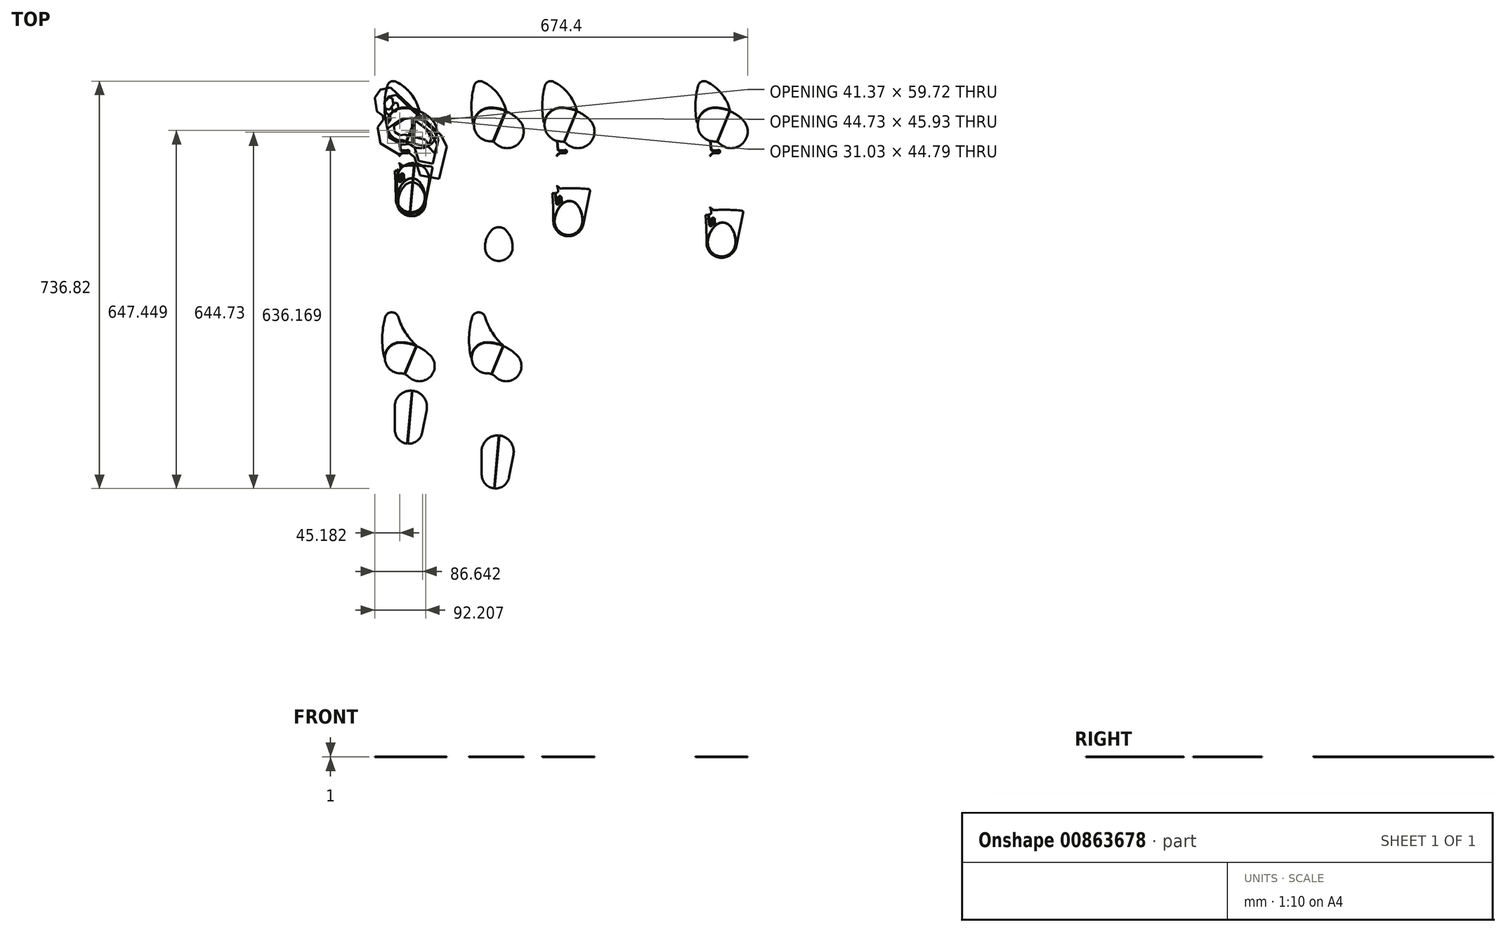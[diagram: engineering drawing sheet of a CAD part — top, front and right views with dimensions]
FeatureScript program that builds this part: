
annotation { "Feature Type Name" : "Feature", "Feature Type Description" : "" }
export const myFeature = defineFeature(function(context is Context, id is Id, definition is map)
    precondition{}
    {
        {
            var Q0;
            Q0=qCreatedBy(makeId("Top.planeOp"),FACE);
            var sketch = newSketch(context, id + "F0", { "sketchPlane" : qUnion([Q0])});
            skLineSegment(sketch, "E0", {"start": v(16.3, 2.6) * mm, "end": v(-34.11, 318.6) * mm, "construction": true});
            skLineSegment(sketch, "E1", {"start": v(66.8, 10.66) * mm, "end": v(119.85, 343.17) * mm, "construction": true});
            skLineSegment(sketch, "E2", {"start": v(40.9, 6.53) * mm, "end": v(40.9, 330.57) * mm, "construction": true});
            skLineSegment(sketch, "E3", {"start": v(-11.1, 295.2) * mm, "end": v(-3.27, 304.3) * mm});
            skLineSegment(sketch, "E4", {"start": v(-3.27, 304.3) * mm, "end": v(3.35, 302.53) * mm});
            skEllipse(sketch, "E5", {"center": v(40.9, 51.28) * mm, "majorRadius": 40 * mm, "minorRadius": 26.46 * mm, "majorAxis": v(0, -1)});
            skLineSegment(sketch, "E6", {"start": v(-9.36, 284.36) * mm, "end": v(-2.16, 282.28) * mm});
            skLineSegment(sketch, "E7", {"start": v(-2.16, 282.28) * mm, "end": v(4.97, 292.1) * mm});
            skLineSegment(sketch, "E8", {"start": v(3.35, 302.53) * mm, "end": v(4.97, 292.1) * mm});
            skLineSegment(sketch, "E9", {"start": v(-11.1, 295.2) * mm, "end": v(-9.36, 284.36) * mm});
            skLineSegment(sketch, "E10", {"start": v(-3.55, 233.47) * mm, "end": v(-5.87, 247.97) * mm});
            skLineSegment(sketch, "E11", {"start": v(-5.87, 247.97) * mm, "end": v(18.1, 264.24) * mm});
            skLineSegment(sketch, "E12", {"start": v(18.1, 264.24) * mm, "end": v(38.87, 267.55) * mm});
            skLineSegment(sketch, "E13", {"start": v(38.87, 267.55) * mm, "end": v(38.87, 221.62) * mm});
            skLineSegment(sketch, "E14", {"start": v(38.87, 221.62) * mm, "end": v(20.02, 227.48) * mm});
            skLineSegment(sketch, "E15", {"start": v(20.02, 227.48) * mm, "end": v(9.19, 225.76) * mm});
            skLineSegment(sketch, "E16", {"start": v(9.19, 225.76) * mm, "end": v(-3.55, 233.47) * mm});
            skLineSegment(sketch, "E17", {"start": v(43.15, 263.17) * mm, "end": v(71.87, 241.94) * mm});
            skLineSegment(sketch, "E18", {"start": v(71.87, 241.94) * mm, "end": v(84.21, 218.72) * mm});
            skLineSegment(sketch, "E19", {"start": v(84.21, 218.72) * mm, "end": v(79.5, 203.45) * mm});
            skLineSegment(sketch, "E20", {"start": v(68.35, 215.06) * mm, "end": v(79.5, 203.45) * mm});
            skLineSegment(sketch, "E21", {"start": v(68.35, 215.06) * mm, "end": v(42.84, 220.86) * mm});
            skLineSegment(sketch, "E22", {"start": v(42.84, 220.86) * mm, "end": v(43.15, 263.17) * mm});
            skLineSegment(sketch, "E23", {"start": v(39.24, 91.2) * mm, "end": v(39.24, 11.36) * mm});
            skLineSegment(sketch, "E24", {"start": v(42.24, 91.23) * mm, "end": v(42.24, 11.34) * mm});
            skLineSegment(sketch, "E25", {"start": v(-18.67, 318.73) * mm, "end": v(0, 322.49) * mm});
            skLineSegment(sketch, "E26", {"start": v(0, 322.49) * mm, "end": v(90.66, 236.65) * mm});
            skLineSegment(sketch, "E27", {"start": v(90.66, 236.65) * mm, "end": v(101.58, 215.64) * mm});
            skLineSegment(sketch, "E28", {"start": v(101.58, 215.64) * mm, "end": v(87.57, 157.1) * mm});
            skLineSegment(sketch, "E29", {"start": v(87.57, 157.1) * mm, "end": v(53.67, 163.5) * mm});
            skLineSegment(sketch, "E30", {"start": v(53.67, 163.5) * mm, "end": v(43.55, 196.6) * mm});
            skLineSegment(sketch, "E31", {"start": v(43.55, 196.6) * mm, "end": v(32.43, 204.68) * mm});
            skLineSegment(sketch, "E32", {"start": v(32.43, 204.68) * mm, "end": v(13.34, 202.21) * mm});
            skLineSegment(sketch, "E33", {"start": v(13.34, 202.21) * mm, "end": v(-18.63, 221.57) * mm});
            skLineSegment(sketch, "E34", {"start": v(-18.63, 221.57) * mm, "end": v(-23.28, 250.67) * mm});
            skLineSegment(sketch, "E35", {"start": v(-23.28, 250.67) * mm, "end": v(-13, 264.21) * mm});
            skLineSegment(sketch, "E36", {"start": v(-13, 264.21) * mm, "end": v(-14.18, 271.56) * mm});
            skLineSegment(sketch, "E37", {"start": v(-14.18, 271.56) * mm, "end": v(-24.79, 279.26) * mm});
            skLineSegment(sketch, "E38", {"start": v(-24.79, 279.26) * mm, "end": v(-28.68, 303.68) * mm});
            skLineSegment(sketch, "E39", {"start": v(-28.68, 303.68) * mm, "end": v(-18.67, 318.73) * mm});
            skSolve(sketch);
        }
        {
            var Q0;
            Q0=makeQuery(id+"F0.imprint","IMPRINT",FACE,{"disambiguationData":[TD([[makeQuery(id+"F0.imprint","IMPRINT",EDGE,{"derivedFrom":sQuery(id+"F0.wireOp",EDGE,"E3")}),1.0]])]});
            extrude(context, id + "F1", {"entities" : qUnion([Q0]), "depth" : 1 * mm, "offsetDistance" : 25 * mm});
        }
        {
            var Q0;
            Q0=makeQuery(id+"F1.opExtrude","SWEPT_BODY",BODY,{"disambiguationData":[OSD([sQuery(id+"F0.wireOp",EDGE,"E3"),sQuery(id+"F0.wireOp",EDGE,"E4"),sQuery(id+"F0.wireOp",EDGE,"E6"),sQuery(id+"F0.wireOp",EDGE,"E7"),sQuery(id+"F0.wireOp",EDGE,"E8"),sQuery(id+"F0.wireOp",EDGE,"E9"),sQuery(id+"F0.wireOp",EDGE,"E10"),sQuery(id+"F0.wireOp",EDGE,"E11"),sQuery(id+"F0.wireOp",EDGE,"E12"),sQuery(id+"F0.wireOp",EDGE,"E13"),sQuery(id+"F0.wireOp",EDGE,"E14"),sQuery(id+"F0.wireOp",EDGE,"E15"),sQuery(id+"F0.wireOp",EDGE,"E16"),sQuery(id+"F0.wireOp",EDGE,"E17"),sQuery(id+"F0.wireOp",EDGE,"E18"),sQuery(id+"F0.wireOp",EDGE,"E19"),sQuery(id+"F0.wireOp",EDGE,"E20"),sQuery(id+"F0.wireOp",EDGE,"E21"),sQuery(id+"F0.wireOp",EDGE,"E22"),sQuery(id+"F0.wireOp",EDGE,"E25"),sQuery(id+"F0.wireOp",EDGE,"E26"),sQuery(id+"F0.wireOp",EDGE,"E27"),sQuery(id+"F0.wireOp",EDGE,"E28"),sQuery(id+"F0.wireOp",EDGE,"E29"),sQuery(id+"F0.wireOp",EDGE,"E30"),sQuery(id+"F0.wireOp",EDGE,"E31"),sQuery(id+"F0.wireOp",EDGE,"E32"),sQuery(id+"F0.wireOp",EDGE,"E33"),sQuery(id+"F0.wireOp",EDGE,"E34"),sQuery(id+"F0.wireOp",EDGE,"E35"),sQuery(id+"F0.wireOp",EDGE,"E36"),sQuery(id+"F0.wireOp",EDGE,"E37"),sQuery(id+"F0.wireOp",EDGE,"E38"),sQuery(id+"F0.wireOp",EDGE,"E39")])]});
            var Q1;
            Q1=makeQuery(id+"F1.opExtrude","CAP_VERTEX",VERTEX,{"disambiguationData":[OSD([sQuery(id+"F0.wireOp",EDGE,"E12"),sQuery(id+"F0.wireOp",EDGE,"E13")])],"isStart":false});
            transform(context, id + "F2", {"entities" : qUnion([Q0]), "transformType" : TransformType.SCALE_UNIFORMLY, "scale" : .75, "scalePoint" : qUnion([Q1]), "makeCopy" : true});
        }
        {
            var Q0;
            Q0=makeQuery(id+"F2.opPattern","COPY",BODY,{"derivedFrom":makeQuery(id+"F1.opExtrude","SWEPT_BODY",BODY,{"disambiguationData":[OSD([sQuery(id+"F0.wireOp",EDGE,"E3"),sQuery(id+"F0.wireOp",EDGE,"E4"),sQuery(id+"F0.wireOp",EDGE,"E6"),sQuery(id+"F0.wireOp",EDGE,"E7"),sQuery(id+"F0.wireOp",EDGE,"E8"),sQuery(id+"F0.wireOp",EDGE,"E9"),sQuery(id+"F0.wireOp",EDGE,"E10"),sQuery(id+"F0.wireOp",EDGE,"E11"),sQuery(id+"F0.wireOp",EDGE,"E12"),sQuery(id+"F0.wireOp",EDGE,"E13"),sQuery(id+"F0.wireOp",EDGE,"E14"),sQuery(id+"F0.wireOp",EDGE,"E15"),sQuery(id+"F0.wireOp",EDGE,"E16"),sQuery(id+"F0.wireOp",EDGE,"E17"),sQuery(id+"F0.wireOp",EDGE,"E18"),sQuery(id+"F0.wireOp",EDGE,"E19"),sQuery(id+"F0.wireOp",EDGE,"E20"),sQuery(id+"F0.wireOp",EDGE,"E21"),sQuery(id+"F0.wireOp",EDGE,"E22"),sQuery(id+"F0.wireOp",EDGE,"E25"),sQuery(id+"F0.wireOp",EDGE,"E26"),sQuery(id+"F0.wireOp",EDGE,"E27"),sQuery(id+"F0.wireOp",EDGE,"E28"),sQuery(id+"F0.wireOp",EDGE,"E29"),sQuery(id+"F0.wireOp",EDGE,"E30"),sQuery(id+"F0.wireOp",EDGE,"E31"),sQuery(id+"F0.wireOp",EDGE,"E32"),sQuery(id+"F0.wireOp",EDGE,"E33"),sQuery(id+"F0.wireOp",EDGE,"E34"),sQuery(id+"F0.wireOp",EDGE,"E35"),sQuery(id+"F0.wireOp",EDGE,"E36"),sQuery(id+"F0.wireOp",EDGE,"E37"),sQuery(id+"F0.wireOp",EDGE,"E38"),sQuery(id+"F0.wireOp",EDGE,"E39")])]}),"instanceName":"1"});
            transform(context, id + "F3", {"entities" : qUnion([Q0]), "transformType" : TransformType.TRANSLATION_3D, "dx" : 0.6 * mm, "dy" : 0 * mm, "dz" : 0 * mm, "makeCopy" : false});
        }
        {
            var Q0;
            Q0=qCreatedBy(makeId("Top.planeOp"),FACE);
            var sketch = newSketch(context, id + "F4", { "sketchPlane" : qUnion([Q0])});
            skLineSegment(sketch, "E40", {"start": v(8.54, 339.93) * mm, "end": v(565.92, 339.93) * mm, "construction": true});
            skPoint(sketch, "E41", {"position": v(287.23, 339.93) * mm});
            skSolve(sketch);
        }
        {
            var Q0;
            Q0=qCreatedBy(makeId("Top.planeOp"),FACE);
            var sketch = newSketch(context, id + "F5", { "sketchPlane" : qUnion([Q0])});
            skArc(sketch, "E42", {"start": v(23.72, 285.12) * mm, "mid": v(-6.28, 255.12) * mm, "end": v(23.72, 225.12) * mm});
            skPoint(sketch, "E43", {"position": v(38.72, 251.89) * mm});
            skLineSegment(sketch, "E44", {"start": v(23.72, 285.12) * mm, "end": v(23.72, 225.12) * mm, "construction": true});
            skLineSegment(sketch, "E45", {"start": v(28.48, 224.17) * mm, "end": v(51.44, 279.6) * mm, "construction": true});
            skLineSegment(sketch, "E46", {"start": v(38.72, 244.3) * mm, "end": v(38.72, 259.48) * mm, "construction": true});
            skPoint(sketch, "E47", {"position": v(39.96, 251.89) * mm});
            skArc(sketch, "E48", {"start": v(50.98, 279.8) * mm, "mid": v(37.6, 283.78) * mm, "end": v(23.72, 285.12) * mm});
            skArc(sketch, "E49", {"start": v(28.01, 224.36) * mm, "mid": v(25.9, 224.93) * mm, "end": v(23.72, 225.12) * mm});
            skLineSegment(sketch, "E50", {"start": v(50.98, 279.8) * mm, "end": v(28.01, 224.36) * mm});
            skLineSegment(sketch, "E51.MirrorCS", {"start": v(51.9, 279.41) * mm, "end": v(28.94, 223.97) * mm});
            skArc(sketch, "E52.MirrorCS", {"start": v(51.9, 279.41) * mm, "mid": v(64.17, 272.77) * mm, "end": v(74.94, 263.9) * mm});
            skArc(sketch, "E53.MirrorCS", {"start": v(74.94, 263.9) * mm, "mid": v(74.94, 221.48) * mm, "end": v(32.5, 221.48) * mm});
            skLineSegment(sketch, "E54.MirrorCS", {"start": v(74.94, 263.9) * mm, "end": v(32.5, 221.48) * mm, "construction": true});
            skArc(sketch, "E55.MirrorCS", {"start": v(28.94, 223.97) * mm, "mid": v(30.83, 222.88) * mm, "end": v(32.5, 221.48) * mm});
            skArc(sketch, "E56", {"start": v(13.72, 114.6) * mm, "mid": v(38.72, 89.6) * mm, "end": v(63.72, 114.6) * mm});
            skLineSegment(sketch, "E57", {"start": v(13.72, 114.6) * mm, "end": v(63.72, 114.6) * mm, "construction": true});
            skArc(sketch, "E58", {"start": v(25.25, 144.75) * mm, "mid": v(16.7, 130.74) * mm, "end": v(13.72, 114.6) * mm});
            skArc(sketch, "E59", {"start": v(52.2, 144.75) * mm, "mid": v(38.72, 150.77) * mm, "end": v(25.25, 144.75) * mm});
            skArc(sketch, "E60", {"start": v(63.72, 114.6) * mm, "mid": v(60.74, 130.74) * mm, "end": v(52.2, 144.75) * mm});
            skLineSegment(sketch, "E61", {"start": v(38.72, 114.6) * mm, "end": v(38.72, 150.77) * mm, "construction": true});
            skArc(sketch, "E62", {"start": v(9.99, 332.78) * mm, "mid": v(0.32, 332.95) * mm, "end": v(-5.91, 325.56) * mm});
            skArc(sketch, "E63", {"start": v(51.82, 280.53) * mm, "mid": v(38.05, 284.7) * mm, "end": v(23.72, 286.12) * mm});
            skArc(sketch, "E64", {"start": v(23.72, 286.12) * mm, "mid": v(1.92, 277.16) * mm, "end": v(-7.28, 255.45) * mm});
            skLineSegment(sketch, "E65", {"start": v(-6.28, 255.12) * mm, "end": v(-6.28, 271.74) * mm, "construction": true});
            skLineSegment(sketch, "E66", {"start": v(96.35, 301.63) * mm, "end": v(20.38, 356.47) * mm, "construction": true});
            skArc(sketch, "E67", {"start": v(-5.91, 325.56) * mm, "mid": v(-10.75, 290.58) * mm, "end": v(-7.28, 255.45) * mm});
            skArc(sketch, "E68", {"start": v(9.99, 332.78) * mm, "mid": v(36.66, 311.26) * mm, "end": v(51.82, 280.53) * mm});
            skSolve(sketch);
        }
        {
            var Q0;
            Q0=qCreatedBy(makeId("Top.planeOp"),FACE);
            var sketch = newSketch(context, id + "F6", { "sketchPlane" : qUnion([Q0])});
            skArc(sketch, "E69", {"start": v(17.17, -139.43) * mm, "mid": v(-10.33, -166.93) * mm, "end": v(17.17, -194.43) * mm});
            skPoint(sketch, "E70", {"position": v(34.67, -170.7) * mm});
            skLineSegment(sketch, "E71", {"start": v(17.17, -139.43) * mm, "end": v(17.17, -194.43) * mm, "construction": true});
            skLineSegment(sketch, "E72", {"start": v(25.6, -196.1) * mm, "end": v(46.64, -145.3) * mm, "construction": true});
            skLineSegment(sketch, "E73", {"start": v(34.67, -201.35) * mm, "end": v(34.67, -140.06) * mm, "construction": true});
            skPoint(sketch, "E74", {"position": v(36.12, -170.7) * mm});
            skArc(sketch, "E75", {"start": v(46.18, -145.1) * mm, "mid": v(31.95, -140.86) * mm, "end": v(17.17, -139.43) * mm});
            skArc(sketch, "E76", {"start": v(25.13, -195.92) * mm, "mid": v(21.22, -194.8) * mm, "end": v(17.17, -194.43) * mm});
            skLineSegment(sketch, "E77", {"start": v(46.18, -145.1) * mm, "end": v(25.13, -195.92) * mm});
            skLineSegment(sketch, "E78.MirrorCS", {"start": v(47.1, -145.49) * mm, "end": v(26.05, -196.3) * mm});
            skArc(sketch, "E79.MirrorCS", {"start": v(47.1, -145.49) * mm, "mid": v(60.16, -152.55) * mm, "end": v(71.62, -161.99) * mm});
            skArc(sketch, "E80.MirrorCS", {"start": v(71.62, -161.99) * mm, "mid": v(71.62, -200.88) * mm, "end": v(32.73, -200.88) * mm});
            skLineSegment(sketch, "E81.MirrorCS", {"start": v(71.62, -161.99) * mm, "end": v(32.73, -200.88) * mm, "construction": true});
            skArc(sketch, "E82.MirrorCS", {"start": v(26.05, -196.3) * mm, "mid": v(29.6, -198.28) * mm, "end": v(32.73, -200.88) * mm});
            skLineSegment(sketch, "E83", {"start": v(32.8, -296.86) * mm, "end": v(36.55, -255.05) * mm, "construction": true});
            skArc(sketch, "E84", {"start": v(14.16, -93.23) * mm, "mid": v(2.03, -84.29) * mm, "end": v(-9.89, -93.5) * mm});
            skArc(sketch, "E85", {"start": v(47.02, -144.37) * mm, "mid": v(32.4, -139.93) * mm, "end": v(17.17, -138.43) * mm});
            skArc(sketch, "E86", {"start": v(17.17, -138.43) * mm, "mid": v(-2.85, -146.65) * mm, "end": v(-11.32, -166.56) * mm});
            skLineSegment(sketch, "E87", {"start": v(-10.33, -166.93) * mm, "end": v(-10.33, -131.36) * mm, "construction": true});
            skLineSegment(sketch, "E88", {"start": v(130.4, -102) * mm, "end": v(54.42, -47.17) * mm, "construction": true});
            skArc(sketch, "E89", {"start": v(-9.89, -93.5) * mm, "mid": v(-15.12, -129.94) * mm, "end": v(-11.32, -166.56) * mm});
            skArc(sketch, "E90", {"start": v(14.16, -93.23) * mm, "mid": v(26.95, -121.14) * mm, "end": v(47.02, -144.37) * mm});
            skLineSegment(sketch, "E91", {"start": v(38.65, -226) * mm, "end": v(30.07, -321.71) * mm});
            skArc(sketch, "E92", {"start": v(7.8, -297.08) * mm, "mid": v(14.25, -313.63) * mm, "end": v(30.07, -321.71) * mm});
            skLineSegment(sketch, "E93", {"start": v(7.8, -297.08) * mm, "end": v(7.44, -255.3) * mm});
            skPoint(sketch, "E94", {"position": v(34.67, -275.95) * mm});
            skArc(sketch, "E95", {"start": v(7.44, -255.3) * mm, "mid": v(16.63, -233.81) * mm, "end": v(38.65, -226) * mm});
            skLineSegment(sketch, "E96.MirrorCS", {"start": v(39.65, -226.1) * mm, "end": v(31.06, -321.8) * mm});
            skArc(sketch, "E97.MirrorCS", {"start": v(57.36, -301.53) * mm, "mid": v(48.06, -316.66) * mm, "end": v(31.06, -321.8) * mm});
            skLineSegment(sketch, "E98.MirrorCS", {"start": v(57.36, -301.53) * mm, "end": v(65.15, -260.48) * mm});
            skArc(sketch, "E99.MirrorCS", {"start": v(65.15, -260.48) * mm, "mid": v(59.93, -237.7) * mm, "end": v(39.65, -226.1) * mm});
            skLineSegment(sketch, "E100", {"start": v(71.1, -321.86) * mm, "end": v(-52.97, -321.86) * mm, "construction": true});
            skLineSegment(sketch, "E101", {"start": v(30.56, -321.76) * mm, "end": v(39.15, -226.05) * mm, "construction": true});
            skSolve(sketch);
        }
        {
            var Q0;
            Q0 = qSketchRegion(id + "F5", true);
            var Q1;
            Q1 = qSketchRegion(id + "F6", true);
            extrude(context, id + "F7", {"entities" : qUnion([Q0, Q1]), "depth" : 1 * mm, "offsetDistance" : 25 * mm});
        }
        {
            var Q0;
            Q0=makeQuery(id+"F7.opExtrude","SWEPT_BODY",BODY,{"disambiguationData":[OSD([sQuery(id+"F5.wireOp",EDGE,"E42"),sQuery(id+"F5.wireOp",EDGE,"E48"),sQuery(id+"F5.wireOp",EDGE,"E49"),sQuery(id+"F5.wireOp",EDGE,"E50")])]});
            var Q1;
            Q1=makeQuery(id+"F7.opExtrude","SWEPT_BODY",BODY,{"disambiguationData":[OSD([sQuery(id+"F5.wireOp",EDGE,"E51.MirrorCS"),sQuery(id+"F5.wireOp",EDGE,"E52.MirrorCS"),sQuery(id+"F5.wireOp",EDGE,"E53.MirrorCS"),sQuery(id+"F5.wireOp",EDGE,"E55.MirrorCS")])]});
            var Q2;
            Q2=makeQuery(id+"F7.opExtrude","SWEPT_BODY",BODY,{"disambiguationData":[OSD([sQuery(id+"F5.wireOp",EDGE,"E56"),sQuery(id+"F5.wireOp",EDGE,"E58"),sQuery(id+"F5.wireOp",EDGE,"E59"),sQuery(id+"F5.wireOp",EDGE,"E60")])]});
            var Q3;
            Q3=makeQuery(id+"F7.opExtrude","SWEPT_BODY",BODY,{"disambiguationData":[OSD([sQuery(id+"F5.wireOp",EDGE,"8W2EzEg6-PsAx-j8A4-CxcC-4UdQx331VMs9"),sQuery(id+"F5.wireOp",EDGE,"E62"),sQuery(id+"F5.wireOp",EDGE,"1FPgRCsu-etEN-6vr9-Zu0G-JbxTRO6JNvhZ"),sQuery(id+"F5.wireOp",EDGE,"E63"),sQuery(id+"F5.wireOp",EDGE,"E64")])]});
            var Q4;
            Q4=makeQuery(id+"F7.opExtrude","SWEPT_BODY",BODY,{"disambiguationData":[OSD([sQuery(id+"F6.wireOp",EDGE,"5b57f492-1596-40e6-b2e3-11fcfe89af0d"),sQuery(id+"F6.wireOp",EDGE,"10afdee0-af68-4db0-a130-1e2b4957d369"),sQuery(id+"F6.wireOp",EDGE,"81680ccf-cd87-4daf-b075-65e9a944a0f2"),sQuery(id+"F6.wireOp",EDGE,"42a77d29-89d0-48d6-aa2a-1530d47a3efc"),sQuery(id+"F6.wireOp",EDGE,"a1937c93-1bbb-44bc-8000-acc418f4d61c")])]});
            var Q5;
            Q5=makeQuery(id+"F7.opExtrude","SWEPT_BODY",BODY,{"disambiguationData":[OSD([sQuery(id+"F6.wireOp",EDGE,"02ee120c-1508-4c41-bed1-1e04da6d7a0c"),sQuery(id+"F6.wireOp",EDGE,"ace646e3-ddf2-4daf-99df-f5f96f0c8b72"),sQuery(id+"F6.wireOp",EDGE,"d4bb21a5-84e0-4ec6-88e1-a15759d7ab0e"),sQuery(id+"F6.wireOp",EDGE,"e1ab6dd2-551a-4460-87ee-2f2734b56fd1")])]});
            var Q6;
            Q6=makeQuery(id+"F7.opExtrude","SWEPT_BODY",BODY,{"disambiguationData":[OSD([sQuery(id+"F6.wireOp",EDGE,"aca01ad1-2727-46c1-b1ea-e2278572d0a3.MirrorCS"),sQuery(id+"F6.wireOp",EDGE,"95053200-b2d1-4fb4-8a27-d9cd398e6184.MirrorCS"),sQuery(id+"F6.wireOp",EDGE,"b14f3b0d-07c5-4903-9c96-b1073ed3af53.MirrorCS"),sQuery(id+"F6.wireOp",EDGE,"13823a02-7994-452b-b934-c440785b61fb.MirrorCS")])]});
            var Q7;
            Q7=makeQuery(id+"F7.opExtrude","SWEPT_BODY",BODY,{"disambiguationData":[OSD([sQuery(id+"F6.wireOp",EDGE,"76ac6f00-afaf-4b2d-95c2-d09c5d23ff7b"),sQuery(id+"F6.wireOp",EDGE,"820a2da9-31c0-4ea2-8999-fd9844493cd6"),sQuery(id+"F6.wireOp",EDGE,"e1ef3a47-9e0c-4530-8c34-01f70c3173e6"),sQuery(id+"F6.wireOp",EDGE,"5ff26bff-9000-4c28-a5b2-e0ee19cc0048")])]});
            var Q8;
            Q8=makeQuery(id+"F7.opExtrude","SWEPT_BODY",BODY,{"disambiguationData":[OSD([sQuery(id+"F6.wireOp",EDGE,"b6ba2a53-2d88-4030-befe-966a330606390.MirrorCS"),sQuery(id+"F6.wireOp",EDGE,"e51e67fa-598f-4ce7-9503-9b7065003b4d0.MirrorCS"),sQuery(id+"F6.wireOp",EDGE,"5a4d4938-92c4-42d2-ae7a-708136eab2620.MirrorCS"),sQuery(id+"F6.wireOp",EDGE,"2ea4096e-a5a6-4afc-88fb-b437cae464f20.MirrorCS")])]});
            var Q9;
            Q9=makeQuery(id+"F7.opExtrude","SWEPT_BODY",BODY,{"disambiguationData":[OSD([sQuery(id+"F6.wireOp",EDGE,"E84"),sQuery(id+"F6.wireOp",EDGE,"E85"),sQuery(id+"F6.wireOp",EDGE,"E86"),sQuery(id+"F6.wireOp",EDGE,"E89"),sQuery(id+"F6.wireOp",EDGE,"E90")])]});
            var Q10;
            Q10=makeQuery(id+"F7.opExtrude","SWEPT_BODY",BODY,{"disambiguationData":[OSD([sQuery(id+"F6.wireOp",EDGE,"E69"),sQuery(id+"F6.wireOp",EDGE,"E75"),sQuery(id+"F6.wireOp",EDGE,"E76"),sQuery(id+"F6.wireOp",EDGE,"E77")])]});
            var Q11;
            Q11=makeQuery(id+"F7.opExtrude","SWEPT_BODY",BODY,{"disambiguationData":[OSD([sQuery(id+"F6.wireOp",EDGE,"E78.MirrorCS"),sQuery(id+"F6.wireOp",EDGE,"E79.MirrorCS"),sQuery(id+"F6.wireOp",EDGE,"E80.MirrorCS"),sQuery(id+"F6.wireOp",EDGE,"E82.MirrorCS")])]});
            var Q12;
            Q12=makeQuery(id+"F7.opExtrude","SWEPT_BODY",BODY,{"disambiguationData":[OSD([sQuery(id+"F6.wireOp",EDGE,"E91"),sQuery(id+"F6.wireOp",EDGE,"E92"),sQuery(id+"F6.wireOp",EDGE,"E93"),sQuery(id+"F6.wireOp",EDGE,"E95")])]});
            var Q13;
            Q13=makeQuery(id+"F7.opExtrude","SWEPT_BODY",BODY,{"disambiguationData":[OSD([sQuery(id+"F6.wireOp",EDGE,"E96.MirrorCS"),sQuery(id+"F6.wireOp",EDGE,"E97.MirrorCS"),sQuery(id+"F6.wireOp",EDGE,"E98.MirrorCS"),sQuery(id+"F6.wireOp",EDGE,"E99.MirrorCS")])]});
            transform(context, id + "F8", {"entities" : qUnion([Q0, Q1, Q2, Q3, Q4, Q5, Q6, Q7, Q8, Q9, Q10, Q11, Q12, Q13]), "transformType" : TransformType.TRANSLATION_3D, "dx" : 157 * mm, "dy" : 0 * mm, "dz" : 0 * mm, "makeCopy" : true});
        }
        {
            var Q0;
            Q0=makeQuery(id+"F8.opPattern","COPY",BODY,{"derivedFrom":makeQuery(id+"F7.opExtrude","SWEPT_BODY",BODY,{"disambiguationData":[OSD([sQuery(id+"F5.wireOp",EDGE,"E56"),sQuery(id+"F5.wireOp",EDGE,"E58"),sQuery(id+"F5.wireOp",EDGE,"E59"),sQuery(id+"F5.wireOp",EDGE,"E60")])]}),"instanceName":"1"});
            var Q1;
            Q1=makeQuery(id+"F8.opPattern","COPY",BODY,{"derivedFrom":makeQuery(id+"F7.opExtrude","SWEPT_BODY",BODY,{"disambiguationData":[OSD([sQuery(id+"F6.wireOp",EDGE,"76ac6f00-afaf-4b2d-95c2-d09c5d23ff7b"),sQuery(id+"F6.wireOp",EDGE,"820a2da9-31c0-4ea2-8999-fd9844493cd6"),sQuery(id+"F6.wireOp",EDGE,"e1ef3a47-9e0c-4530-8c34-01f70c3173e6"),sQuery(id+"F6.wireOp",EDGE,"5ff26bff-9000-4c28-a5b2-e0ee19cc0048")])]}),"instanceName":"1"});
            var Q2;
            Q2=makeQuery(id+"F8.opPattern","COPY",BODY,{"derivedFrom":makeQuery(id+"F7.opExtrude","SWEPT_BODY",BODY,{"disambiguationData":[OSD([sQuery(id+"F6.wireOp",EDGE,"b6ba2a53-2d88-4030-befe-966a330606390.MirrorCS"),sQuery(id+"F6.wireOp",EDGE,"e51e67fa-598f-4ce7-9503-9b7065003b4d0.MirrorCS"),sQuery(id+"F6.wireOp",EDGE,"5a4d4938-92c4-42d2-ae7a-708136eab2620.MirrorCS"),sQuery(id+"F6.wireOp",EDGE,"2ea4096e-a5a6-4afc-88fb-b437cae464f20.MirrorCS")])]}),"instanceName":"1"});
            var Q3;
            Q3=makeQuery(id+"F8.opPattern","COPY",BODY,{"derivedFrom":makeQuery(id+"F7.opExtrude","SWEPT_BODY",BODY,{"disambiguationData":[OSD([sQuery(id+"F6.wireOp",EDGE,"E91"),sQuery(id+"F6.wireOp",EDGE,"E92"),sQuery(id+"F6.wireOp",EDGE,"E93"),sQuery(id+"F6.wireOp",EDGE,"E95")])]}),"instanceName":"1"});
            var Q4;
            Q4=makeQuery(id+"F8.opPattern","COPY",BODY,{"derivedFrom":makeQuery(id+"F7.opExtrude","SWEPT_BODY",BODY,{"disambiguationData":[OSD([sQuery(id+"F6.wireOp",EDGE,"E96.MirrorCS"),sQuery(id+"F6.wireOp",EDGE,"E97.MirrorCS"),sQuery(id+"F6.wireOp",EDGE,"E98.MirrorCS"),sQuery(id+"F6.wireOp",EDGE,"E99.MirrorCS")])]}),"instanceName":"1"});
            transform(context, id + "F9", {"entities" : qUnion([Q0, Q1, Q2, Q3, Q4]), "transformType" : TransformType.TRANSLATION_3D, "dx" : 0 * mm, "dy" : -81 * mm, "dz" : 0 * mm, "makeCopy" : false});
        }
        {
            var Q0;
            Q0=makeQuery(id+"F7.opExtrude","SWEPT_BODY",BODY,{"disambiguationData":[OSD([sQuery(id+"F6.wireOp",EDGE,"E91"),sQuery(id+"F6.wireOp",EDGE,"E92"),sQuery(id+"F6.wireOp",EDGE,"E93"),sQuery(id+"F6.wireOp",EDGE,"E95")])]});
            var Q1;
            Q1=makeQuery(id+"F7.opExtrude","SWEPT_BODY",BODY,{"disambiguationData":[OSD([sQuery(id+"F6.wireOp",EDGE,"E96.MirrorCS"),sQuery(id+"F6.wireOp",EDGE,"E97.MirrorCS"),sQuery(id+"F6.wireOp",EDGE,"E98.MirrorCS"),sQuery(id+"F6.wireOp",EDGE,"E99.MirrorCS")])]});
            transform(context, id + "F10", {"entities" : qUnion([Q0, Q1]), "transformType" : TransformType.TRANSLATION_3D, "dx" : 4 * mm, "dy" : 411.6 * mm, "dz" : 0 * mm, "makeCopy" : true});
        }
        {
            var Q0;
            Q0=qCreatedBy(makeId("Top.planeOp"),FACE);
            var sketch = newSketch(context, id + "F11", { "sketchPlane" : qUnion([Q0])});
            skLineSegment(sketch, "E102", {"start": v(29.12, 224.4) * mm, "end": v(51.7, 278.95) * mm});
            skArc(sketch, "E103", {"start": v(74.94, 263.9) * mm, "mid": v(64.38, 272.63) * mm, "end": v(52.37, 279.21) * mm});
            skArc(sketch, "E104", {"start": v(32.5, 221.48) * mm, "mid": v(74.94, 221.48) * mm, "end": v(74.94, 263.9) * mm});
            skLineSegment(sketch, "E105", {"start": v(50.78, 279.33) * mm, "end": v(28.2, 224.8) * mm});
            skArc(sketch, "E106", {"start": v(50.5, 279.98) * mm, "mid": v(37.36, 283.82) * mm, "end": v(23.72, 285.12) * mm});
            skArc(sketch, "E107", {"start": v(23.72, 285.12) * mm, "mid": v(-6.28, 255.12) * mm, "end": v(23.72, 225.12) * mm});
            skLineSegment(sketch, "E108", {"start": v(23.72, 286.12) * mm, "end": v(23.72, 286.12) * mm});
            skArc(sketch, "E109", {"start": v(50.9, 280.9) * mm, "mid": v(37.56, 284.8) * mm, "end": v(23.72, 286.12) * mm});
            skLineSegment(sketch, "E110", {"start": v(9.99, 332.78) * mm, "end": v(9.99, 332.78) * mm});
            skArc(sketch, "E111", {"start": v(15.78, 225.8) * mm, "mid": v(-6.39, 259.12) * mm, "end": v(23.72, 285.5) * mm});
            skArc(sketch, "E112", {"start": v(23.72, 285.5) * mm, "mid": v(37.43, 284.2) * mm, "end": v(50.64, 280.33) * mm});
            skArc(sketch, "E113", {"start": v(23.72, 224.74) * mm, "mid": v(25.61, 224.6) * mm, "end": v(27.46, 224.15) * mm});
            skLineSegment(sketch, "E114", {"start": v(51.13, 279.19) * mm, "end": v(28.54, 224.65) * mm});
            skArc(sketch, "E115", {"start": v(-1.86, 238.29) * mm, "mid": v(-3.23, 269.65) * mm, "end": v(23.72, 285.74) * mm});
            skArc(sketch, "E116", {"start": v(23.72, 285.74) * mm, "mid": v(37.5, 284.43) * mm, "end": v(50.77, 280.55) * mm});
            skLineSegment(sketch, "E117", {"start": v(28.77, 224.55) * mm, "end": v(51.36, 279.09) * mm});
            skArc(sketch, "E118", {"start": v(52.51, 279.56) * mm, "mid": v(64.59, 272.94) * mm, "end": v(75.2, 264.17) * mm});
            skArc(sketch, "E119", {"start": v(75.2, 264.17) * mm, "mid": v(77.76, 224.12) * mm, "end": v(38.37, 216.48) * mm});
            skArc(sketch, "E120", {"start": v(32.24, 221.21) * mm, "mid": v(30.8, 222.45) * mm, "end": v(29.18, 223.44) * mm});
            skArc(sketch, "E121", {"start": v(76.61, 265.59) * mm, "mid": v(84.9, 251.42) * mm, "end": v(85.17, 235.01) * mm});
            skArc(sketch, "E122", {"start": v(-9.83, 255.12) * mm, "mid": v(-8.9, 247.25) * mm, "end": v(-6.14, 239.83) * mm});
            skLineSegment(sketch, "E123.bottom", {"start": v(7.72, 198.27) * mm, "end": v(12.7, 198.76) * mm});
            skLineSegment(sketch, "E123.top", {"start": v(7.86, 196.78) * mm, "end": v(12.84, 197.27) * mm});
            skLineSegment(sketch, "E123.left", {"start": v(7.27, 197.73) * mm, "end": v(7.32, 197.23) * mm});
            skLineSegment(sketch, "E124.bottom", {"start": v(8.01, 195.29) * mm, "end": v(12.99, 195.78) * mm});
            skLineSegment(sketch, "E124.top", {"start": v(8.16, 193.8) * mm, "end": v(13.13, 194.29) * mm});
            skLineSegment(sketch, "E124.left", {"start": v(7.56, 194.74) * mm, "end": v(7.61, 194.24) * mm});
            skLineSegment(sketch, "E124.right", {"start": v(13.53, 195.33) * mm, "end": v(13.58, 194.83) * mm});
            skLineSegment(sketch, "E125.bottom", {"start": v(8.3, 192.3) * mm, "end": v(13.28, 192.8) * mm});
            skLineSegment(sketch, "E125.top", {"start": v(8.45, 190.81) * mm, "end": v(13.43, 191.3) * mm});
            skArc(sketch, "E126", {"start": v(23.72, 225.12) * mm, "mid": v(25.67, 224.97) * mm, "end": v(27.58, 224.5) * mm});
            skArc(sketch, "E127", {"start": v(29.35, 223.77) * mm, "mid": v(31.02, 222.75) * mm, "end": v(32.5, 221.48) * mm});
            skArc(sketch, "E128", {"start": v(-6.27, 325.67) * mm, "mid": v(-11.1, 292.42) * mm, "end": v(-8.38, 258.94) * mm});
            skArc(sketch, "E129", {"start": v(76.61, 265.59) * mm, "mid": v(73.37, 268.64) * mm, "end": v(69.95, 271.5) * mm});
            skArc(sketch, "E130", {"start": v(-8.2, 326.18) * mm, "mid": v(-13.12, 291.64) * mm, "end": v(-10.01, 256.9) * mm});
            skArc(sketch, "E131", {"start": v(-10.01, 256.9) * mm, "mid": v(-9.87, 256.02) * mm, "end": v(-9.83, 255.12) * mm});
            skLineSegment(sketch, "E132", {"start": v(-9.83, 267.62) * mm, "end": v(-9.83, 242.62) * mm, "construction": true});
            skLineSegment(sketch, "E133.top", {"start": v(7.28, 202.75) * mm, "end": v(12.25, 203.24) * mm});
            skLineSegment(sketch, "E133.left", {"start": v(6.68, 203.7) * mm, "end": v(6.73, 203.2) * mm});
            skLineSegment(sketch, "E134", {"start": v(12.65, 204.29) * mm, "end": v(12.7, 203.79) * mm});
            skArc(sketch, "E135", {"start": v(8.67, 188.57) * mm, "mid": v(6.66, 189.18) * mm, "end": v(5.67, 191.04) * mm});
            skLineSegment(sketch, "E136", {"start": v(5.67, 191.04) * mm, "end": v(4.4, 203.98) * mm});
            skArc(sketch, "E137", {"start": v(4.4, 203.98) * mm, "mid": v(0.81, 222.4) * mm, "end": v(-6.14, 239.83) * mm});
            skLineSegment(sketch, "E138.bottom", {"start": v(7.42, 201.26) * mm, "end": v(12.4, 201.75) * mm});
            skLineSegment(sketch, "E138.top", {"start": v(7.57, 199.77) * mm, "end": v(12.55, 200.26) * mm});
            skLineSegment(sketch, "E138.left", {"start": v(6.97, 200.71) * mm, "end": v(7.02, 200.22) * mm});
            skLineSegment(sketch, "E138.right", {"start": v(12.95, 201.3) * mm, "end": v(13, 200.8) * mm});
            skArc(sketch, "E139", {"start": v(74.67, 188.57) * mm, "mid": v(41.67, 190.2) * mm, "end": v(8.67, 188.57) * mm, "construction": true});
            skLineSegment(sketch, "E140", {"start": v(8.67, 188.57) * mm, "end": v(29.1, 190.58) * mm, "construction": true});
            skLineSegment(sketch, "E141", {"start": v(32.22, 174.02) * mm, "end": v(72.8, 174.02) * mm, "construction": true});
            skLineSegment(sketch, "E142", {"start": v(41.67, 190.2) * mm, "end": v(41.67, 161.92) * mm, "construction": true});
            skArc(sketch, "E143", {"start": v(74.67, 188.57) * mm, "mid": v(76.69, 189.18) * mm, "end": v(77.68, 191.04) * mm, "construction": true});
            skLineSegment(sketch, "E144", {"start": v(77.68, 191.04) * mm, "end": v(75.88, 172.73) * mm, "construction": true});
            skLineSegment(sketch, "E145", {"start": v(77.68, 191.04) * mm, "end": v(77.68, 176.48) * mm, "construction": true});
            skLineSegment(sketch, "E146", {"start": v(5.67, 191.04) * mm, "end": v(7.23, 175.16) * mm, "construction": true});
            skArc(sketch, "E147", {"start": v(77.68, 191.04) * mm, "mid": v(80.65, 213.16) * mm, "end": v(85.17, 235.01) * mm, "construction": true});
            skLineSegment(sketch, "E148", {"start": v(41.67, 190.2) * mm, "end": v(59.6, 190.2) * mm, "construction": true});
            skArc(sketch, "E149", {"start": v(85.17, 235.01) * mm, "mid": v(81.08, 215.6) * mm, "end": v(78.2, 195.97) * mm});
            skArc(sketch, "E150", {"start": v(13.63, 189.02) * mm, "mid": v(11.15, 188.8) * mm, "end": v(8.67, 188.57) * mm});
            skArc(sketch, "E151", {"start": v(13.63, 189.02) * mm, "mid": v(17.25, 190.31) * mm, "end": v(19.76, 193.22) * mm});
            skArc(sketch, "E152", {"start": v(19.76, 193.22) * mm, "mid": v(20.62, 194.2) * mm, "end": v(21.86, 194.62) * mm});
            skArc(sketch, "E153", {"start": v(78.2, 195.97) * mm, "mid": v(77.2, 194.14) * mm, "end": v(75.2, 193.54) * mm});
            skArc(sketch, "E154", {"start": v(75.2, 193.54) * mm, "mid": v(48.55, 195.12) * mm, "end": v(21.86, 194.62) * mm});
            skArc(sketch, "E155", {"start": v(51.58, 281.5) * mm, "mid": v(36.35, 311.65) * mm, "end": v(9.99, 332.78) * mm});
            skArc(sketch, "E156", {"start": v(-6.27, 325.67) * mm, "mid": v(0.17, 333.3) * mm, "end": v(10.15, 333.12) * mm});
            skArc(sketch, "E157", {"start": v(-8.2, 326.18) * mm, "mid": v(-0.66, 335.12) * mm, "end": v(11.05, 334.9) * mm});
            skArc(sketch, "E158", {"start": v(10.15, 333.12) * mm, "mid": v(36.64, 311.89) * mm, "end": v(51.94, 281.58) * mm});
            skArc(sketch, "E159", {"start": v(11.05, 334.9) * mm, "mid": v(32.2, 319.76) * mm, "end": v(47.56, 298.74) * mm});
            skArc(sketch, "E160", {"start": v(47.56, 298.74) * mm, "mid": v(57.27, 283.9) * mm, "end": v(69.95, 271.5) * mm});
            skArc(sketch, "E161", {"start": v(-7.3, 258.1) * mm, "mid": v(-7.4, 258.43) * mm, "end": v(-7.67, 258.63) * mm});
            skArc(sketch, "E162", {"start": v(-7.68, 258.14) * mm, "mid": v(-7.7, 258.22) * mm, "end": v(-7.77, 258.27) * mm});
            skArc(sketch, "E163", {"start": v(13.63, 189.02) * mm, "mid": v(15.53, 190.02) * mm, "end": v(16.15, 192.07) * mm});
            skLineSegment(sketch, "E164", {"start": v(14.93, 204.51) * mm, "end": v(16.15, 192.07) * mm});
            skLineSegment(sketch, "E165", {"start": v(11.88, 207.01) * mm, "end": v(4.14, 206.25) * mm});
            skLineSegment(sketch, "E166", {"start": v(13.63, 189.02) * mm, "end": v(8.67, 188.57) * mm});
            skArc(sketch, "E167", {"start": v(5.67, 191.04) * mm, "mid": v(6.66, 189.18) * mm, "end": v(8.67, 188.57) * mm});
            skLineSegment(sketch, "E168", {"start": v(7.13, 204.25) * mm, "end": v(12.1, 204.74) * mm});
            skLineSegment(sketch, "E169", {"start": v(7.86, 191.76) * mm, "end": v(7.9, 191.26) * mm});
            skLineSegment(sketch, "E170", {"start": v(13.88, 191.85) * mm, "end": v(13.83, 192.34) * mm});
            skArc(sketch, "E171", {"start": v(8.67, 188.57) * mm, "mid": v(7.02, 188.93) * mm, "end": v(5.9, 190.18) * mm});
            skArc(sketch, "E172", {"start": v(4.35, 204.35) * mm, "mid": v(4.25, 205.3) * mm, "end": v(4.14, 206.25) * mm});
            skArc(sketch, "E173", {"start": v(-2.25, 238.03) * mm, "mid": v(-6.53, 247.97) * mm, "end": v(-7.15, 258.78) * mm, "construction": true});
            skArc(sketch, "E174", {"start": v(-2.25, 238.03) * mm, "mid": v(5.72, 221.98) * mm, "end": v(9.62, 204.5) * mm, "construction": true});
            skArc(sketch, "E175", {"start": v(13.85, 192.1) * mm, "mid": v(16.1, 192.9) * mm, "end": v(17.73, 194.64) * mm, "construction": true});
            skArc(sketch, "E176", {"start": v(13.26, 198.07) * mm, "mid": v(15.52, 198.86) * mm, "end": v(17.14, 200.61) * mm, "construction": true});
            skArc(sketch, "E177", {"start": v(17.73, 194.64) * mm, "mid": v(19.36, 196.39) * mm, "end": v(21.6, 197.18) * mm, "construction": true});
            skArc(sketch, "E178", {"start": v(17.14, 200.61) * mm, "mid": v(18.77, 202.36) * mm, "end": v(21.02, 203.16) * mm, "construction": true});
            skLineSegment(sketch, "E179", {"start": v(21.6, 197.18) * mm, "end": v(41.78, 199.17) * mm, "construction": true});
            skLineSegment(sketch, "E180", {"start": v(21.02, 203.16) * mm, "end": v(31.24, 204.16) * mm, "construction": true});
            skLineSegment(sketch, "E181", {"start": v(30.75, 209.14) * mm, "end": v(20.53, 208.13) * mm, "construction": true});
            skArc(sketch, "E182", {"start": v(31.24, 204.16) * mm, "mid": v(33.48, 206.9) * mm, "end": v(30.75, 209.14) * mm, "construction": true});
            skArc(sketch, "E183", {"start": v(20.53, 208.13) * mm, "mid": v(18.7, 208.69) * mm, "end": v(17.8, 210.37) * mm, "construction": true});
            skLineSegment(sketch, "E184", {"start": v(17.8, 210.37) * mm, "end": v(16.34, 225.17) * mm, "construction": true});
            skArc(sketch, "E185", {"start": v(23.72, 285.12) * mm, "mid": v(-6.02, 259.07) * mm, "end": v(15.88, 226.16) * mm});
            skArc(sketch, "E186", {"start": v(23.72, 225.12) * mm, "mid": v(20.35, 225.3) * mm, "end": v(17.03, 225.88) * mm});
            skArc(sketch, "E187", {"start": v(16.34, 225.17) * mm, "mid": v(16.34, 225.6) * mm, "end": v(16.4, 226.03) * mm, "construction": true});
            skLineSegment(sketch, "E188", {"start": v(13.15, 226.84) * mm, "end": v(19.65, 225.2) * mm, "construction": true});
            skArc(sketch, "E189", {"start": v(23.72, 224.74) * mm, "mid": v(20.31, 224.94) * mm, "end": v(16.94, 225.5) * mm});
            skArc(sketch, "E190", {"start": v(17.03, 225.88) * mm, "mid": v(16.6, 225.78) * mm, "end": v(16.42, 225.38) * mm});
            skArc(sketch, "E191", {"start": v(15.88, 226.16) * mm, "mid": v(16.16, 225.97) * mm, "end": v(16.25, 225.64) * mm});
            skArc(sketch, "E192", {"start": v(16.94, 225.5) * mm, "mid": v(16.84, 225.49) * mm, "end": v(16.8, 225.39) * mm});
            skArc(sketch, "E193", {"start": v(15.78, 225.8) * mm, "mid": v(15.85, 225.75) * mm, "end": v(15.88, 225.67) * mm});
            skLineSegment(sketch, "E194", {"start": v(20.53, 208.13) * mm, "end": v(21.02, 203.16) * mm, "construction": true});
            skArc(sketch, "E195", {"start": v(16.25, 225.64) * mm, "mid": v(16.24, 225.4) * mm, "end": v(16.25, 225.16) * mm});
            skArc(sketch, "E196", {"start": v(16.42, 225.38) * mm, "mid": v(16.42, 225.28) * mm, "end": v(16.43, 225.18) * mm});
            skArc(sketch, "E197", {"start": v(15.88, 225.67) * mm, "mid": v(15.87, 225.4) * mm, "end": v(15.88, 225.13) * mm});
            skLineSegment(sketch, "E198", {"start": v(16.25, 225.16) * mm, "end": v(17.71, 210.37) * mm});
            skLineSegment(sketch, "E199", {"start": v(15.88, 225.13) * mm, "end": v(17.34, 210.33) * mm});
            skLineSegment(sketch, "E200", {"start": v(16.43, 225.18) * mm, "end": v(17.88, 210.38) * mm});
            skArc(sketch, "E201", {"start": v(17.88, 210.38) * mm, "mid": v(18.76, 208.75) * mm, "end": v(20.52, 208.22) * mm});
            skArc(sketch, "E202", {"start": v(18.26, 210.42) * mm, "mid": v(19, 209.04) * mm, "end": v(20.49, 208.6) * mm});
            skArc(sketch, "E203", {"start": v(17.71, 210.37) * mm, "mid": v(18.64, 208.62) * mm, "end": v(20.54, 208.04) * mm});
            skArc(sketch, "E204", {"start": v(17.34, 210.33) * mm, "mid": v(18.4, 208.33) * mm, "end": v(20.58, 207.67) * mm});
            skLineSegment(sketch, "E205", {"start": v(20.52, 208.22) * mm, "end": v(30.74, 209.22) * mm});
            skLineSegment(sketch, "E206", {"start": v(20.49, 208.6) * mm, "end": v(30.7, 209.6) * mm});
            skLineSegment(sketch, "E207", {"start": v(20.54, 208.04) * mm, "end": v(30.76, 209.05) * mm});
            skLineSegment(sketch, "E208", {"start": v(20.58, 207.67) * mm, "end": v(30.8, 208.68) * mm});
            skArc(sketch, "E209", {"start": v(30.8, 208.68) * mm, "mid": v(33.02, 206.85) * mm, "end": v(31.2, 204.62) * mm});
            skArc(sketch, "E210", {"start": v(30.76, 209.05) * mm, "mid": v(33.4, 206.89) * mm, "end": v(31.23, 204.25) * mm});
            skArc(sketch, "E211", {"start": v(30.74, 209.22) * mm, "mid": v(33.57, 206.9) * mm, "end": v(31.25, 204.07) * mm});
            skArc(sketch, "E212", {"start": v(30.7, 209.6) * mm, "mid": v(33.94, 206.94) * mm, "end": v(31.28, 203.7) * mm});
            skLineSegment(sketch, "E213", {"start": v(31.25, 204.07) * mm, "end": v(21.03, 203.07) * mm});
            skLineSegment(sketch, "E214", {"start": v(31.28, 203.7) * mm, "end": v(21.07, 202.7) * mm});
            skLineSegment(sketch, "E215", {"start": v(31.23, 204.25) * mm, "end": v(21.01, 203.24) * mm});
            skLineSegment(sketch, "E216", {"start": v(31.2, 204.62) * mm, "end": v(20.98, 203.62) * mm});
            skArc(sketch, "E217", {"start": v(21.07, 202.7) * mm, "mid": v(19.02, 201.97) * mm, "end": v(17.55, 200.39) * mm});
            skArc(sketch, "E218", {"start": v(21.03, 203.07) * mm, "mid": v(18.82, 202.29) * mm, "end": v(17.22, 200.57) * mm});
            skArc(sketch, "E219", {"start": v(21.01, 203.24) * mm, "mid": v(18.72, 202.43) * mm, "end": v(17.07, 200.65) * mm});
            skArc(sketch, "E220", {"start": v(20.98, 203.62) * mm, "mid": v(18.52, 202.75) * mm, "end": v(16.74, 200.84) * mm});
            skArc(sketch, "E221", {"start": v(16.74, 200.84) * mm, "mid": v(15.45, 199.38) * mm, "end": v(13.66, 198.6) * mm});
            skArc(sketch, "E222", {"start": v(17.07, 200.65) * mm, "mid": v(15.67, 199.07) * mm, "end": v(13.73, 198.23) * mm});
            skArc(sketch, "E223", {"start": v(17.22, 200.57) * mm, "mid": v(15.73, 198.9) * mm, "end": v(13.68, 198.04) * mm});
            skArc(sketch, "E224", {"start": v(17.55, 200.39) * mm, "mid": v(15.95, 198.6) * mm, "end": v(13.74, 197.67) * mm});
            skArc(sketch, "E225", {"start": v(23.72, 286.12) * mm, "mid": v(-3.56, 269.83) * mm, "end": v(-2.18, 238.08) * mm});
            skArc(sketch, "E226", {"start": v(-7.3, 258.1) * mm, "mid": v(-6.54, 247.62) * mm, "end": v(-2.32, 237.99) * mm});
            skArc(sketch, "E227", {"start": v(-7.68, 258.14) * mm, "mid": v(-6.9, 247.53) * mm, "end": v(-2.64, 237.78) * mm});
            skArc(sketch, "E228", {"start": v(-2.18, 238.08) * mm, "mid": v(5.72, 222.25) * mm, "end": v(9.65, 205) * mm});
            skArc(sketch, "E229", {"start": v(-1.86, 238.29) * mm, "mid": v(6.07, 222.37) * mm, "end": v(10.03, 205.03) * mm});
            skArc(sketch, "E230", {"start": v(-2.32, 237.99) * mm, "mid": v(5.55, 222.2) * mm, "end": v(9.48, 204.98) * mm});
            skArc(sketch, "E231", {"start": v(-2.64, 237.78) * mm, "mid": v(5.2, 222.06) * mm, "end": v(9.1, 204.94) * mm});
            skArc(sketch, "E232", {"start": v(32.24, 221.21) * mm, "mid": v(34.69, 219.02) * mm, "end": v(37.35, 217.1) * mm});
            skArc(sketch, "E233", {"start": v(32.5, 221.48) * mm, "mid": v(34.92, 219.32) * mm, "end": v(37.55, 217.42) * mm});
            skArc(sketch, "E234", {"start": v(74.94, 263.9) * mm, "mid": v(77.46, 224.35) * mm, "end": v(38.56, 216.8) * mm});
            skArc(sketch, "E235", {"start": v(38, 217.14) * mm, "mid": v(37.7, 216.4) * mm, "end": v(37.65, 215.58) * mm, "construction": true});
            skLineSegment(sketch, "E236", {"start": v(44.5, 213.14) * mm, "end": v(31.5, 221.14) * mm, "construction": true});
            skArc(sketch, "E237", {"start": v(37.55, 217.42) * mm, "mid": v(37.76, 217.15) * mm, "end": v(37.74, 216.81) * mm});
            skArc(sketch, "E238", {"start": v(38.56, 216.8) * mm, "mid": v(38.12, 216.84) * mm, "end": v(37.82, 216.52) * mm});
            skArc(sketch, "E239", {"start": v(37.35, 217.1) * mm, "mid": v(37.4, 217.04) * mm, "end": v(37.4, 216.96) * mm});
            skArc(sketch, "E240", {"start": v(38.37, 216.48) * mm, "mid": v(38.26, 216.5) * mm, "end": v(38.18, 216.41) * mm});
            skArc(sketch, "E241", {"start": v(37.82, 216.52) * mm, "mid": v(37.73, 216.06) * mm, "end": v(37.74, 215.6) * mm});
            skArc(sketch, "E242", {"start": v(38.18, 216.41) * mm, "mid": v(38.1, 216.02) * mm, "end": v(38.1, 215.63) * mm});
            skArc(sketch, "E243", {"start": v(37.74, 216.81) * mm, "mid": v(37.58, 216.2) * mm, "end": v(37.56, 215.58) * mm});
            skArc(sketch, "E244", {"start": v(37.4, 216.96) * mm, "mid": v(37.2, 216.26) * mm, "end": v(37.19, 215.54) * mm});
            skLineSegment(sketch, "E245", {"start": v(37.65, 215.58) * mm, "end": v(38.55, 206.39) * mm, "construction": true});
            skLineSegment(sketch, "E246", {"start": v(33.48, 206.9) * mm, "end": v(38.46, 207.38) * mm, "construction": true});
            skArc(sketch, "E247", {"start": v(38.55, 206.39) * mm, "mid": v(39.46, 204.7) * mm, "end": v(41.29, 204.15) * mm, "construction": true});
            skLineSegment(sketch, "E248", {"start": v(41.29, 204.15) * mm, "end": v(43.84, 204.4) * mm, "construction": true});
            skArc(sketch, "E249", {"start": v(43.84, 204.4) * mm, "mid": v(46.57, 202.15) * mm, "end": v(44.33, 199.42) * mm, "construction": true});
            skLineSegment(sketch, "E250", {"start": v(41.29, 204.15) * mm, "end": v(41.78, 199.17) * mm, "construction": true});
            skLineSegment(sketch, "E251", {"start": v(41.78, 199.17) * mm, "end": v(44.33, 199.42) * mm, "construction": true});
            skLineSegment(sketch, "E252", {"start": v(37.56, 215.58) * mm, "end": v(38.47, 206.38) * mm});
            skLineSegment(sketch, "E253", {"start": v(38.1, 206.34) * mm, "end": v(37.19, 215.54) * mm});
            skLineSegment(sketch, "E254", {"start": v(38.64, 206.4) * mm, "end": v(37.74, 215.6) * mm});
            skLineSegment(sketch, "E255", {"start": v(39.01, 206.43) * mm, "end": v(38.1, 215.63) * mm});
            skArc(sketch, "E256", {"start": v(38.64, 206.4) * mm, "mid": v(39.51, 204.77) * mm, "end": v(41.28, 204.23) * mm});
            skArc(sketch, "E257", {"start": v(39.01, 206.43) * mm, "mid": v(39.75, 205.06) * mm, "end": v(41.24, 204.6) * mm});
            skArc(sketch, "E258", {"start": v(38.47, 206.38) * mm, "mid": v(39.4, 204.63) * mm, "end": v(41.3, 204.06) * mm});
            skArc(sketch, "E259", {"start": v(38.1, 206.34) * mm, "mid": v(39.16, 204.34) * mm, "end": v(41.33, 203.69) * mm});
            skLineSegment(sketch, "E260", {"start": v(41.24, 204.6) * mm, "end": v(43.8, 204.86) * mm});
            skLineSegment(sketch, "E261", {"start": v(43.83, 204.48) * mm, "end": v(41.28, 204.23) * mm});
            skLineSegment(sketch, "E262", {"start": v(43.85, 204.31) * mm, "end": v(41.3, 204.06) * mm});
            skLineSegment(sketch, "E263", {"start": v(43.89, 203.94) * mm, "end": v(41.33, 203.69) * mm});
            skArc(sketch, "E264", {"start": v(43.89, 203.94) * mm, "mid": v(46.11, 202.1) * mm, "end": v(44.29, 199.88) * mm});
            skArc(sketch, "E265", {"start": v(43.85, 204.31) * mm, "mid": v(46.49, 202.15) * mm, "end": v(44.32, 199.5) * mm});
            skArc(sketch, "E266", {"start": v(43.83, 204.48) * mm, "mid": v(46.66, 202.16) * mm, "end": v(44.34, 199.33) * mm});
            skArc(sketch, "E267", {"start": v(43.8, 204.86) * mm, "mid": v(47.03, 202.2) * mm, "end": v(44.38, 198.96) * mm});
            skLineSegment(sketch, "E268", {"start": v(21.56, 197.64) * mm, "end": v(44.29, 199.88) * mm});
            skLineSegment(sketch, "E269", {"start": v(21.6, 197.27) * mm, "end": v(44.32, 199.5) * mm});
            skLineSegment(sketch, "E270", {"start": v(21.62, 197.1) * mm, "end": v(44.34, 199.33) * mm});
            skLineSegment(sketch, "E271", {"start": v(21.65, 196.72) * mm, "end": v(44.38, 198.96) * mm});
            skArc(sketch, "E272", {"start": v(21.6, 197.27) * mm, "mid": v(19.3, 196.46) * mm, "end": v(17.65, 194.68) * mm});
            skArc(sketch, "E273", {"start": v(21.62, 197.1) * mm, "mid": v(19.4, 196.32) * mm, "end": v(17.8, 194.6) * mm});
            skArc(sketch, "E274", {"start": v(21.65, 196.72) * mm, "mid": v(19.61, 196) * mm, "end": v(18.13, 194.42) * mm});
            skArc(sketch, "E275", {"start": v(21.56, 197.64) * mm, "mid": v(19.1, 196.78) * mm, "end": v(17.33, 194.86) * mm});
            skArc(sketch, "E276", {"start": v(18.13, 194.42) * mm, "mid": v(16.54, 192.63) * mm, "end": v(14.33, 191.7) * mm});
            skArc(sketch, "E277", {"start": v(17.8, 194.6) * mm, "mid": v(16.32, 192.93) * mm, "end": v(14.26, 192.07) * mm});
            skArc(sketch, "E278", {"start": v(17.65, 194.68) * mm, "mid": v(16.25, 193.1) * mm, "end": v(14.32, 192.25) * mm});
            skArc(sketch, "E279", {"start": v(17.33, 194.86) * mm, "mid": v(16.03, 193.4) * mm, "end": v(14.25, 192.62) * mm});
            skPoint(sketch, "E280.visualSharp", {"position": v(51.82, 280.53) * mm});
            skArc(sketch, "E280.filletArc", {"start": v(50.9, 280.9) * mm, "mid": v(51.42, 280.99) * mm, "end": v(51.58, 281.5) * mm});
            skPoint(sketch, "E281.visualSharp", {"position": v(50.98, 279.8) * mm});
            skArc(sketch, "E281.filletArc", {"start": v(50.78, 279.33) * mm, "mid": v(50.78, 279.71) * mm, "end": v(50.5, 279.98) * mm});
            skPoint(sketch, "E282.visualSharp", {"position": v(51.9, 279.41) * mm});
            skArc(sketch, "E282.filletArc", {"start": v(52.37, 279.21) * mm, "mid": v(51.98, 279.22) * mm, "end": v(51.7, 278.95) * mm});
            skPoint(sketch, "E283.visualSharp", {"position": v(28.01, 224.36) * mm});
            skArc(sketch, "E283.filletArc", {"start": v(27.58, 224.5) * mm, "mid": v(27.94, 224.53) * mm, "end": v(28.2, 224.8) * mm});
            skPoint(sketch, "E284.visualSharp", {"position": v(28.94, 223.97) * mm});
            skArc(sketch, "E284.filletArc", {"start": v(29.12, 224.4) * mm, "mid": v(29.1, 224.04) * mm, "end": v(29.35, 223.77) * mm});
            skArc(sketch, "E285", {"start": v(27.46, 224.15) * mm, "mid": v(28.1, 224.19) * mm, "end": v(28.54, 224.65) * mm});
            skArc(sketch, "E286", {"start": v(29.18, 223.44) * mm, "mid": v(28.76, 223.91) * mm, "end": v(28.77, 224.55) * mm});
            skArc(sketch, "E287", {"start": v(50.64, 280.33) * mm, "mid": v(51.13, 279.86) * mm, "end": v(51.13, 279.19) * mm});
            skArc(sketch, "E288", {"start": v(51.36, 279.09) * mm, "mid": v(51.84, 279.57) * mm, "end": v(52.51, 279.56) * mm});
            skArc(sketch, "E289", {"start": v(51.94, 281.58) * mm, "mid": v(51.67, 280.7) * mm, "end": v(50.77, 280.55) * mm});
            skArc(sketch, "E290", {"start": v(-5.91, 325.56) * mm, "mid": v(0.32, 332.95) * mm, "end": v(9.99, 332.78) * mm});
            skLineSegment(sketch, "E291", {"start": v(13.29, 197.82) * mm, "end": v(13.24, 198.32) * mm});
            skArc(sketch, "E292", {"start": v(11.88, 207.01) * mm, "mid": v(13.92, 206.4) * mm, "end": v(14.93, 204.51) * mm});
            skPoint(sketch, "E293.visualSharp", {"position": v(6.63, 204.2) * mm});
            skArc(sketch, "E293.filletArc", {"start": v(7.13, 204.25) * mm, "mid": v(6.8, 204.07) * mm, "end": v(6.68, 203.7) * mm});
            skPoint(sketch, "E294.visualSharp", {"position": v(12.6, 204.78) * mm});
            skArc(sketch, "E294.filletArc", {"start": v(12.65, 204.29) * mm, "mid": v(12.47, 204.62) * mm, "end": v(12.1, 204.74) * mm});
            skPoint(sketch, "E295.visualSharp", {"position": v(6.78, 202.7) * mm});
            skArc(sketch, "E295.filletArc", {"start": v(6.73, 203.2) * mm, "mid": v(6.9, 202.86) * mm, "end": v(7.28, 202.75) * mm});
            skPoint(sketch, "E296.visualSharp", {"position": v(12.75, 203.3) * mm});
            skArc(sketch, "E296.filletArc", {"start": v(12.25, 203.24) * mm, "mid": v(12.59, 203.42) * mm, "end": v(12.7, 203.79) * mm});
            skPoint(sketch, "E297.visualSharp", {"position": v(6.93, 201.21) * mm});
            skArc(sketch, "E297.filletArc", {"start": v(7.42, 201.26) * mm, "mid": v(7.09, 201.08) * mm, "end": v(6.97, 200.71) * mm});
            skPoint(sketch, "E298.visualSharp", {"position": v(12.9, 201.8) * mm});
            skArc(sketch, "E298.filletArc", {"start": v(12.95, 201.3) * mm, "mid": v(12.76, 201.64) * mm, "end": v(12.4, 201.75) * mm});
            skPoint(sketch, "E299.visualSharp", {"position": v(7.07, 199.72) * mm});
            skArc(sketch, "E299.filletArc", {"start": v(7.02, 200.22) * mm, "mid": v(7.2, 199.88) * mm, "end": v(7.57, 199.77) * mm});
            skPoint(sketch, "E300.visualSharp", {"position": v(13.04, 200.3) * mm});
            skArc(sketch, "E300.filletArc", {"start": v(12.55, 200.26) * mm, "mid": v(12.88, 200.44) * mm, "end": v(13, 200.8) * mm});
            skPoint(sketch, "E301.visualSharp", {"position": v(7.22, 198.23) * mm});
            skArc(sketch, "E301.filletArc", {"start": v(7.72, 198.27) * mm, "mid": v(7.38, 198.1) * mm, "end": v(7.27, 197.73) * mm});
            skPoint(sketch, "E302.visualSharp", {"position": v(13.2, 198.81) * mm});
            skArc(sketch, "E302.filletArc", {"start": v(13.24, 198.32) * mm, "mid": v(13.06, 198.65) * mm, "end": v(12.7, 198.76) * mm});
            skPoint(sketch, "E303.visualSharp", {"position": v(7.37, 196.73) * mm});
            skArc(sketch, "E303.filletArc", {"start": v(7.32, 197.23) * mm, "mid": v(7.5, 196.9) * mm, "end": v(7.86, 196.78) * mm});
            skPoint(sketch, "E304.visualSharp", {"position": v(13.34, 197.32) * mm});
            skArc(sketch, "E304.filletArc", {"start": v(12.84, 197.27) * mm, "mid": v(13.18, 197.45) * mm, "end": v(13.29, 197.82) * mm});
            skPoint(sketch, "E305.visualSharp", {"position": v(7.51, 195.24) * mm});
            skArc(sketch, "E305.filletArc", {"start": v(8.01, 195.29) * mm, "mid": v(7.67, 195.1) * mm, "end": v(7.56, 194.74) * mm});
            skPoint(sketch, "E306.visualSharp", {"position": v(13.48, 195.83) * mm});
            skArc(sketch, "E306.filletArc", {"start": v(13.53, 195.33) * mm, "mid": v(13.35, 195.67) * mm, "end": v(12.99, 195.78) * mm});
            skPoint(sketch, "E307.visualSharp", {"position": v(7.66, 193.75) * mm});
            skArc(sketch, "E307.filletArc", {"start": v(7.61, 194.24) * mm, "mid": v(7.8, 193.9) * mm, "end": v(8.16, 193.8) * mm});
            skPoint(sketch, "E308.visualSharp", {"position": v(13.63, 194.34) * mm});
            skArc(sketch, "E308.filletArc", {"start": v(13.13, 194.29) * mm, "mid": v(13.47, 194.47) * mm, "end": v(13.58, 194.83) * mm});
            skPoint(sketch, "E309.visualSharp", {"position": v(7.8, 192.25) * mm});
            skArc(sketch, "E309.filletArc", {"start": v(8.3, 192.3) * mm, "mid": v(7.97, 192.12) * mm, "end": v(7.86, 191.76) * mm});
            skPoint(sketch, "E310.visualSharp", {"position": v(13.78, 192.84) * mm});
            skArc(sketch, "E310.filletArc", {"start": v(13.83, 192.34) * mm, "mid": v(13.65, 192.68) * mm, "end": v(13.28, 192.8) * mm});
            skPoint(sketch, "E311.visualSharp", {"position": v(13.93, 191.35) * mm});
            skArc(sketch, "E311.filletArc", {"start": v(13.43, 191.3) * mm, "mid": v(13.77, 191.48) * mm, "end": v(13.88, 191.85) * mm});
            skPoint(sketch, "E312.visualSharp", {"position": v(7.95, 190.76) * mm});
            skArc(sketch, "E312.filletArc", {"start": v(7.9, 191.26) * mm, "mid": v(8.09, 190.92) * mm, "end": v(8.45, 190.81) * mm});
            skLineSegment(sketch, "E313", {"start": v(12.7, 203.79) * mm, "end": v(12.65, 204.29) * mm});
            skLineSegment(sketch, "E314", {"start": v(12.1, 204.74) * mm, "end": v(10.2, 204.55) * mm});
            skLineSegment(sketch, "E315", {"start": v(9.03, 204.43) * mm, "end": v(7.13, 204.25) * mm});
            skLineSegment(sketch, "E316", {"start": v(12.55, 200.26) * mm, "end": v(7.57, 199.77) * mm});
            skLineSegment(sketch, "E317", {"start": v(7.02, 200.22) * mm, "end": v(6.97, 200.71) * mm});
            skLineSegment(sketch, "E318", {"start": v(13.13, 194.29) * mm, "end": v(8.16, 193.8) * mm});
            skLineSegment(sketch, "E319", {"start": v(7.61, 194.24) * mm, "end": v(7.56, 194.74) * mm});
            skArc(sketch, "E320", {"start": v(13.78, 192.52) * mm, "mid": v(13.57, 192.73) * mm, "end": v(13.28, 192.8) * mm});
            skArc(sketch, "E321", {"start": v(13.43, 191.3) * mm, "mid": v(13.7, 191.42) * mm, "end": v(13.87, 191.69) * mm});
            skArc(sketch, "E322", {"start": v(7.56, 194.74) * mm, "mid": v(7.67, 195.1) * mm, "end": v(8.01, 195.29) * mm});
            skArc(sketch, "E323", {"start": v(12.99, 195.78) * mm, "mid": v(13.35, 195.67) * mm, "end": v(13.53, 195.33) * mm});
            skArc(sketch, "E324", {"start": v(13.58, 194.83) * mm, "mid": v(13.47, 194.47) * mm, "end": v(13.13, 194.29) * mm});
            skArc(sketch, "E325", {"start": v(7.86, 196.78) * mm, "mid": v(7.5, 196.9) * mm, "end": v(7.32, 197.23) * mm});
            skArc(sketch, "E326", {"start": v(7.27, 197.73) * mm, "mid": v(7.38, 198.1) * mm, "end": v(7.72, 198.27) * mm});
            skArc(sketch, "E327", {"start": v(13.19, 198.5) * mm, "mid": v(12.98, 198.7) * mm, "end": v(12.7, 198.76) * mm});
            skArc(sketch, "E328", {"start": v(12.84, 197.27) * mm, "mid": v(13.12, 197.4) * mm, "end": v(13.28, 197.66) * mm});
            skArc(sketch, "E329", {"start": v(7.57, 199.77) * mm, "mid": v(7.2, 199.88) * mm, "end": v(7.02, 200.22) * mm});
            skArc(sketch, "E330", {"start": v(6.97, 200.71) * mm, "mid": v(7.09, 201.08) * mm, "end": v(7.42, 201.26) * mm});
            skArc(sketch, "E331", {"start": v(12.4, 201.75) * mm, "mid": v(12.76, 201.64) * mm, "end": v(12.95, 201.3) * mm});
            skArc(sketch, "E332", {"start": v(13, 200.8) * mm, "mid": v(12.88, 200.44) * mm, "end": v(12.55, 200.26) * mm});
            skArc(sketch, "E333", {"start": v(7.28, 202.75) * mm, "mid": v(6.9, 202.86) * mm, "end": v(6.73, 203.2) * mm});
            skArc(sketch, "E334", {"start": v(6.68, 203.7) * mm, "mid": v(6.8, 204.07) * mm, "end": v(7.13, 204.25) * mm});
            skArc(sketch, "E335", {"start": v(12.1, 204.74) * mm, "mid": v(12.47, 204.62) * mm, "end": v(12.65, 204.29) * mm});
            skArc(sketch, "E336", {"start": v(12.7, 203.79) * mm, "mid": v(12.59, 203.42) * mm, "end": v(12.25, 203.24) * mm});
            skArc(sketch, "E337", {"start": v(10.2, 204.55) * mm, "mid": v(9.83, 204.66) * mm, "end": v(9.65, 205) * mm});
            skArc(sketch, "E338", {"start": v(9.03, 204.43) * mm, "mid": v(9.37, 204.61) * mm, "end": v(9.48, 204.98) * mm});
            skArc(sketch, "E339", {"start": v(13.78, 192.52) * mm, "mid": v(14, 192.3) * mm, "end": v(14.32, 192.25) * mm});
            skArc(sketch, "E340", {"start": v(13.87, 191.69) * mm, "mid": v(14, 191.94) * mm, "end": v(14.26, 192.07) * mm});
            skArc(sketch, "E341", {"start": v(14.25, 192.62) * mm, "mid": v(14.17, 192.63) * mm, "end": v(14.11, 192.69) * mm});
            skArc(sketch, "E342", {"start": v(14.33, 191.7) * mm, "mid": v(14.27, 191.66) * mm, "end": v(14.23, 191.6) * mm});
            skArc(sketch, "E343", {"start": v(14.23, 191.6) * mm, "mid": v(13.96, 191.14) * mm, "end": v(13.46, 190.93) * mm});
            skArc(sketch, "E344", {"start": v(14.11, 192.69) * mm, "mid": v(13.75, 193.06) * mm, "end": v(13.24, 193.17) * mm});
            skArc(sketch, "E345", {"start": v(7.48, 191.72) * mm, "mid": v(7.68, 192.36) * mm, "end": v(8.27, 192.68) * mm});
            skArc(sketch, "E346", {"start": v(8.49, 190.44) * mm, "mid": v(7.85, 190.63) * mm, "end": v(7.53, 191.22) * mm});
            skArc(sketch, "E347", {"start": v(9.1, 204.94) * mm, "mid": v(9.08, 204.85) * mm, "end": v(9, 204.8) * mm});
            skArc(sketch, "E348", {"start": v(10.03, 205.03) * mm, "mid": v(10.07, 204.95) * mm, "end": v(10.16, 204.92) * mm});
            skArc(sketch, "E349", {"start": v(12.07, 205.1) * mm, "mid": v(12.7, 204.91) * mm, "end": v(13.02, 204.32) * mm});
            skArc(sketch, "E350", {"start": v(13.07, 203.83) * mm, "mid": v(12.88, 203.19) * mm, "end": v(12.29, 202.87) * mm});
            skArc(sketch, "E351", {"start": v(7.1, 204.62) * mm, "mid": v(6.5, 204.3) * mm, "end": v(6.3, 203.66) * mm});
            skArc(sketch, "E352", {"start": v(6.36, 203.16) * mm, "mid": v(6.67, 202.57) * mm, "end": v(7.31, 202.38) * mm});
            skLineSegment(sketch, "E353", {"start": v(7.1, 204.62) * mm, "end": v(9, 204.8) * mm});
            skLineSegment(sketch, "E354", {"start": v(10.16, 204.92) * mm, "end": v(12.07, 205.1) * mm});
            skLineSegment(sketch, "E355", {"start": v(13.02, 204.32) * mm, "end": v(13.07, 203.83) * mm});
            skLineSegment(sketch, "E356", {"start": v(12.29, 202.87) * mm, "end": v(7.31, 202.38) * mm});
            skLineSegment(sketch, "E357", {"start": v(6.36, 203.16) * mm, "end": v(6.3, 203.66) * mm});
            skLineSegment(sketch, "E358", {"start": v(8.27, 192.68) * mm, "end": v(13.24, 193.17) * mm});
            skLineSegment(sketch, "E359", {"start": v(7.48, 191.72) * mm, "end": v(7.53, 191.22) * mm});
            skLineSegment(sketch, "E360", {"start": v(8.49, 190.44) * mm, "end": v(13.46, 190.93) * mm});
            skArc(sketch, "E361", {"start": v(13.66, 198.6) * mm, "mid": v(13.58, 198.6) * mm, "end": v(13.52, 198.66) * mm});
            skArc(sketch, "E362", {"start": v(13.74, 197.67) * mm, "mid": v(13.68, 197.63) * mm, "end": v(13.64, 197.57) * mm});
            skArc(sketch, "E363", {"start": v(13.64, 197.57) * mm, "mid": v(13.37, 197.11) * mm, "end": v(12.88, 196.9) * mm});
            skArc(sketch, "E364", {"start": v(13.52, 198.66) * mm, "mid": v(13.16, 199.03) * mm, "end": v(12.66, 199.14) * mm});
            skArc(sketch, "E365", {"start": v(7.68, 198.65) * mm, "mid": v(7.09, 198.33) * mm, "end": v(6.9, 197.7) * mm});
            skArc(sketch, "E366", {"start": v(6.94, 197.2) * mm, "mid": v(7.26, 196.6) * mm, "end": v(7.9, 196.4) * mm});
            skLineSegment(sketch, "E367", {"start": v(7.68, 198.65) * mm, "end": v(12.66, 199.14) * mm});
            skLineSegment(sketch, "E368", {"start": v(6.9, 197.7) * mm, "end": v(6.94, 197.2) * mm});
            skLineSegment(sketch, "E369", {"start": v(7.9, 196.4) * mm, "end": v(12.88, 196.9) * mm});
            skArc(sketch, "E370", {"start": v(13.19, 198.5) * mm, "mid": v(13.42, 198.27) * mm, "end": v(13.73, 198.23) * mm});
            skArc(sketch, "E371", {"start": v(13.28, 197.66) * mm, "mid": v(13.42, 197.9) * mm, "end": v(13.68, 198.04) * mm});
            skArc(sketch, "E372", {"start": v(16.8, 225.39) * mm, "mid": v(16.8, 225.3) * mm, "end": v(16.8, 225.22) * mm});
            skLineSegment(sketch, "E373", {"start": v(16.8, 225.22) * mm, "end": v(18.26, 210.42) * mm});
            skLineSegment(sketch, "E374", {"start": v(4.35, 204.35) * mm, "end": v(12.07, 205.1) * mm});
            skLineSegment(sketch, "E375", {"start": v(13.02, 204.32) * mm, "end": v(14.25, 191.88) * mm});
            skLineSegment(sketch, "E376", {"start": v(13.46, 190.93) * mm, "end": v(5.9, 190.18) * mm});
            skArc(sketch, "E377", {"start": v(13.46, 190.93) * mm, "mid": v(14.06, 191.24) * mm, "end": v(14.25, 191.88) * mm});
            skArc(sketch, "E378", {"start": v(-5.91, 325.56) * mm, "mid": v(-10.7, 292.4) * mm, "end": v(-8.01, 259.02) * mm});
            skArc(sketch, "E379", {"start": v(-7.03, 259.05) * mm, "mid": v(3.24, 278.39) * mm, "end": v(23.72, 286.12) * mm});
            skPoint(sketch, "E380.visualSharp", {"position": v(-7.28, 255.45) * mm});
            skArc(sketch, "E380.filletArc", {"start": v(-8.01, 259.02) * mm, "mid": v(-7.5, 258.61) * mm, "end": v(-7.03, 259.05) * mm});
            skArc(sketch, "E381", {"start": v(-8.38, 258.94) * mm, "mid": v(-8.17, 258.52) * mm, "end": v(-7.77, 258.27) * mm});
            skSolve(sketch);
        }
        {
            var Q0;
            Q0=qCreatedBy(makeId("Top.planeOp"),FACE);
            var sketch = newSketch(context, id + "F12", { "sketchPlane" : qUnion([Q0])});
            skLineSegment(sketch, "E382", {"start": v(36.66, 121.75) * mm, "end": v(40.78, 163.53) * mm, "construction": true});
            skLineSegment(sketch, "E383", {"start": v(43.14, 192.55) * mm, "end": v(33.72, 96.93) * mm});
            skArc(sketch, "E384", {"start": v(11.66, 121.75) * mm, "mid": v(17.97, 105.15) * mm, "end": v(33.72, 96.93) * mm});
            skLineSegment(sketch, "E385", {"start": v(11.66, 121.75) * mm, "end": v(11.66, 163.53) * mm});
            skPoint(sketch, "E386", {"position": v(38.72, 142.64) * mm});
            skArc(sketch, "E387", {"start": v(11.66, 163.53) * mm, "mid": v(21.04, 184.94) * mm, "end": v(43.14, 192.55) * mm});
            skLineSegment(sketch, "E388.MirrorCS", {"start": v(44.13, 192.45) * mm, "end": v(34.71, 96.83) * mm});
            skArc(sketch, "E389.MirrorCS", {"start": v(61.18, 116.88) * mm, "mid": v(51.76, 101.82) * mm, "end": v(34.71, 96.83) * mm});
            skLineSegment(sketch, "E390.MirrorCS", {"start": v(61.18, 116.88) * mm, "end": v(69.34, 157.85) * mm});
            skArc(sketch, "E391.MirrorCS", {"start": v(69.34, 157.85) * mm, "mid": v(64.31, 180.68) * mm, "end": v(44.13, 192.45) * mm});
            skLineSegment(sketch, "E392", {"start": v(34.21, 96.87) * mm, "end": v(43.63, 192.5) * mm, "construction": true});
            skSolve(sketch);
        }
        {
            var Q0;
            Q0=qCreatedBy(makeId("Top.planeOp"),FACE);
            var sketch = newSketch(context, id + "F13", { "sketchPlane" : qUnion([Q0])});
            skArc(sketch, "E393", {"start": v(11.76, 123.99) * mm, "mid": v(34.43, 96.85) * mm, "end": v(61.56, 119.52) * mm});
            skLineSegment(sketch, "E394", {"start": v(11.76, 123.99) * mm, "end": v(61.56, 119.52) * mm, "construction": true});
            skArc(sketch, "E395", {"start": v(25.94, 152.99) * mm, "mid": v(16.17, 139.8) * mm, "end": v(11.76, 123.99) * mm});
            skArc(sketch, "E396", {"start": v(52.78, 150.58) * mm, "mid": v(39.9, 157.78) * mm, "end": v(25.94, 152.99) * mm});
            skArc(sketch, "E397", {"start": v(61.56, 119.52) * mm, "mid": v(60.04, 135.86) * mm, "end": v(52.78, 150.58) * mm});
            skLineSegment(sketch, "E398", {"start": v(36.66, 121.75) * mm, "end": v(39.9, 157.78) * mm, "construction": true});
            skSolve(sketch);
        }
        {
            var Q0;
            Q0=qCreatedBy(makeId("Top.planeOp"),FACE);
            var sketch = newSketch(context, id + "F14", { "sketchPlane" : qUnion([Q0])});
            skArc(sketch, "E399", {"start": v(11.76, 123.99) * mm, "mid": v(34.43, 96.85) * mm, "end": v(61.56, 119.52) * mm});
            skArc(sketch, "E400", {"start": v(11.76, 123.99) * mm, "mid": v(15.88, 139.18) * mm, "end": v(24.95, 152.04) * mm});
            skArc(sketch, "E401", {"start": v(61.56, 119.52) * mm, "mid": v(60.04, 135.86) * mm, "end": v(52.78, 150.58) * mm});
            skArc(sketch, "E402", {"start": v(52.78, 150.58) * mm, "mid": v(39.9, 157.78) * mm, "end": v(25.94, 152.99) * mm});
            skArc(sketch, "E403", {"start": v(25.94, 152.99) * mm, "mid": v(25.87, 152.92) * mm, "end": v(25.8, 152.86) * mm});
            skArc(sketch, "E404", {"start": v(11.4, 124.02) * mm, "mid": v(34.4, 96.48) * mm, "end": v(61.94, 119.48) * mm});
            skArc(sketch, "E405", {"start": v(9.29, 121.75) * mm, "mid": v(33.98, 94.5) * mm, "end": v(63.51, 116.41) * mm});
            skArc(sketch, "E406", {"start": v(61.94, 119.48) * mm, "mid": v(60.4, 135.96) * mm, "end": v(53.08, 150.8) * mm});
            skArc(sketch, "E407", {"start": v(53.08, 150.8) * mm, "mid": v(39.93, 158.15) * mm, "end": v(25.68, 153.26) * mm});
            skArc(sketch, "E408", {"start": v(11.4, 124.02) * mm, "mid": v(15.54, 139.34) * mm, "end": v(24.69, 152.3) * mm});
            skArc(sketch, "E409", {"start": v(25.68, 153.26) * mm, "mid": v(25.62, 153.2) * mm, "end": v(25.55, 153.13) * mm});
            skLineSegment(sketch, "E410", {"start": v(16.24, 143.6) * mm, "end": v(34.44, 161.23) * mm, "construction": true});
            skLineSegment(sketch, "E411.top", {"start": v(14.87, 176.7) * mm, "end": v(9.89, 176.21) * mm});
            skLineSegment(sketch, "E411.left", {"start": v(15.46, 175.75) * mm, "end": v(15.41, 176.25) * mm});
            skLineSegment(sketch, "E412", {"start": v(15.05, 174.83) * mm, "end": v(13.15, 174.65) * mm});
            skLineSegment(sketch, "E413", {"start": v(9.85, 176.58) * mm, "end": v(14.83, 177.07) * mm});
            skLineSegment(sketch, "E414", {"start": v(15.79, 176.29) * mm, "end": v(15.83, 175.8) * mm});
            skLineSegment(sketch, "E415", {"start": v(9.12, 175.13) * mm, "end": v(9.07, 175.63) * mm});
            skLineSegment(sketch, "E416", {"start": v(9.5, 175.17) * mm, "end": v(9.44, 175.66) * mm});
            skLineSegment(sketch, "E417", {"start": v(10.07, 174.34) * mm, "end": v(11.98, 174.53) * mm});
            skLineSegment(sketch, "E418.bottom", {"start": v(14.72, 178.2) * mm, "end": v(9.74, 177.7) * mm});
            skLineSegment(sketch, "E418.top", {"start": v(14.57, 179.69) * mm, "end": v(9.6, 179.2) * mm});
            skLineSegment(sketch, "E418.left", {"start": v(15.17, 178.74) * mm, "end": v(15.12, 179.24) * mm});
            skLineSegment(sketch, "E418.right", {"start": v(9.2, 178.15) * mm, "end": v(9.15, 178.65) * mm});
            skLineSegment(sketch, "E419.bottom", {"start": v(14.42, 181.18) * mm, "end": v(9.45, 180.69) * mm});
            skLineSegment(sketch, "E419.top", {"start": v(14.28, 182.67) * mm, "end": v(9.3, 182.18) * mm});
            skLineSegment(sketch, "E419.left", {"start": v(14.87, 181.73) * mm, "end": v(14.82, 182.22) * mm});
            skLineSegment(sketch, "E419.right", {"start": v(8.9, 181.14) * mm, "end": v(8.85, 181.63) * mm});
            skArc(sketch, "E420", {"start": v(8.94, 184.58) * mm, "mid": v(7.09, 183.59) * mm, "end": v(6.47, 181.57) * mm});
            skLineSegment(sketch, "E421", {"start": v(6.47, 181.57) * mm, "end": v(7.21, 174.06) * mm});
            skArc(sketch, "E422", {"start": v(8.94, 184.58) * mm, "mid": v(41.47, 186.15) * mm, "end": v(74, 184.58) * mm, "construction": true});
            skArc(sketch, "E423", {"start": v(74, 184.58) * mm, "mid": v(75.93, 183.48) * mm, "end": v(76.42, 181.3) * mm, "construction": true});
            skLineSegment(sketch, "E424", {"start": v(63.51, 116.41) * mm, "end": v(76.42, 181.3) * mm, "construction": true});
            skLineSegment(sketch, "E425", {"start": v(9.29, 121.75) * mm, "end": v(9.29, 131.78) * mm});
            skArc(sketch, "E426", {"start": v(7.21, 174.06) * mm, "mid": v(8.77, 152.95) * mm, "end": v(9.29, 131.78) * mm});
            skLineSegment(sketch, "E427", {"start": v(63.51, 116.41) * mm, "end": v(75.44, 176.38) * mm});
            skArc(sketch, "E428", {"start": v(75.44, 176.38) * mm, "mid": v(74.95, 178.56) * mm, "end": v(73, 179.65) * mm});
            skArc(sketch, "E429", {"start": v(73, 179.65) * mm, "mid": v(47.87, 181.1) * mm, "end": v(22.7, 180.62) * mm});
            skArc(sketch, "E430", {"start": v(22.7, 180.62) * mm, "mid": v(21.45, 180.88) * mm, "end": v(20.49, 181.72) * mm});
            skArc(sketch, "E431", {"start": v(14.1, 185.04) * mm, "mid": v(17.71, 184.2) * mm, "end": v(20.49, 181.72) * mm});
            skArc(sketch, "E432", {"start": v(11.94, 174.9) * mm, "mid": v(12.3, 174.8) * mm, "end": v(12.49, 174.46) * mm});
            skArc(sketch, "E433", {"start": v(13.1, 175.02) * mm, "mid": v(12.77, 174.84) * mm, "end": v(12.66, 174.47) * mm});
            skArc(sketch, "E434", {"start": v(11.98, 174.53) * mm, "mid": v(12.07, 174.5) * mm, "end": v(12.11, 174.42) * mm});
            skArc(sketch, "E435", {"start": v(13.15, 174.65) * mm, "mid": v(13.06, 174.6) * mm, "end": v(13.03, 174.51) * mm});
            skArc(sketch, "E436", {"start": v(24.95, 152.04) * mm, "mid": v(25.1, 152.35) * mm, "end": v(25.01, 152.68) * mm});
            skArc(sketch, "E437", {"start": v(25.8, 152.86) * mm, "mid": v(25.39, 152.73) * mm, "end": v(25.03, 152.98) * mm});
            skArc(sketch, "E438", {"start": v(24.69, 152.3) * mm, "mid": v(24.72, 152.38) * mm, "end": v(24.7, 152.46) * mm});
            skArc(sketch, "E439", {"start": v(25.55, 153.13) * mm, "mid": v(25.44, 153.1) * mm, "end": v(25.35, 153.17) * mm});
            skLineSegment(sketch, "E440", {"start": v(15.01, 175.2) * mm, "end": v(10.04, 174.72) * mm});
            skLineSegment(sketch, "E441", {"start": v(7.21, 174.06) * mm, "end": v(6.47, 181.57) * mm});
            skArc(sketch, "E442", {"start": v(14.1, 185.04) * mm, "mid": v(11.52, 184.82) * mm, "end": v(8.94, 184.58) * mm});
            skLineSegment(sketch, "E443", {"start": v(12.52, 174.96) * mm, "end": v(14.56, 154.32) * mm, "construction": true});
            skArc(sketch, "E444", {"start": v(14.56, 154.32) * mm, "mid": v(17.3, 152.07) * mm, "end": v(19.53, 154.8) * mm, "construction": true});
            skLineSegment(sketch, "E445", {"start": v(19.53, 154.8) * mm, "end": v(18.64, 163.84) * mm, "construction": true});
            skArc(sketch, "E446", {"start": v(18.64, 163.84) * mm, "mid": v(20.89, 166.58) * mm, "end": v(23.62, 164.33) * mm, "construction": true});
            skLineSegment(sketch, "E447", {"start": v(23.62, 164.33) * mm, "end": v(24.51, 155.3) * mm, "construction": true});
            skLineSegment(sketch, "E448", {"start": v(19.53, 154.8) * mm, "end": v(24.51, 155.3) * mm, "construction": true});
            skLineSegment(sketch, "E449", {"start": v(24.51, 155.3) * mm, "end": v(24.65, 153.91) * mm, "construction": true});
            skArc(sketch, "E450", {"start": v(24.65, 153.91) * mm, "mid": v(24.87, 153.1) * mm, "end": v(25.34, 152.42) * mm, "construction": true});
            skArc(sketch, "E451", {"start": v(25.03, 152.98) * mm, "mid": v(24.83, 153.44) * mm, "end": v(24.73, 153.92) * mm});
            skArc(sketch, "E452", {"start": v(25.35, 153.17) * mm, "mid": v(25.19, 153.55) * mm, "end": v(25.1, 153.96) * mm});
            skArc(sketch, "E453", {"start": v(25.01, 152.68) * mm, "mid": v(24.7, 153.26) * mm, "end": v(24.56, 153.9) * mm});
            skArc(sketch, "E454", {"start": v(24.7, 152.46) * mm, "mid": v(24.35, 153.13) * mm, "end": v(24.19, 153.86) * mm});
            skLineSegment(sketch, "E455", {"start": v(24.73, 153.92) * mm, "end": v(23.7, 164.34) * mm});
            skLineSegment(sketch, "E456", {"start": v(25.1, 153.96) * mm, "end": v(24.08, 164.38) * mm});
            skLineSegment(sketch, "E457", {"start": v(24.56, 153.9) * mm, "end": v(23.53, 164.33) * mm});
            skLineSegment(sketch, "E458", {"start": v(24.19, 153.86) * mm, "end": v(23.16, 164.29) * mm});
            skArc(sketch, "E459", {"start": v(24.08, 164.38) * mm, "mid": v(20.84, 167.04) * mm, "end": v(18.18, 163.8) * mm});
            skArc(sketch, "E460", {"start": v(23.7, 164.34) * mm, "mid": v(20.88, 166.66) * mm, "end": v(18.56, 163.84) * mm});
            skArc(sketch, "E461", {"start": v(23.53, 164.33) * mm, "mid": v(20.9, 166.5) * mm, "end": v(18.73, 163.85) * mm});
            skArc(sketch, "E462", {"start": v(23.16, 164.29) * mm, "mid": v(20.93, 166.12) * mm, "end": v(19.1, 163.9) * mm});
            skLineSegment(sketch, "E463", {"start": v(18.73, 163.85) * mm, "end": v(19.62, 154.82) * mm});
            skLineSegment(sketch, "E464", {"start": v(19.1, 163.9) * mm, "end": v(20, 154.85) * mm});
            skLineSegment(sketch, "E465", {"start": v(18.56, 163.84) * mm, "end": v(19.45, 154.8) * mm});
            skLineSegment(sketch, "E466", {"start": v(18.18, 163.8) * mm, "end": v(19.07, 154.76) * mm});
            skArc(sketch, "E467", {"start": v(20, 154.85) * mm, "mid": v(17.34, 151.61) * mm, "end": v(14.1, 154.27) * mm});
            skArc(sketch, "E468", {"start": v(19.62, 154.82) * mm, "mid": v(17.3, 151.99) * mm, "end": v(14.47, 154.3) * mm});
            skArc(sketch, "E469", {"start": v(19.45, 154.8) * mm, "mid": v(17.28, 152.16) * mm, "end": v(14.65, 154.33) * mm});
            skArc(sketch, "E470", {"start": v(19.07, 154.76) * mm, "mid": v(17.25, 152.53) * mm, "end": v(15.02, 154.36) * mm});
            skLineSegment(sketch, "E471", {"start": v(14.1, 154.27) * mm, "end": v(12.11, 174.42) * mm});
            skLineSegment(sketch, "E472", {"start": v(12.49, 174.46) * mm, "end": v(14.47, 154.3) * mm});
            skLineSegment(sketch, "E473", {"start": v(14.65, 154.33) * mm, "end": v(12.66, 174.47) * mm});
            skLineSegment(sketch, "E474", {"start": v(13.03, 174.51) * mm, "end": v(15.02, 154.36) * mm});
            skLineSegment(sketch, "E475", {"start": v(20.49, 181.72) * mm, "end": v(19.76, 193.22) * mm, "construction": true});
            skPoint(sketch, "E476.visualSharp", {"position": v(9.54, 174.67) * mm});
            skArc(sketch, "E476.filletArc", {"start": v(9.5, 175.17) * mm, "mid": v(9.67, 174.83) * mm, "end": v(10.04, 174.72) * mm});
            skPoint(sketch, "E477.visualSharp", {"position": v(9.4, 176.16) * mm});
            skArc(sketch, "E477.filletArc", {"start": v(9.89, 176.21) * mm, "mid": v(9.55, 176.03) * mm, "end": v(9.44, 175.66) * mm});
            skPoint(sketch, "E478.visualSharp", {"position": v(15.36, 176.75) * mm});
            skArc(sketch, "E478.filletArc", {"start": v(15.41, 176.25) * mm, "mid": v(15.23, 176.59) * mm, "end": v(14.87, 176.7) * mm});
            skPoint(sketch, "E479.visualSharp", {"position": v(15.51, 175.26) * mm});
            skArc(sketch, "E479.filletArc", {"start": v(15.01, 175.2) * mm, "mid": v(15.35, 175.39) * mm, "end": v(15.46, 175.75) * mm});
            skArc(sketch, "E480", {"start": v(9.07, 175.63) * mm, "mid": v(9.26, 176.27) * mm, "end": v(9.85, 176.58) * mm});
            skArc(sketch, "E481", {"start": v(10.07, 174.34) * mm, "mid": v(9.43, 174.54) * mm, "end": v(9.12, 175.13) * mm});
            skArc(sketch, "E482", {"start": v(14.83, 177.07) * mm, "mid": v(15.47, 176.88) * mm, "end": v(15.79, 176.29) * mm});
            skArc(sketch, "E483", {"start": v(15.05, 174.83) * mm, "mid": v(15.64, 175.15) * mm, "end": v(15.83, 175.8) * mm});
            skLineSegment(sketch, "E484", {"start": v(10.04, 174.72) * mm, "end": v(11.94, 174.9) * mm});
            skLineSegment(sketch, "E485", {"start": v(13.1, 175.02) * mm, "end": v(15.01, 175.2) * mm});
            skLineSegment(sketch, "E486", {"start": v(9.44, 175.66) * mm, "end": v(9.5, 175.17) * mm});
            skLineSegment(sketch, "E487", {"start": v(7.21, 174.06) * mm, "end": v(15.05, 174.83) * mm});
            skLineSegment(sketch, "E488", {"start": v(15.83, 175.8) * mm, "end": v(15.2, 182.26) * mm});
            skLineSegment(sketch, "E489", {"start": v(6.5, 182.28) * mm, "end": v(14.24, 183.04) * mm});
            skPoint(sketch, "E490.visualSharp", {"position": v(8.8, 182.13) * mm});
            skArc(sketch, "E490.filletArc", {"start": v(9.3, 182.18) * mm, "mid": v(8.96, 182) * mm, "end": v(8.85, 181.63) * mm});
            skPoint(sketch, "E491.visualSharp", {"position": v(14.78, 182.72) * mm});
            skArc(sketch, "E491.filletArc", {"start": v(14.82, 182.22) * mm, "mid": v(14.64, 182.56) * mm, "end": v(14.28, 182.67) * mm});
            skPoint(sketch, "E492.visualSharp", {"position": v(8.95, 180.64) * mm});
            skArc(sketch, "E492.filletArc", {"start": v(8.9, 181.14) * mm, "mid": v(9.08, 180.8) * mm, "end": v(9.45, 180.69) * mm});
            skPoint(sketch, "E493.visualSharp", {"position": v(14.92, 181.23) * mm});
            skArc(sketch, "E493.filletArc", {"start": v(14.42, 181.18) * mm, "mid": v(14.76, 181.36) * mm, "end": v(14.87, 181.73) * mm});
            skPoint(sketch, "E494.visualSharp", {"position": v(9.1, 179.15) * mm});
            skArc(sketch, "E494.filletArc", {"start": v(9.6, 179.2) * mm, "mid": v(9.26, 179.02) * mm, "end": v(9.15, 178.65) * mm});
            skPoint(sketch, "E495.visualSharp", {"position": v(15.07, 179.73) * mm});
            skArc(sketch, "E495.filletArc", {"start": v(15.12, 179.24) * mm, "mid": v(14.94, 179.57) * mm, "end": v(14.57, 179.69) * mm});
            skPoint(sketch, "E496.visualSharp", {"position": v(9.25, 177.65) * mm});
            skArc(sketch, "E496.filletArc", {"start": v(9.2, 178.15) * mm, "mid": v(9.38, 177.81) * mm, "end": v(9.74, 177.7) * mm});
            skPoint(sketch, "E497.visualSharp", {"position": v(15.22, 178.24) * mm});
            skArc(sketch, "E497.filletArc", {"start": v(14.72, 178.2) * mm, "mid": v(15.06, 178.37) * mm, "end": v(15.17, 178.74) * mm});
            skArc(sketch, "E498", {"start": v(15.2, 182.26) * mm, "mid": v(14.88, 182.85) * mm, "end": v(14.24, 183.04) * mm});
            skArc(sketch, "E499", {"start": v(14.1, 185.04) * mm, "mid": v(16.17, 184.38) * mm, "end": v(17.19, 182.46) * mm});
            skArc(sketch, "E500", {"start": v(17.83, 175.99) * mm, "mid": v(17.19, 173.88) * mm, "end": v(15.25, 172.84) * mm});
            skLineSegment(sketch, "E501", {"start": v(17.19, 182.46) * mm, "end": v(17.83, 175.99) * mm});
            skLineSegment(sketch, "E502", {"start": v(15.25, 172.84) * mm, "end": v(7.4, 172.07) * mm});
            skArc(sketch, "E503", {"start": v(7.4, 172.07) * mm, "mid": v(7.3, 173.07) * mm, "end": v(7.21, 174.06) * mm});
            skArc(sketch, "E504", {"start": v(25.94, 152.99) * mm, "mid": v(16.17, 139.8) * mm, "end": v(11.76, 123.99) * mm});
            skArc(sketch, "E505", {"start": v(8.94, 184.58) * mm, "mid": v(7.33, 183.85) * mm, "end": v(6.5, 182.28) * mm});
            skSolve(sketch);
        }
        {
            var Q0;
            Q0=makeQuery(id+"F11.imprint","IMPRINT",FACE,{"disambiguationData":[TD([[makeQuery(id+"F11.imprint","IMPRINT",EDGE,{"derivedFrom":sQuery(id+"F11.wireOp",EDGE,"E111")}),1.0]])]});
            var Q1;
            Q1=makeQuery(id+"F11.imprint","IMPRINT",FACE,{"disambiguationData":[TD([[makeQuery(id+"F11.imprint","IMPRINT",EDGE,{"derivedFrom":sQuery(id+"F11.wireOp",EDGE,"E109")}),-1.0]])]});
            var Q2;
            Q2=makeQuery(id+"F11.imprint","IMPRINT",FACE,{"disambiguationData":[TD([[makeQuery(id+"F11.imprint","IMPRINT",EDGE,{"derivedFrom":sQuery(id+"F11.wireOp",EDGE,"E105")}),-1.0]])]});
            var Q3;
            Q3=makeQuery(id+"F11.imprint","IMPRINT",FACE,{"disambiguationData":[TD([[makeQuery(id+"F11.imprint","IMPRINT",EDGE,{"derivedFrom":sQuery(id+"F11.wireOp",EDGE,"E102")}),-1.0]])]});
            var Q4;
            Q4=makeQuery(id+"F14.imprint","IMPRINT",FACE,{"disambiguationData":[TD([[makeQuery(id+"F14.imprint","IMPRINT",EDGE,{"derivedFrom":sQuery(id+"F14.wireOp",EDGE,"E404")}),-1.0]])]});
            var Q5;
            Q5=makeQuery(id+"F14.imprint","IMPRINT",FACE,{"disambiguationData":[TD([[makeQuery(id+"F14.imprint","IMPRINT",EDGE,{"derivedFrom":sQuery(id+"F14.wireOp",EDGE,"E399")}),1.0]])]});
            var Q6;
            {var subQ15=sQuery(id+"F14.wireOp",EDGE,"05e3b848-1be8-4af3-8a49-c68e9e9613c2");Q6=makeQuery(id+"F14.imprint","IMPRINT",FACE,{"disambiguationData":[TD([[makeQuery(id+"F14.imprint","IMPRINT",EDGE,{"derivedFrom":subQ15}),-1.0]])]});}
            var Q7;
            {var subQ0=sQuery(id+"F14.wireOp",EDGE,"739677fa-8a64-46dd-bc65-96a784fd16b4");Q7=makeQuery(id+"F14.imprint","IMPRINT",FACE,{"disambiguationData":[TD([[makeQuery(id+"F14.imprint","IMPRINT",EDGE,{"derivedFrom":subQ0}),-1.0]])]});}
            var Q8;
            Q8=makeQuery(id+"F14.imprint","IMPRINT",FACE,{"disambiguationData":[TD([[makeQuery(id+"F14.imprint","IMPRINT",EDGE,{"derivedFrom":sQuery(id+"F14.wireOp",EDGE,"27bb5f62-1be2-4d33-bba8-376d6956f919")}),-1.0]])]});
            var Q9;
            Q9=makeQuery(id+"F14.imprint","IMPRINT",FACE,{"disambiguationData":[TD([[makeQuery(id+"F14.imprint","IMPRINT",EDGE,{"derivedFrom":sQuery(id+"F14.wireOp",EDGE,"M0GH2ECu-TJde-gAEw-h3w4-6obv8RUlEYnZ")}),-1.0]])]});
            var Q10;
            {var subQ0=sQuery(id+"F14.wireOp",EDGE,"E432");Q10=makeQuery(id+"F14.imprint","IMPRINT",FACE,{"disambiguationData":[TD([[makeQuery(id+"F14.imprint","IMPRINT",EDGE,{"derivedFrom":subQ0}),1.0]])]});}
            var Q11;
            {var subQ3=sQuery(id+"F11.wireOp",EDGE,"3ZwgxJEr-Fj1A-CWMw-4jtn-5xYg9qtM2FhJ");Q11=makeQuery(id+"F11.imprint","IMPRINT",FACE,{"disambiguationData":[TD([[makeQuery(id+"F11.imprint","IMPRINT",EDGE,{"derivedFrom":subQ3}),1.0]])]});}
            var Q12;
            {var subQ0=sQuery(id+"F11.wireOp",EDGE,"bfa322b4-3175-47c7-9921-a8ef762783cf");Q12=makeQuery(id+"F11.imprint","IMPRINT",FACE,{"disambiguationData":[TD([[makeQuery(id+"F11.imprint","IMPRINT",EDGE,{"derivedFrom":subQ0}),-1.0]])]});}
            var Q13;
            {var subQ0=sQuery(id+"F11.wireOp",EDGE,"86ae1680-b77d-4497-a398-d127f6d7fb81");Q13=makeQuery(id+"F11.imprint","IMPRINT",FACE,{"disambiguationData":[TD([[makeQuery(id+"F11.imprint","IMPRINT",EDGE,{"derivedFrom":subQ0}),1.0]])]});}
            var Q14;
            {var subQ0=sQuery(id+"F11.wireOp",EDGE,"1cqTsjwP-8AdJ-weZB-YpCa-5vRwb66xrnEp");Q14=makeQuery(id+"F11.imprint","IMPRINT",FACE,{"disambiguationData":[TD([[makeQuery(id+"F11.imprint","IMPRINT",EDGE,{"derivedFrom":subQ0}),-1.0]])]});}
            var Q15;
            {var subQ0=sQuery(id+"F11.wireOp",EDGE,"Gz13DKtl-pfxj-H7rw-OtZb-VJwHssRc0r4z");Q15=makeQuery(id+"F11.imprint","IMPRINT",FACE,{"disambiguationData":[TD([[makeQuery(id+"F11.imprint","IMPRINT",EDGE,{"derivedFrom":subQ0}),-1.0]])]});}
            var Q16;
            {var subQ1=sQuery(id+"F11.wireOp",EDGE,"9dd486e6-1597-40ad-9d63-5cce52d91597");Q16=makeQuery(id+"F11.imprint","IMPRINT",FACE,{"disambiguationData":[TD([[makeQuery(id+"F11.imprint","IMPRINT",EDGE,{"derivedFrom":subQ1}),1.0]])]});}
            var Q17;
            {var subQ5=sQuery(id+"F11.wireOp",EDGE,"7947f4c7-ca59-4ee2-8d29-9dba9fdf1c3b");Q17=makeQuery(id+"F11.imprint","IMPRINT",FACE,{"disambiguationData":[TD([[makeQuery(id+"F11.imprint","IMPRINT",EDGE,{"derivedFrom":subQ5}),-1.0]])]});}
            var Q18;
            {var subQ5=sQuery(id+"F11.wireOp",EDGE,"c3TaBS0F-oUOR-dk8s-DOzr-yRH7NZHr7XZj");Q18=makeQuery(id+"F11.imprint","IMPRINT",FACE,{"disambiguationData":[TD([[makeQuery(id+"F11.imprint","IMPRINT",EDGE,{"derivedFrom":subQ5}),-1.0]])]});}
            var Q19;
            Q19=makeQuery(id+"F11.imprint","IMPRINT",FACE,{"disambiguationData":[TD([[makeQuery(id+"F11.imprint","IMPRINT",EDGE,{"derivedFrom":sQuery(id+"F11.wireOp",EDGE,"64Bcb5KG-AyA4-SO89-iI0L-4smSVroV5yBi")}),-1.0]])]});
            var Q20;
            {var subQ5=sQuery(id+"F11.wireOp",EDGE,"ba716494-44b9-4cd0-93b5-e918898fd8a4");Q20=makeQuery(id+"F11.imprint","IMPRINT",FACE,{"disambiguationData":[TD([[makeQuery(id+"F11.imprint","IMPRINT",EDGE,{"derivedFrom":subQ5}),-1.0]])]});}
            var Q21;
            {var subQ1=sQuery(id+"F11.wireOp",EDGE,"VaUrTSEi-XY0c-lDqD-HFzR-l1aolr6rI4y1");Q21=makeQuery(id+"F11.imprint","IMPRINT",FACE,{"disambiguationData":[TD([[makeQuery(id+"F11.imprint","IMPRINT",EDGE,{"derivedFrom":subQ1}),-1.0]])]});}
            extrude(context, id + "F15", {"entities" : qUnion([Q0, Q1, Q2, Q3, Q4, Q5, Q6, Q7, Q8, Q9, Q10, Q11, Q12, Q13, Q14, Q15, Q16, Q17, Q18, Q19, Q20, Q21]), "depth" : 1 * mm, "offsetDistance" : 25 * mm});
        }
        {
            var Q0;
            Q0=makeQuery(id+"F15.opExtrude","SWEPT_BODY",BODY,{"disambiguationData":[OSD([sQuery(id+"F11.wireOp",EDGE,"E111"),sQuery(id+"F11.wireOp",EDGE,"E112"),sQuery(id+"F11.wireOp",EDGE,"E113"),sQuery(id+"F11.wireOp",EDGE,"E114"),sQuery(id+"F11.wireOp",EDGE,"E115"),sQuery(id+"F11.wireOp",EDGE,"E116"),sQuery(id+"F11.wireOp",EDGE,"IQQRE2rV-5Kpd-wcM1-lf7l-OkSrCdiXXyCo"),sQuery(id+"F11.wireOp",EDGE,"E117"),sQuery(id+"F11.wireOp",EDGE,"E118"),sQuery(id+"F11.wireOp",EDGE,"E119"),sQuery(id+"F11.wireOp",EDGE,"E120"),sQuery(id+"F11.wireOp",EDGE,"E121"),sQuery(id+"F11.wireOp",EDGE,"yiQzbs6f-Lpyu-wlKd-hScW-LrXk4wmNUg2q"),sQuery(id+"F11.wireOp",EDGE,"yUt90Jjj-ngW3-Tbpk-6VdH-Rd4ZIIn7CyCU"),sQuery(id+"F11.wireOp",EDGE,"E122"),sQuery(id+"F11.wireOp",EDGE,"64Bcb5KG-AyA4-SO89-iI0L-4smSVroV5yBi"),sQuery(id+"F11.wireOp",EDGE,"VaUrTSEi-XY0c-lDqD-HFzR-l1aolr6rI4y1"),sQuery(id+"F11.wireOp",EDGE,"c3TaBS0F-oUOR-dk8s-DOzr-yRH7NZHr7XZj"),sQuery(id+"F11.wireOp",EDGE,"psoi2Hcv-0Ciq-A78d-YBLg-XFcdE7A3XUtX"),sQuery(id+"F11.wireOp",EDGE,"Gt7Bl2Am-XWpN-a3Zv-Gmu1-cgxpcOrpGpWO"),sQuery(id+"F11.wireOp",EDGE,"m7zvoW1m-qwkV-gzsP-65fe-J6m5pQ5Bnm19"),sQuery(id+"F11.wireOp",EDGE,"RFZixWyr-YMTb-OXgd-1zur-Qm1B11M79eMD"),sQuery(id+"F11.wireOp",EDGE,"E124.bottom"),sQuery(id+"F11.wireOp",EDGE,"E124.top"),sQuery(id+"F11.wireOp",EDGE,"E124.left"),sQuery(id+"F11.wireOp",EDGE,"E124.right"),sQuery(id+"F11.wireOp",EDGE,"ba716494-44b9-4cd0-93b5-e918898fd8a4"),sQuery(id+"F11.wireOp",EDGE,"0bb8082c-beeb-4848-8283-a7a35a5983e0"),sQuery(id+"F11.wireOp",EDGE,"a32f22d6-360f-4899-9a59-135d499b7efe"),sQuery(id+"F11.wireOp",EDGE,"9d940e78-ed18-4705-82a7-9ae9ba0bf3ac"),sQuery(id+"F11.wireOp",EDGE,"6b5288ed-c813-4619-8c3c-f6de361b3ea8"),sQuery(id+"F11.wireOp",EDGE,"17ce50a9-48ba-4d20-9152-f5a371502f30"),sQuery(id+"F11.wireOp",EDGE,"7a78a1e9-44cb-4d4c-9e10-05a7271733df"),sQuery(id+"F11.wireOp",EDGE,"cSyBJ7Tw-dHcS-k6DO-Mjo4-P66Yp3aKPEtm"),sQuery(id+"F11.wireOp",EDGE,"LTdhcXTM-Af2l-Zre3-5kdN-xHZ03IlXqEph"),sQuery(id+"F11.wireOp",EDGE,"zYLczOxZ-XPHS-3xzC-ZppE-IoJYERNcb0xU"),sQuery(id+"F11.wireOp",EDGE,"jQ8TzUSm-gk7X-tLK9-nHDY-RWuozRJztMb2"),sQuery(id+"F11.wireOp",EDGE,"7ce1Zazf-VxHz-Zkl5-HolT-DawPfXkeq4Qr"),sQuery(id+"F11.wireOp",EDGE,"O8mihj6e-81Au-ADRF-oPVT-2XxfMLKtOn3M"),sQuery(id+"F11.wireOp",EDGE,"a6I2aCfc-HqTM-qYxX-rxuA-zrBG2WbCpEOk"),sQuery(id+"F11.wireOp",EDGE,"73365783-fdde-42db-ab3d-7901bd2d6966"),sQuery(id+"F11.wireOp",EDGE,"ee203d4c-b8c1-4c57-8fa7-69690fdc4036"),sQuery(id+"F11.wireOp",EDGE,"a6b9fffd-5c9d-4f88-a79f-33371510ba99"),sQuery(id+"F11.wireOp",EDGE,"5fadcabe-0f0f-4ca3-aeec-64bc1c070811"),sQuery(id+"F11.wireOp",EDGE,"E128"),sQuery(id+"F11.wireOp",EDGE,"OnND54Wu-9h4t-angj-H6Y5-r0Tf3rFCQcNW"),sQuery(id+"F11.wireOp",EDGE,"E129"),sQuery(id+"F11.wireOp",EDGE,"knFrkC8b-DIjB-8Qwp-BKgm-06lmYrInIpoj"),sQuery(id+"F11.wireOp",EDGE,"E130"),sQuery(id+"F11.wireOp",EDGE,"E131"),sQuery(id+"F11.wireOp",EDGE,"ca50a5d0-5ebd-41c2-8ac8-51f1fea0cd80"),sQuery(id+"F11.wireOp",EDGE,"842f79ea-3c3c-4c22-95c7-3e0c68b36a1d"),sQuery(id+"F11.wireOp",EDGE,"e6b76868-323a-4ce5-b48f-cac23c9dd792"),sQuery(id+"F11.wireOp",EDGE,"7947f4c7-ca59-4ee2-8d29-9dba9fdf1c3b"),sQuery(id+"F11.wireOp",EDGE,"1a9165fc-cbfd-4294-99f8-a92c6cbcd42a"),sQuery(id+"F11.wireOp",EDGE,"a442be1d-81d8-467e-8587-f2279989b3c7"),sQuery(id+"F11.wireOp",EDGE,"96567833-f821-4463-9748-d09fb2a1845e"),sQuery(id+"F11.wireOp",EDGE,"67409c75-5550-459b-abbe-ccc0aa6f181c"),sQuery(id+"F11.wireOp",EDGE,"q5PL6oAu-YdFy-FzFk-IoUQ-C1iUWSJAdoto"),sQuery(id+"F11.wireOp",EDGE,"TBmsXXiJ-TwmY-DG5B-8AFb-k3b1aQVJbrUs"),sQuery(id+"F11.wireOp",EDGE,"6p14eqTZ-gODh-1tLH-2JqC-KoW4ZTOgZVsY"),sQuery(id+"F11.wireOp",EDGE,"yYRojuLF-cyOD-1KcU-2AWJ-6gHus4ns4fZq"),sQuery(id+"F11.wireOp",EDGE,"ZCGWrlSr-dCWK-klhF-Xxu0-X7b1utZTvmWi"),sQuery(id+"F11.wireOp",EDGE,"G01M3x1V-PGIN-Se9G-nOri-cp2YVTskCEdf"),sQuery(id+"F11.wireOp",EDGE,"a8hhojAE-V7pc-RjNK-lZXR-0HOtIUqE8E3F"),sQuery(id+"F11.wireOp",EDGE,"hnLkDO30-YONT-PtIJ-KYGy-klhHjBwCoJJY"),sQuery(id+"F11.wireOp",EDGE,"E135"),sQuery(id+"F11.wireOp",EDGE,"E136"),sQuery(id+"F11.wireOp",EDGE,"uSPanDuh-w4wP-WNQf-NOHj-YhQXvOaKv0cj"),sQuery(id+"F11.wireOp",EDGE,"ph9Oblpb-tM9M-7BtX-gQu0-IXiQmVqFyO7F"),sQuery(id+"F11.wireOp",EDGE,"vyw7Ctnh-ASTt-dYbi-Z1VD-YA4w9f1g5E3N"),sQuery(id+"F11.wireOp",EDGE,"9CY6Oyp3-notu-dulK-YImq-b4rprF7rj3Vf"),sQuery(id+"F11.wireOp",EDGE,"iamOBy5o-QBhj-wwXS-HLC8-zSS3SCnLaghp"),sQuery(id+"F11.wireOp",EDGE,"ZWQM5W10-NqvF-hvc7-iT1w-ERNawCmISb96"),sQuery(id+"F11.wireOp",EDGE,"no8OaWae-sWzO-x5Og-x3UX-IRrFmuwGOxKL"),sQuery(id+"F11.wireOp",EDGE,"E137"),sQuery(id+"F11.wireOp",EDGE,"58ewjK00-6ynO-Gprl-0Zju-bY47my7pWQGD"),sQuery(id+"F11.wireOp",EDGE,"qnRgNzS5-xfKG-tF0W-vf6M-7l6ExGLdjFn5"),sQuery(id+"F11.wireOp",EDGE,"yQaWZ6Nq-xy1H-UAYC-6h4L-RVqaiTDAVWHC"),sQuery(id+"F11.wireOp",EDGE,"y5HGxHOP-if7b-kNJB-BaAP-VETklVDXl6Sc"),sQuery(id+"F11.wireOp",EDGE,"2ooJa8KW-eFe2-zS8r-kmer-qqNbkaA5Njh4"),sQuery(id+"F11.wireOp",EDGE,"TMsGtlXF-2nYX-omMv-zXXy-Ynzc1sPjrEcX"),sQuery(id+"F11.wireOp",EDGE,"5qQIFZ9P-Gju6-0W3V-r8HJ-dueB0blg3ToN"),sQuery(id+"F11.wireOp",EDGE,"T0Bvp6qB-q1ZA-tung-jRko-eNWzO3tZ73jF")])]});
            var Q1;
            Q1=makeQuery(id+"F15.opExtrude","SWEPT_BODY",BODY,{"disambiguationData":[OSD([sQuery(id+"F11.wireOp",EDGE,"E109"),sQuery(id+"F11.wireOp",EDGE,"sya9XgnW-V2tY-nugV-xpCj-aX3TywWM1klf"),sQuery(id+"F11.wireOp",EDGE,"HXAWA1DV-BGFp-LmUs-Nngs-kUotns7iQbk1"),sQuery(id+"F11.wireOp",EDGE,"of4uPN2T-ekcr-rsrg-VuOU-T2fo4pH2k5Y5"),sQuery(id+"F11.wireOp",EDGE,"geCaCTM7-RfMI-m4o0-LZJi-09CtPMCiCpj5"),sQuery(id+"F11.wireOp",EDGE,"vUOAt2X5-e5D7-vtSo-Ac2P-htJrtQhmvKyW"),sQuery(id+"F11.wireOp",EDGE,"E133.bottom"),sQuery(id+"F11.wireOp",EDGE,"E133.top"),sQuery(id+"F11.wireOp",EDGE,"E133.left"),sQuery(id+"F11.wireOp",EDGE,"E134"),sQuery(id+"F11.wireOp",EDGE,"QzkVgM4t-b91o-KjyI-QkhW-5pBfGIljAtjP"),sQuery(id+"F11.wireOp",EDGE,"YnQwFlfR-MAfy-VyG3-xr06-MWQKxdtX9x88"),sQuery(id+"F11.wireOp",EDGE,"COlokQ5a-gWuD-l4MG-3UMm-cABrk59LxYLc")])]});
            var Q2;
            Q2=makeQuery(id+"F15.opExtrude","SWEPT_BODY",BODY,{"disambiguationData":[OSD([sQuery(id+"F11.wireOp",EDGE,"E105"),sQuery(id+"F11.wireOp",EDGE,"E106"),sQuery(id+"F11.wireOp",EDGE,"E107"),sQuery(id+"F11.wireOp",EDGE,"E123.bottom"),sQuery(id+"F11.wireOp",EDGE,"E123.top"),sQuery(id+"F11.wireOp",EDGE,"E123.left"),sQuery(id+"F11.wireOp",EDGE,"gk0cJWU9-L1ZQ-GsG8-AbQ3-LLSBuLKdQZ6E"),sQuery(id+"F11.wireOp",EDGE,"gOyBXcYf-cOVr-QrhB-sY2v-YnKnFnRmjlbE"),sQuery(id+"F11.wireOp",EDGE,"E126"),sQuery(id+"F11.wireOp",EDGE,"rp8uBfj3-4r0u-OaR5-n9tn-qAwreJL5hUGs"),sQuery(id+"F11.wireOp",EDGE,"5UwY1BJL-wulg-pZ0m-33h6-AllKO2EMVnlj"),sQuery(id+"F11.wireOp",EDGE,"gxiorD4F-QWbr-IcB5-3Z96-Nlp4EO7NYo10"),sQuery(id+"F11.wireOp",EDGE,"oUKA4nwu-Jd5Q-vPJv-kBpO-0J7FpQ336TAe"),sQuery(id+"F11.wireOp",EDGE,"4PWpi5Vt-IZI8-CRqQ-zThn-QvvE1DD7Dgl6"),sQuery(id+"F11.wireOp",EDGE,"aFlhTLxW-Y5Ul-tnaO-3mYz-zZfVHAf3fQnT"),sQuery(id+"F11.wireOp",EDGE,"4hlB7E6R-D0OL-r8KN-q4kG-dpxQqlBQHIO9")])]});
            var Q3;
            Q3=makeQuery(id+"F15.opExtrude","SWEPT_BODY",BODY,{"disambiguationData":[OSD([sQuery(id+"F11.wireOp",EDGE,"E102"),sQuery(id+"F11.wireOp",EDGE,"E103"),sQuery(id+"F11.wireOp",EDGE,"E104"),sQuery(id+"F11.wireOp",EDGE,"E125.bottom"),sQuery(id+"F11.wireOp",EDGE,"E125.top"),sQuery(id+"F11.wireOp",EDGE,"E125.left"),sQuery(id+"F11.wireOp",EDGE,"EkA3MFmr-zZew-W9Zl-KRRc-O9o1PhcOuHb4"),sQuery(id+"F11.wireOp",EDGE,"nwqc7a2Z-JTt1-m02v-q3SS-M6kEiVfTcHws"),sQuery(id+"F11.wireOp",EDGE,"PrdkI702-266d-MPuO-s9CF-iwuPEE8XKvN0"),sQuery(id+"F11.wireOp",EDGE,"E127"),sQuery(id+"F11.wireOp",EDGE,"84hn7ElG-Qg2I-DbMo-EpSw-dF6nTAr2Bl8M"),sQuery(id+"F11.wireOp",EDGE,"RX82zbVl-BaUT-DbDd-OE2A-87vfBDYbp6g3"),sQuery(id+"F11.wireOp",EDGE,"3k02mvHf-VHWW-Q50S-tYuY-sv5TZYTTHMTh"),sQuery(id+"F11.wireOp",EDGE,"aRhX9v3G-oJhZ-SnzU-5LTo-Ko8Scm4DQ9se"),sQuery(id+"F11.wireOp",EDGE,"UKg41yim-E6zY-ykjh-ZrMU-cAKrZbdPC9ld"),sQuery(id+"F11.wireOp",EDGE,"wOkQEosG-wKsl-5QvX-U1h4-igqNqr0TwLQF"),sQuery(id+"F11.wireOp",EDGE,"DcKigh35-o1RR-0YRt-0XPs-iAb3oXU8aJkr"),sQuery(id+"F11.wireOp",EDGE,"PzcRjFyC-jpfp-M8Tz-XzdP-vfjjNvr3rWwT"),sQuery(id+"F11.wireOp",EDGE,"72tSe2jA-ljkE-L4Df-RLeq-QbrKYMPvBu7k"),sQuery(id+"F11.wireOp",EDGE,"E36yWKCz-7Rj4-VcSS-dhNu-e0lnfpeYh7e6")])]});
            var Q4;
            Q4=makeQuery(id+"F15.opExtrude","SWEPT_BODY",BODY,{"disambiguationData":[OSD([sQuery(id+"FfzbkFBdFVCJwbv_10.wireOp",EDGE,"pMaro4go-hhWT-XRwU-BoUJ-gH4cMqmHsHch"),sQuery(id+"FfzbkFBdFVCJwbv_10.wireOp",EDGE,"8e39e867-e8bd-4ccf-ae07-84d433d8f4bd.bottom"),sQuery(id+"FfzbkFBdFVCJwbv_10.wireOp",EDGE,"8e39e867-e8bd-4ccf-ae07-84d433d8f4bd.top"),sQuery(id+"FfzbkFBdFVCJwbv_10.wireOp",EDGE,"8e39e867-e8bd-4ccf-ae07-84d433d8f4bd.left"),sQuery(id+"FfzbkFBdFVCJwbv_10.wireOp",EDGE,"edae407e-5f36-41aa-968f-71b6d96f6b23"),sQuery(id+"FfzbkFBdFVCJwbv_10.wireOp",EDGE,"f5efc572-66d8-4176-a84a-da9384822e6e"),sQuery(id+"FfzbkFBdFVCJwbv_10.wireOp",EDGE,"7fd0a594-57d4-42c3-b7f3-25d5394343b2"),sQuery(id+"FfzbkFBdFVCJwbv_10.wireOp",EDGE,"055fff77-897b-43d4-93d3-f32b7461de00"),sQuery(id+"FfzbkFBdFVCJwbv_10.wireOp",EDGE,"e35bec5e-3a26-4b75-b8d8-da37e6a2f010"),sQuery(id+"FfzbkFBdFVCJwbv_10.wireOp",EDGE,"d9fa0aa5-08ef-4d11-bd09-e6bfb0ba7802"),sQuery(id+"FfzbkFBdFVCJwbv_10.wireOp",EDGE,"751ab5f4-fd7c-4df0-adf8-25008f893c00"),sQuery(id+"FfzbkFBdFVCJwbv_10.wireOp",EDGE,"8950d7d7-f33d-4674-8905-b88a5d0b8d27"),sQuery(id+"FfzbkFBdFVCJwbv_10.wireOp",EDGE,"cyRVUxEQ-ICrS-j9sY-rQaG-5QnZHZMNdntX"),sQuery(id+"FfzbkFBdFVCJwbv_10.wireOp",EDGE,"QGs82O4h-kaO3-u7m5-VTHH-Oyfp2VCKAdBy"),sQuery(id+"FfzbkFBdFVCJwbv_10.wireOp",EDGE,"S1hgNixZ-yWgM-b5hI-s881-Ai3pdsTLqqob"),sQuery(id+"FfzbkFBdFVCJwbv_10.wireOp",EDGE,"PIUcTswp-MlX2-YZ2c-v6Rp-TOZMR3NXptv3"),sQuery(id+"FfzbkFBdFVCJwbv_10.wireOp",EDGE,"YDkuFdZs-T1hC-rLMX-OnbK-sK5z0DD8idoM"),sQuery(id+"FfzbkFBdFVCJwbv_10.wireOp",EDGE,"1Vc6heaP-snwX-XvXS-04rn-GL9fLOodEBVN"),sQuery(id+"FfzbkFBdFVCJwbv_10.wireOp",EDGE,"XNVXoTuT-qIrY-wxvr-dTGQ-HqY0tU18Dd6t"),sQuery(id+"FfzbkFBdFVCJwbv_10.wireOp",EDGE,"KSVEPRJa-XfUO-1FIk-Ssqg-qzbbqPuFVmMe"),sQuery(id+"FfzbkFBdFVCJwbv_10.wireOp",EDGE,"1S7gZ8Ej-vTPA-h1nd-TPJY-eeWiyGMGxeO8"),sQuery(id+"FfzbkFBdFVCJwbv_10.wireOp",EDGE,"MynldYxO-WDaE-KUfe-EZOC-clE3euBvTSkt"),sQuery(id+"FfzbkFBdFVCJwbv_10.wireOp",EDGE,"85cHvmd1-yEQc-Lb7S-JebZ-IbZDY9wXOG2e"),sQuery(id+"FfzbkFBdFVCJwbv_10.wireOp",EDGE,"Go8Pgaqv-uCue-Db5Y-dBZh-1UhJBO1K0ZSg"),sQuery(id+"FfzbkFBdFVCJwbv_10.wireOp",EDGE,"BsAmfu4a-2ILW-wZM3-sI31-YdjEXItnYcS2"),sQuery(id+"FfzbkFBdFVCJwbv_10.wireOp",EDGE,"CgynlPr5-CC9I-iZsD-GU5b-gtvjQ2ySegnw"),sQuery(id+"FfzbkFBdFVCJwbv_10.wireOp",EDGE,"HtpKR5sn-V6UX-hM7L-KhJ4-I73Gx1JZZKap"),sQuery(id+"FfzbkFBdFVCJwbv_10.wireOp",EDGE,"FSk6Fhh8-H8JC-JPOQ-RdTE-xnN3ekTQb8bL"),sQuery(id+"FfzbkFBdFVCJwbv_10.wireOp",EDGE,"RRT5bmSj-cTcY-VOFG-4BTM-Ap6DbkUr6ObX"),sQuery(id+"FfzbkFBdFVCJwbv_10.wireOp",EDGE,"Y7Svxjp8-4l6D-yU5n-X8vt-GgCcTbmUt3Rg"),sQuery(id+"FfzbkFBdFVCJwbv_10.wireOp",EDGE,"tvunvOrf-oltB-Dqpm-36ob-TCf7FA3Gm531"),sQuery(id+"FfzbkFBdFVCJwbv_10.wireOp",EDGE,"c3662180-4b74-4a23-83ce-5996887a5051"),sQuery(id+"FfzbkFBdFVCJwbv_10.wireOp",EDGE,"ada75fb6-bfa2-4e2d-9b40-bfdfb3d1ca81"),sQuery(id+"FfzbkFBdFVCJwbv_10.wireOp",EDGE,"a31c36b7-3760-4ba8-94ba-6a4695022099"),sQuery(id+"FfzbkFBdFVCJwbv_10.wireOp",EDGE,"c1ee504d-d5a1-4e3b-8c89-d309a9d4346e"),sQuery(id+"FfzbkFBdFVCJwbv_10.wireOp",EDGE,"2f48cabb-cf27-42ee-89be-6966c4d14573"),sQuery(id+"FfzbkFBdFVCJwbv_10.wireOp",EDGE,"59e63341-b462-482c-83ff-ff6a5ef797a5"),sQuery(id+"FfzbkFBdFVCJwbv_10.wireOp",EDGE,"80fc59d1-9654-422b-968b-d6c1de99813e"),sQuery(id+"FfzbkFBdFVCJwbv_10.wireOp",EDGE,"d935156d-d0e6-4c42-8c5a-1061eb53fa67"),sQuery(id+"FfzbkFBdFVCJwbv_10.wireOp",EDGE,"45cac806-5938-4dc5-98d1-0c3278c9ab22"),sQuery(id+"FfzbkFBdFVCJwbv_10.wireOp",EDGE,"998cf4c1-1857-4cb5-80d4-1fc8b766386f"),sQuery(id+"FfzbkFBdFVCJwbv_10.wireOp",EDGE,"0wNNpLJW-l59k-id1m-ml8Q-WSQrxwQSO5iA"),sQuery(id+"FfzbkFBdFVCJwbv_10.wireOp",EDGE,"nHcUcM3h-hVjx-qwhR-TByW-smJ7hupptyGC"),sQuery(id+"FfzbkFBdFVCJwbv_10.wireOp",EDGE,"LeHkZFTw-ACja-w1is-SBAN-RjoPOmuNYnxS"),sQuery(id+"FfzbkFBdFVCJwbv_10.wireOp",EDGE,"u9uCOyeH-y4Fg-aSIV-KQZf-4dDpmRlZn627"),sQuery(id+"FfzbkFBdFVCJwbv_10.wireOp",EDGE,"ODAicDLt-Z99e-i1C4-yYV9-ZLBldcGSDGv8"),sQuery(id+"FfzbkFBdFVCJwbv_10.wireOp",EDGE,"lhBjye7T-UWjJ-iHnC-LYft-wRsyJUsqJ6KF"),sQuery(id+"FfzbkFBdFVCJwbv_10.wireOp",EDGE,"KvNwYrbE-kIsR-9cyE-pgtq-oCCJ6USuyQEB"),sQuery(id+"FfzbkFBdFVCJwbv_10.wireOp",EDGE,"EnG0bfCs-cgH3-Ti9O-cNWP-jZjwcCOoen4e"),sQuery(id+"FfzbkFBdFVCJwbv_10.wireOp",EDGE,"R6mJUjMo-kaUB-2oiA-4xkH-LdkNvPCycJZB"),sQuery(id+"FfzbkFBdFVCJwbv_10.wireOp",EDGE,"fYMTgZNb-By25-ubTC-UkMj-tyZM5ZvnlvUz"),sQuery(id+"FfzbkFBdFVCJwbv_10.wireOp",EDGE,"Xe9FOYmP-J8et-h5hP-YKDN-KSXQdabHTH2L"),sQuery(id+"FfzbkFBdFVCJwbv_10.wireOp",EDGE,"2SU0mnWp-rcka-3ibU-pxta-e2BWqNJvBKcG"),sQuery(id+"FfzbkFBdFVCJwbv_10.wireOp",EDGE,"fVUAGAgD-zIwA-tjgY-zRFS-7BH1aBjWtOtP"),sQuery(id+"FfzbkFBdFVCJwbv_10.wireOp",EDGE,"KQZA0Rxr-Nmtb-Kv8r-1oNZ-PlE0hLAS1GmQ"),sQuery(id+"FfzbkFBdFVCJwbv_10.wireOp",EDGE,"A9mWITf9-cPIg-nf4X-FW53-4073lrxkWfxG"),sQuery(id+"FfzbkFBdFVCJwbv_10.wireOp",EDGE,"S77rbIqr-Bpaw-brnp-8Wik-cfeRlCvzrS9v")])]});
            var Q5;
            Q5=makeQuery(id+"F15.opExtrude","SWEPT_BODY",BODY,{"disambiguationData":[OSD([sQuery(id+"FfzbkFBdFVCJwbv_10.wireOp",EDGE,"giPf3VGc-mAjr-Obee-9MIG-xt78EOTjN3qf"),sQuery(id+"FfzbkFBdFVCJwbv_10.wireOp",EDGE,"jGcAnInZ-aNgS-K3qr-yB7S-7Kicut0NrT9G"),sQuery(id+"FfzbkFBdFVCJwbv_10.wireOp",EDGE,"ILc2cF3V-TWRs-6u6s-Gvd7-PTBhRdLF71If"),sQuery(id+"FfzbkFBdFVCJwbv_10.wireOp",EDGE,"a2ed52dc-4920-4d88-8f70-0e7cf9d7bd03.bottom"),sQuery(id+"FfzbkFBdFVCJwbv_10.wireOp",EDGE,"a2ed52dc-4920-4d88-8f70-0e7cf9d7bd03.top"),sQuery(id+"FfzbkFBdFVCJwbv_10.wireOp",EDGE,"a2ed52dc-4920-4d88-8f70-0e7cf9d7bd03.left"),sQuery(id+"FfzbkFBdFVCJwbv_10.wireOp",EDGE,"dc83978c-d294-4de9-86ea-b08e130bb54f"),sQuery(id+"FfzbkFBdFVCJwbv_10.wireOp",EDGE,"2c891795-e76e-467c-a32c-8a69265539bc"),sQuery(id+"FfzbkFBdFVCJwbv_10.wireOp",EDGE,"IR2PraHq-wAvS-29lZ-0jrW-zFZI447NLSXx"),sQuery(id+"FfzbkFBdFVCJwbv_10.wireOp",EDGE,"XspBbyy8-uGZq-F1QG-IIC5-jU40SdlIYO6e"),sQuery(id+"FfzbkFBdFVCJwbv_10.wireOp",EDGE,"TpH6StQC-tl8g-JST3-GiXc-WqYgIyjXtp8E"),sQuery(id+"FfzbkFBdFVCJwbv_10.wireOp",EDGE,"JtK4YcQE-gUzX-0ptx-glQ5-IkEo1EV7b2yJ"),sQuery(id+"FfzbkFBdFVCJwbv_10.wireOp",EDGE,"dUKfjWZV-RxhK-eCeW-IRqE-LFjWqTICCH0Y"),sQuery(id+"FfzbkFBdFVCJwbv_10.wireOp",EDGE,"vzh1PQUM-MiMl-yYXn-q8Ni-0QtE1J8Ms9wo")])]});
            var Q6;
            Q6=makeQuery(id+"F15.opExtrude","SWEPT_BODY",BODY,{"disambiguationData":[OSD([sQuery(id+"FfzbkFBdFVCJwbv_10.wireOp",EDGE,"7fe99bb9-a079-4323-8eb5-455072d4104d.top"),sQuery(id+"FfzbkFBdFVCJwbv_10.wireOp",EDGE,"9af218eb-ad32-4ea5-9ff6-53b1381bfb9e"),sQuery(id+"FfzbkFBdFVCJwbv_10.wireOp",EDGE,"11e897f7-a3ae-42fa-a581-f3854dd6a997"),sQuery(id+"FfzbkFBdFVCJwbv_10.wireOp",EDGE,"ssxteN0k-Q4Up-uukn-9L1Y-ipymDcN8MpIf"),sQuery(id+"FfzbkFBdFVCJwbv_10.wireOp",EDGE,"69t77pY7-RTbA-rddB-5hPK-Nkn9YIqUoj3B"),sQuery(id+"FfzbkFBdFVCJwbv_10.wireOp",EDGE,"BA4oqOUP-JqyG-VUEC-zW6q-lSfEN4VLTCTw"),sQuery(id+"FfzbkFBdFVCJwbv_10.wireOp",EDGE,"tFJNmuv7-FfLg-RZwV-TmdY-gBPchVcT9YKF"),sQuery(id+"FfzbkFBdFVCJwbv_10.wireOp",EDGE,"Fhjp6Og2-5fyt-LmCL-37JN-5Vxqx5JfEOd6"),sQuery(id+"FfzbkFBdFVCJwbv_10.wireOp",EDGE,"YRsAc26L-xgfG-1s44-2Pl8-FoSgDH3VLn49"),sQuery(id+"FfzbkFBdFVCJwbv_10.wireOp",EDGE,"NbRgRyRc-jrkx-oVvc-kf00-kwk2bjU1KYkG"),sQuery(id+"FfzbkFBdFVCJwbv_10.wireOp",EDGE,"CeukAeWD-7mRF-qXIj-3kDQ-RKLk9U6G1Mqm"),sQuery(id+"FfzbkFBdFVCJwbv_10.wireOp",EDGE,"VHmk0F1W-oPQh-5QIm-Ol6o-Ycvp39kG4Ylk"),sQuery(id+"FfzbkFBdFVCJwbv_10.wireOp",EDGE,"GbreKtQT-HZxb-owMy-peNa-AtCEd36uZu6T"),sQuery(id+"FfzbkFBdFVCJwbv_10.wireOp",EDGE,"W7vEI6OY-tMSi-wr4G-Xi9U-H5QDELR5sZQh"),sQuery(id+"FfzbkFBdFVCJwbv_10.wireOp",EDGE,"xbOI6asG-sjBj-E0fu-mwjY-iiWOY2fW1mF2"),sQuery(id+"FfzbkFBdFVCJwbv_10.wireOp",EDGE,"zlYsrZEl-yWKR-Fhxg-23ll-jntcs04vmOwE")])]});
            var Q7;
            Q7=makeQuery(id+"F15.opExtrude","SWEPT_BODY",BODY,{"disambiguationData":[OSD([sQuery(id+"F14.wireOp",EDGE,"E404"),sQuery(id+"F14.wireOp",EDGE,"E405"),sQuery(id+"F14.wireOp",EDGE,"E406"),sQuery(id+"F14.wireOp",EDGE,"r0KhDNtO-ns52-19aB-KdiW-GgmM3I9yKp0t"),sQuery(id+"F14.wireOp",EDGE,"E407"),sQuery(id+"F14.wireOp",EDGE,"E408"),sQuery(id+"F14.wireOp",EDGE,"E409"),sQuery(id+"F14.wireOp",EDGE,"FXE418A8-cqte-ilxS-k1h9-3DrXZjwwGSNL"),sQuery(id+"F14.wireOp",EDGE,"y1MZkFG2-leT5-1A3v-CJhO-uytfxgDZ9mdG"),sQuery(id+"F14.wireOp",EDGE,"05e3b848-1be8-4af3-8a49-c68e9e9613c2"),sQuery(id+"F14.wireOp",EDGE,"27bb5f62-1be2-4d33-bba8-376d6956f919"),sQuery(id+"F14.wireOp",EDGE,"739677fa-8a64-46dd-bc65-96a784fd16b4"),sQuery(id+"F14.wireOp",EDGE,"b016ea66-e491-42d9-bdd1-975789c7df8b"),sQuery(id+"F14.wireOp",EDGE,"E412"),sQuery(id+"F14.wireOp",EDGE,"E413"),sQuery(id+"F14.wireOp",EDGE,"E414"),sQuery(id+"F14.wireOp",EDGE,"E415"),sQuery(id+"F14.wireOp",EDGE,"E417"),sQuery(id+"F14.wireOp",EDGE,"E418.bottom"),sQuery(id+"F14.wireOp",EDGE,"E418.top"),sQuery(id+"F14.wireOp",EDGE,"E418.left"),sQuery(id+"F14.wireOp",EDGE,"E418.right"),sQuery(id+"F14.wireOp",EDGE,"E419.bottom"),sQuery(id+"F14.wireOp",EDGE,"E419.top"),sQuery(id+"F14.wireOp",EDGE,"E419.left"),sQuery(id+"F14.wireOp",EDGE,"E419.right"),sQuery(id+"F14.wireOp",EDGE,"E420"),sQuery(id+"F14.wireOp",EDGE,"6BFwJvZz-uIvj-Z4hY-DHks-Pf0gI3oHQzLU"),sQuery(id+"F14.wireOp",EDGE,"E421"),sQuery(id+"F14.wireOp",EDGE,"9656cc1b-6abc-4712-9e47-6e3c32f5efe6"),sQuery(id+"F14.wireOp",EDGE,"d87c57a7-c7e6-495d-810c-5a37cc58677d"),sQuery(id+"F14.wireOp",EDGE,"kssZpKZg-vMEi-FHPF-ME7z-0W7tv2roSjCG"),sQuery(id+"F14.wireOp",EDGE,"7a629359-6b34-4532-b885-3285dcaf4faa"),sQuery(id+"F14.wireOp",EDGE,"b89e655e-2d09-46ce-a84f-d76718cc0fb7")])]});
            var Q8;
            Q8=makeQuery(id+"F15.opExtrude","SWEPT_BODY",BODY,{"disambiguationData":[OSD([sQuery(id+"F14.wireOp",EDGE,"E399"),sQuery(id+"F14.wireOp",EDGE,"E400"),sQuery(id+"F14.wireOp",EDGE,"E401"),sQuery(id+"F14.wireOp",EDGE,"E402"),sQuery(id+"F14.wireOp",EDGE,"E403"),sQuery(id+"F14.wireOp",EDGE,"M6EC3zYn-Tsr6-8L6j-psJ4-BRUrJLJKtSP3"),sQuery(id+"F14.wireOp",EDGE,"ZVO5TtfE-jQ49-X1Qi-q7mN-Ux8LytcP7Cxg"),sQuery(id+"F14.wireOp",EDGE,"E411.bottom"),sQuery(id+"F14.wireOp",EDGE,"E411.top"),sQuery(id+"F14.wireOp",EDGE,"E411.left"),sQuery(id+"F14.wireOp",EDGE,"E416"),sQuery(id+"F14.wireOp",EDGE,"93b73fb0-2ae8-4f6a-b8b3-b3cce48ac09b")])]});
            transform(context, id + "F16", {"entities" : qUnion([Q0, Q1, Q2, Q3, Q4, Q5, Q6, Q7, Q8]), "transformType" : TransformType.TRANSLATION_3D, "dx" : 562 * mm, "dy" : 0 * mm, "dz" : 0 * mm, "makeCopy" : true});
        }
        {
            var Q0;
            Q0=makeQuery(id+"F16.opPattern","COPY",BODY,{"derivedFrom":makeQuery(id+"F15.opExtrude","SWEPT_BODY",BODY,{"disambiguationData":[OSD([sQuery(id+"FfzbkFBdFVCJwbv_10.wireOp",EDGE,"pMaro4go-hhWT-XRwU-BoUJ-gH4cMqmHsHch"),sQuery(id+"FfzbkFBdFVCJwbv_10.wireOp",EDGE,"8e39e867-e8bd-4ccf-ae07-84d433d8f4bd.bottom"),sQuery(id+"FfzbkFBdFVCJwbv_10.wireOp",EDGE,"8e39e867-e8bd-4ccf-ae07-84d433d8f4bd.top"),sQuery(id+"FfzbkFBdFVCJwbv_10.wireOp",EDGE,"8e39e867-e8bd-4ccf-ae07-84d433d8f4bd.left"),sQuery(id+"FfzbkFBdFVCJwbv_10.wireOp",EDGE,"edae407e-5f36-41aa-968f-71b6d96f6b23"),sQuery(id+"FfzbkFBdFVCJwbv_10.wireOp",EDGE,"f5efc572-66d8-4176-a84a-da9384822e6e"),sQuery(id+"FfzbkFBdFVCJwbv_10.wireOp",EDGE,"7fd0a594-57d4-42c3-b7f3-25d5394343b2"),sQuery(id+"FfzbkFBdFVCJwbv_10.wireOp",EDGE,"055fff77-897b-43d4-93d3-f32b7461de00"),sQuery(id+"FfzbkFBdFVCJwbv_10.wireOp",EDGE,"e35bec5e-3a26-4b75-b8d8-da37e6a2f010"),sQuery(id+"FfzbkFBdFVCJwbv_10.wireOp",EDGE,"d9fa0aa5-08ef-4d11-bd09-e6bfb0ba7802"),sQuery(id+"FfzbkFBdFVCJwbv_10.wireOp",EDGE,"751ab5f4-fd7c-4df0-adf8-25008f893c00"),sQuery(id+"FfzbkFBdFVCJwbv_10.wireOp",EDGE,"8950d7d7-f33d-4674-8905-b88a5d0b8d27"),sQuery(id+"FfzbkFBdFVCJwbv_10.wireOp",EDGE,"cyRVUxEQ-ICrS-j9sY-rQaG-5QnZHZMNdntX"),sQuery(id+"FfzbkFBdFVCJwbv_10.wireOp",EDGE,"QGs82O4h-kaO3-u7m5-VTHH-Oyfp2VCKAdBy"),sQuery(id+"FfzbkFBdFVCJwbv_10.wireOp",EDGE,"S1hgNixZ-yWgM-b5hI-s881-Ai3pdsTLqqob"),sQuery(id+"FfzbkFBdFVCJwbv_10.wireOp",EDGE,"PIUcTswp-MlX2-YZ2c-v6Rp-TOZMR3NXptv3"),sQuery(id+"FfzbkFBdFVCJwbv_10.wireOp",EDGE,"YDkuFdZs-T1hC-rLMX-OnbK-sK5z0DD8idoM"),sQuery(id+"FfzbkFBdFVCJwbv_10.wireOp",EDGE,"1Vc6heaP-snwX-XvXS-04rn-GL9fLOodEBVN"),sQuery(id+"FfzbkFBdFVCJwbv_10.wireOp",EDGE,"XNVXoTuT-qIrY-wxvr-dTGQ-HqY0tU18Dd6t"),sQuery(id+"FfzbkFBdFVCJwbv_10.wireOp",EDGE,"KSVEPRJa-XfUO-1FIk-Ssqg-qzbbqPuFVmMe"),sQuery(id+"FfzbkFBdFVCJwbv_10.wireOp",EDGE,"1S7gZ8Ej-vTPA-h1nd-TPJY-eeWiyGMGxeO8"),sQuery(id+"FfzbkFBdFVCJwbv_10.wireOp",EDGE,"MynldYxO-WDaE-KUfe-EZOC-clE3euBvTSkt"),sQuery(id+"FfzbkFBdFVCJwbv_10.wireOp",EDGE,"85cHvmd1-yEQc-Lb7S-JebZ-IbZDY9wXOG2e"),sQuery(id+"FfzbkFBdFVCJwbv_10.wireOp",EDGE,"Go8Pgaqv-uCue-Db5Y-dBZh-1UhJBO1K0ZSg"),sQuery(id+"FfzbkFBdFVCJwbv_10.wireOp",EDGE,"BsAmfu4a-2ILW-wZM3-sI31-YdjEXItnYcS2"),sQuery(id+"FfzbkFBdFVCJwbv_10.wireOp",EDGE,"CgynlPr5-CC9I-iZsD-GU5b-gtvjQ2ySegnw"),sQuery(id+"FfzbkFBdFVCJwbv_10.wireOp",EDGE,"HtpKR5sn-V6UX-hM7L-KhJ4-I73Gx1JZZKap"),sQuery(id+"FfzbkFBdFVCJwbv_10.wireOp",EDGE,"FSk6Fhh8-H8JC-JPOQ-RdTE-xnN3ekTQb8bL"),sQuery(id+"FfzbkFBdFVCJwbv_10.wireOp",EDGE,"RRT5bmSj-cTcY-VOFG-4BTM-Ap6DbkUr6ObX"),sQuery(id+"FfzbkFBdFVCJwbv_10.wireOp",EDGE,"Y7Svxjp8-4l6D-yU5n-X8vt-GgCcTbmUt3Rg"),sQuery(id+"FfzbkFBdFVCJwbv_10.wireOp",EDGE,"tvunvOrf-oltB-Dqpm-36ob-TCf7FA3Gm531"),sQuery(id+"FfzbkFBdFVCJwbv_10.wireOp",EDGE,"c3662180-4b74-4a23-83ce-5996887a5051"),sQuery(id+"FfzbkFBdFVCJwbv_10.wireOp",EDGE,"ada75fb6-bfa2-4e2d-9b40-bfdfb3d1ca81"),sQuery(id+"FfzbkFBdFVCJwbv_10.wireOp",EDGE,"a31c36b7-3760-4ba8-94ba-6a4695022099"),sQuery(id+"FfzbkFBdFVCJwbv_10.wireOp",EDGE,"c1ee504d-d5a1-4e3b-8c89-d309a9d4346e"),sQuery(id+"FfzbkFBdFVCJwbv_10.wireOp",EDGE,"2f48cabb-cf27-42ee-89be-6966c4d14573"),sQuery(id+"FfzbkFBdFVCJwbv_10.wireOp",EDGE,"59e63341-b462-482c-83ff-ff6a5ef797a5"),sQuery(id+"FfzbkFBdFVCJwbv_10.wireOp",EDGE,"80fc59d1-9654-422b-968b-d6c1de99813e"),sQuery(id+"FfzbkFBdFVCJwbv_10.wireOp",EDGE,"d935156d-d0e6-4c42-8c5a-1061eb53fa67"),sQuery(id+"FfzbkFBdFVCJwbv_10.wireOp",EDGE,"45cac806-5938-4dc5-98d1-0c3278c9ab22"),sQuery(id+"FfzbkFBdFVCJwbv_10.wireOp",EDGE,"998cf4c1-1857-4cb5-80d4-1fc8b766386f"),sQuery(id+"FfzbkFBdFVCJwbv_10.wireOp",EDGE,"0wNNpLJW-l59k-id1m-ml8Q-WSQrxwQSO5iA"),sQuery(id+"FfzbkFBdFVCJwbv_10.wireOp",EDGE,"nHcUcM3h-hVjx-qwhR-TByW-smJ7hupptyGC"),sQuery(id+"FfzbkFBdFVCJwbv_10.wireOp",EDGE,"LeHkZFTw-ACja-w1is-SBAN-RjoPOmuNYnxS"),sQuery(id+"FfzbkFBdFVCJwbv_10.wireOp",EDGE,"u9uCOyeH-y4Fg-aSIV-KQZf-4dDpmRlZn627"),sQuery(id+"FfzbkFBdFVCJwbv_10.wireOp",EDGE,"ODAicDLt-Z99e-i1C4-yYV9-ZLBldcGSDGv8"),sQuery(id+"FfzbkFBdFVCJwbv_10.wireOp",EDGE,"lhBjye7T-UWjJ-iHnC-LYft-wRsyJUsqJ6KF"),sQuery(id+"FfzbkFBdFVCJwbv_10.wireOp",EDGE,"KvNwYrbE-kIsR-9cyE-pgtq-oCCJ6USuyQEB"),sQuery(id+"FfzbkFBdFVCJwbv_10.wireOp",EDGE,"EnG0bfCs-cgH3-Ti9O-cNWP-jZjwcCOoen4e"),sQuery(id+"FfzbkFBdFVCJwbv_10.wireOp",EDGE,"R6mJUjMo-kaUB-2oiA-4xkH-LdkNvPCycJZB"),sQuery(id+"FfzbkFBdFVCJwbv_10.wireOp",EDGE,"fYMTgZNb-By25-ubTC-UkMj-tyZM5ZvnlvUz"),sQuery(id+"FfzbkFBdFVCJwbv_10.wireOp",EDGE,"Xe9FOYmP-J8et-h5hP-YKDN-KSXQdabHTH2L"),sQuery(id+"FfzbkFBdFVCJwbv_10.wireOp",EDGE,"2SU0mnWp-rcka-3ibU-pxta-e2BWqNJvBKcG"),sQuery(id+"FfzbkFBdFVCJwbv_10.wireOp",EDGE,"fVUAGAgD-zIwA-tjgY-zRFS-7BH1aBjWtOtP"),sQuery(id+"FfzbkFBdFVCJwbv_10.wireOp",EDGE,"KQZA0Rxr-Nmtb-Kv8r-1oNZ-PlE0hLAS1GmQ"),sQuery(id+"FfzbkFBdFVCJwbv_10.wireOp",EDGE,"A9mWITf9-cPIg-nf4X-FW53-4073lrxkWfxG"),sQuery(id+"FfzbkFBdFVCJwbv_10.wireOp",EDGE,"S77rbIqr-Bpaw-brnp-8Wik-cfeRlCvzrS9v")])]}),"instanceName":"1"});
            var Q1;
            Q1=makeQuery(id+"F16.opPattern","COPY",BODY,{"derivedFrom":makeQuery(id+"F15.opExtrude","SWEPT_BODY",BODY,{"disambiguationData":[OSD([sQuery(id+"FfzbkFBdFVCJwbv_10.wireOp",EDGE,"giPf3VGc-mAjr-Obee-9MIG-xt78EOTjN3qf"),sQuery(id+"FfzbkFBdFVCJwbv_10.wireOp",EDGE,"jGcAnInZ-aNgS-K3qr-yB7S-7Kicut0NrT9G"),sQuery(id+"FfzbkFBdFVCJwbv_10.wireOp",EDGE,"ILc2cF3V-TWRs-6u6s-Gvd7-PTBhRdLF71If"),sQuery(id+"FfzbkFBdFVCJwbv_10.wireOp",EDGE,"a2ed52dc-4920-4d88-8f70-0e7cf9d7bd03.bottom"),sQuery(id+"FfzbkFBdFVCJwbv_10.wireOp",EDGE,"a2ed52dc-4920-4d88-8f70-0e7cf9d7bd03.top"),sQuery(id+"FfzbkFBdFVCJwbv_10.wireOp",EDGE,"a2ed52dc-4920-4d88-8f70-0e7cf9d7bd03.left"),sQuery(id+"FfzbkFBdFVCJwbv_10.wireOp",EDGE,"dc83978c-d294-4de9-86ea-b08e130bb54f"),sQuery(id+"FfzbkFBdFVCJwbv_10.wireOp",EDGE,"2c891795-e76e-467c-a32c-8a69265539bc"),sQuery(id+"FfzbkFBdFVCJwbv_10.wireOp",EDGE,"IR2PraHq-wAvS-29lZ-0jrW-zFZI447NLSXx"),sQuery(id+"FfzbkFBdFVCJwbv_10.wireOp",EDGE,"XspBbyy8-uGZq-F1QG-IIC5-jU40SdlIYO6e"),sQuery(id+"FfzbkFBdFVCJwbv_10.wireOp",EDGE,"TpH6StQC-tl8g-JST3-GiXc-WqYgIyjXtp8E"),sQuery(id+"FfzbkFBdFVCJwbv_10.wireOp",EDGE,"JtK4YcQE-gUzX-0ptx-glQ5-IkEo1EV7b2yJ"),sQuery(id+"FfzbkFBdFVCJwbv_10.wireOp",EDGE,"dUKfjWZV-RxhK-eCeW-IRqE-LFjWqTICCH0Y"),sQuery(id+"FfzbkFBdFVCJwbv_10.wireOp",EDGE,"vzh1PQUM-MiMl-yYXn-q8Ni-0QtE1J8Ms9wo")])]}),"instanceName":"1"});
            var Q2;
            Q2=makeQuery(id+"F16.opPattern","COPY",BODY,{"derivedFrom":makeQuery(id+"F15.opExtrude","SWEPT_BODY",BODY,{"disambiguationData":[OSD([sQuery(id+"FfzbkFBdFVCJwbv_10.wireOp",EDGE,"7fe99bb9-a079-4323-8eb5-455072d4104d.top"),sQuery(id+"FfzbkFBdFVCJwbv_10.wireOp",EDGE,"9af218eb-ad32-4ea5-9ff6-53b1381bfb9e"),sQuery(id+"FfzbkFBdFVCJwbv_10.wireOp",EDGE,"11e897f7-a3ae-42fa-a581-f3854dd6a997"),sQuery(id+"FfzbkFBdFVCJwbv_10.wireOp",EDGE,"ssxteN0k-Q4Up-uukn-9L1Y-ipymDcN8MpIf"),sQuery(id+"FfzbkFBdFVCJwbv_10.wireOp",EDGE,"69t77pY7-RTbA-rddB-5hPK-Nkn9YIqUoj3B"),sQuery(id+"FfzbkFBdFVCJwbv_10.wireOp",EDGE,"BA4oqOUP-JqyG-VUEC-zW6q-lSfEN4VLTCTw"),sQuery(id+"FfzbkFBdFVCJwbv_10.wireOp",EDGE,"tFJNmuv7-FfLg-RZwV-TmdY-gBPchVcT9YKF"),sQuery(id+"FfzbkFBdFVCJwbv_10.wireOp",EDGE,"Fhjp6Og2-5fyt-LmCL-37JN-5Vxqx5JfEOd6"),sQuery(id+"FfzbkFBdFVCJwbv_10.wireOp",EDGE,"YRsAc26L-xgfG-1s44-2Pl8-FoSgDH3VLn49"),sQuery(id+"FfzbkFBdFVCJwbv_10.wireOp",EDGE,"NbRgRyRc-jrkx-oVvc-kf00-kwk2bjU1KYkG"),sQuery(id+"FfzbkFBdFVCJwbv_10.wireOp",EDGE,"CeukAeWD-7mRF-qXIj-3kDQ-RKLk9U6G1Mqm"),sQuery(id+"FfzbkFBdFVCJwbv_10.wireOp",EDGE,"VHmk0F1W-oPQh-5QIm-Ol6o-Ycvp39kG4Ylk"),sQuery(id+"FfzbkFBdFVCJwbv_10.wireOp",EDGE,"GbreKtQT-HZxb-owMy-peNa-AtCEd36uZu6T"),sQuery(id+"FfzbkFBdFVCJwbv_10.wireOp",EDGE,"W7vEI6OY-tMSi-wr4G-Xi9U-H5QDELR5sZQh"),sQuery(id+"FfzbkFBdFVCJwbv_10.wireOp",EDGE,"xbOI6asG-sjBj-E0fu-mwjY-iiWOY2fW1mF2"),sQuery(id+"FfzbkFBdFVCJwbv_10.wireOp",EDGE,"zlYsrZEl-yWKR-Fhxg-23ll-jntcs04vmOwE")])]}),"instanceName":"1"});
            var Q3;
            Q3=makeQuery(id+"F16.opPattern","COPY",BODY,{"derivedFrom":makeQuery(id+"F15.opExtrude","SWEPT_BODY",BODY,{"disambiguationData":[OSD([sQuery(id+"F14.wireOp",EDGE,"E399"),sQuery(id+"F14.wireOp",EDGE,"E400"),sQuery(id+"F14.wireOp",EDGE,"E401"),sQuery(id+"F14.wireOp",EDGE,"E402"),sQuery(id+"F14.wireOp",EDGE,"E403"),sQuery(id+"F14.wireOp",EDGE,"M6EC3zYn-Tsr6-8L6j-psJ4-BRUrJLJKtSP3"),sQuery(id+"F14.wireOp",EDGE,"ZVO5TtfE-jQ49-X1Qi-q7mN-Ux8LytcP7Cxg"),sQuery(id+"F14.wireOp",EDGE,"E411.bottom"),sQuery(id+"F14.wireOp",EDGE,"E411.top"),sQuery(id+"F14.wireOp",EDGE,"E411.left"),sQuery(id+"F14.wireOp",EDGE,"E416"),sQuery(id+"F14.wireOp",EDGE,"93b73fb0-2ae8-4f6a-b8b3-b3cce48ac09b")])]}),"instanceName":"1"});
            var Q4;
            Q4=makeQuery(id+"F16.opPattern","COPY",BODY,{"derivedFrom":makeQuery(id+"F15.opExtrude","SWEPT_BODY",BODY,{"disambiguationData":[OSD([sQuery(id+"F14.wireOp",EDGE,"E404"),sQuery(id+"F14.wireOp",EDGE,"E405"),sQuery(id+"F14.wireOp",EDGE,"E406"),sQuery(id+"F14.wireOp",EDGE,"r0KhDNtO-ns52-19aB-KdiW-GgmM3I9yKp0t"),sQuery(id+"F14.wireOp",EDGE,"E407"),sQuery(id+"F14.wireOp",EDGE,"E408"),sQuery(id+"F14.wireOp",EDGE,"E409"),sQuery(id+"F14.wireOp",EDGE,"FXE418A8-cqte-ilxS-k1h9-3DrXZjwwGSNL"),sQuery(id+"F14.wireOp",EDGE,"y1MZkFG2-leT5-1A3v-CJhO-uytfxgDZ9mdG"),sQuery(id+"F14.wireOp",EDGE,"05e3b848-1be8-4af3-8a49-c68e9e9613c2"),sQuery(id+"F14.wireOp",EDGE,"27bb5f62-1be2-4d33-bba8-376d6956f919"),sQuery(id+"F14.wireOp",EDGE,"739677fa-8a64-46dd-bc65-96a784fd16b4"),sQuery(id+"F14.wireOp",EDGE,"b016ea66-e491-42d9-bdd1-975789c7df8b"),sQuery(id+"F14.wireOp",EDGE,"E412"),sQuery(id+"F14.wireOp",EDGE,"E413"),sQuery(id+"F14.wireOp",EDGE,"E414"),sQuery(id+"F14.wireOp",EDGE,"E415"),sQuery(id+"F14.wireOp",EDGE,"E417"),sQuery(id+"F14.wireOp",EDGE,"E418.bottom"),sQuery(id+"F14.wireOp",EDGE,"E418.top"),sQuery(id+"F14.wireOp",EDGE,"E418.left"),sQuery(id+"F14.wireOp",EDGE,"E418.right"),sQuery(id+"F14.wireOp",EDGE,"E419.bottom"),sQuery(id+"F14.wireOp",EDGE,"E419.top"),sQuery(id+"F14.wireOp",EDGE,"E419.left"),sQuery(id+"F14.wireOp",EDGE,"E419.right"),sQuery(id+"F14.wireOp",EDGE,"E420"),sQuery(id+"F14.wireOp",EDGE,"6BFwJvZz-uIvj-Z4hY-DHks-Pf0gI3oHQzLU"),sQuery(id+"F14.wireOp",EDGE,"E421"),sQuery(id+"F14.wireOp",EDGE,"9656cc1b-6abc-4712-9e47-6e3c32f5efe6"),sQuery(id+"F14.wireOp",EDGE,"d87c57a7-c7e6-495d-810c-5a37cc58677d"),sQuery(id+"F14.wireOp",EDGE,"kssZpKZg-vMEi-FHPF-ME7z-0W7tv2roSjCG"),sQuery(id+"F14.wireOp",EDGE,"7a629359-6b34-4532-b885-3285dcaf4faa"),sQuery(id+"F14.wireOp",EDGE,"b89e655e-2d09-46ce-a84f-d76718cc0fb7")])]}),"instanceName":"1"});
            transform(context, id + "F17", {"entities" : qUnion([Q0, Q1, Q2, Q3, Q4]), "transformType" : TransformType.TRANSLATION_3D, "dx" : 0 * mm, "dy" : -80 * mm, "dz" : 0 * mm, "makeCopy" : false});
        }
        {
            var Q0;
            Q0=makeQuery(id+"F15.opExtrude","SWEPT_BODY",BODY,{"disambiguationData":[OSD([sQuery(id+"F11.wireOp",EDGE,"E109"),sQuery(id+"F11.wireOp",EDGE,"sya9XgnW-V2tY-nugV-xpCj-aX3TywWM1klf"),sQuery(id+"F11.wireOp",EDGE,"HXAWA1DV-BGFp-LmUs-Nngs-kUotns7iQbk1"),sQuery(id+"F11.wireOp",EDGE,"of4uPN2T-ekcr-rsrg-VuOU-T2fo4pH2k5Y5"),sQuery(id+"F11.wireOp",EDGE,"geCaCTM7-RfMI-m4o0-LZJi-09CtPMCiCpj5"),sQuery(id+"F11.wireOp",EDGE,"vUOAt2X5-e5D7-vtSo-Ac2P-htJrtQhmvKyW"),sQuery(id+"F11.wireOp",EDGE,"E133.bottom"),sQuery(id+"F11.wireOp",EDGE,"E133.top"),sQuery(id+"F11.wireOp",EDGE,"E133.left"),sQuery(id+"F11.wireOp",EDGE,"E134"),sQuery(id+"F11.wireOp",EDGE,"QzkVgM4t-b91o-KjyI-QkhW-5pBfGIljAtjP"),sQuery(id+"F11.wireOp",EDGE,"YnQwFlfR-MAfy-VyG3-xr06-MWQKxdtX9x88"),sQuery(id+"F11.wireOp",EDGE,"COlokQ5a-gWuD-l4MG-3UMm-cABrk59LxYLc")])]});
            var Q1;
            Q1=makeQuery(id+"F15.opExtrude","SWEPT_BODY",BODY,{"disambiguationData":[OSD([sQuery(id+"F11.wireOp",EDGE,"E105"),sQuery(id+"F11.wireOp",EDGE,"E106"),sQuery(id+"F11.wireOp",EDGE,"E107"),sQuery(id+"F11.wireOp",EDGE,"E126"),sQuery(id+"F11.wireOp",EDGE,"gxiorD4F-QWbr-IcB5-3Z96-Nlp4EO7NYo10")])]});
            var Q2;
            Q2=makeQuery(id+"F15.opExtrude","SWEPT_BODY",BODY,{"disambiguationData":[OSD([sQuery(id+"F11.wireOp",EDGE,"E102"),sQuery(id+"F11.wireOp",EDGE,"E103"),sQuery(id+"F11.wireOp",EDGE,"E104"),sQuery(id+"F11.wireOp",EDGE,"E125.bottom"),sQuery(id+"F11.wireOp",EDGE,"E125.top"),sQuery(id+"F11.wireOp",EDGE,"E125.left"),sQuery(id+"F11.wireOp",EDGE,"EkA3MFmr-zZew-W9Zl-KRRc-O9o1PhcOuHb4"),sQuery(id+"F11.wireOp",EDGE,"nwqc7a2Z-JTt1-m02v-q3SS-M6kEiVfTcHws"),sQuery(id+"F11.wireOp",EDGE,"PrdkI702-266d-MPuO-s9CF-iwuPEE8XKvN0"),sQuery(id+"F11.wireOp",EDGE,"E127"),sQuery(id+"F11.wireOp",EDGE,"84hn7ElG-Qg2I-DbMo-EpSw-dF6nTAr2Bl8M"),sQuery(id+"F11.wireOp",EDGE,"RX82zbVl-BaUT-DbDd-OE2A-87vfBDYbp6g3"),sQuery(id+"F11.wireOp",EDGE,"3k02mvHf-VHWW-Q50S-tYuY-sv5TZYTTHMTh"),sQuery(id+"F11.wireOp",EDGE,"aRhX9v3G-oJhZ-SnzU-5LTo-Ko8Scm4DQ9se"),sQuery(id+"F11.wireOp",EDGE,"DcKigh35-o1RR-0YRt-0XPs-iAb3oXU8aJkr"),sQuery(id+"F11.wireOp",EDGE,"PzcRjFyC-jpfp-M8Tz-XzdP-vfjjNvr3rWwT"),sQuery(id+"F11.wireOp",EDGE,"72tSe2jA-ljkE-L4Df-RLeq-QbrKYMPvBu7k"),sQuery(id+"F11.wireOp",EDGE,"E36yWKCz-7Rj4-VcSS-dhNu-e0lnfpeYh7e6")])]});
            var Q3;
            Q3=makeQuery(id+"F15.opExtrude","SWEPT_BODY",BODY,{"disambiguationData":[OSD([sQuery(id+"F11.wireOp",EDGE,"E111"),sQuery(id+"F11.wireOp",EDGE,"E112"),sQuery(id+"F11.wireOp",EDGE,"E113"),sQuery(id+"F11.wireOp",EDGE,"E114"),sQuery(id+"F11.wireOp",EDGE,"E115"),sQuery(id+"F11.wireOp",EDGE,"E116"),sQuery(id+"F11.wireOp",EDGE,"IQQRE2rV-5Kpd-wcM1-lf7l-OkSrCdiXXyCo"),sQuery(id+"F11.wireOp",EDGE,"E117"),sQuery(id+"F11.wireOp",EDGE,"E118"),sQuery(id+"F11.wireOp",EDGE,"E119"),sQuery(id+"F11.wireOp",EDGE,"E120"),sQuery(id+"F11.wireOp",EDGE,"E121"),sQuery(id+"F11.wireOp",EDGE,"yiQzbs6f-Lpyu-wlKd-hScW-LrXk4wmNUg2q"),sQuery(id+"F11.wireOp",EDGE,"yUt90Jjj-ngW3-Tbpk-6VdH-Rd4ZIIn7CyCU"),sQuery(id+"F11.wireOp",EDGE,"E122"),sQuery(id+"F11.wireOp",EDGE,"64Bcb5KG-AyA4-SO89-iI0L-4smSVroV5yBi"),sQuery(id+"F11.wireOp",EDGE,"VaUrTSEi-XY0c-lDqD-HFzR-l1aolr6rI4y1"),sQuery(id+"F11.wireOp",EDGE,"c3TaBS0F-oUOR-dk8s-DOzr-yRH7NZHr7XZj"),sQuery(id+"F11.wireOp",EDGE,"psoi2Hcv-0Ciq-A78d-YBLg-XFcdE7A3XUtX"),sQuery(id+"F11.wireOp",EDGE,"Gt7Bl2Am-XWpN-a3Zv-Gmu1-cgxpcOrpGpWO"),sQuery(id+"F11.wireOp",EDGE,"m7zvoW1m-qwkV-gzsP-65fe-J6m5pQ5Bnm19"),sQuery(id+"F11.wireOp",EDGE,"RFZixWyr-YMTb-OXgd-1zur-Qm1B11M79eMD"),sQuery(id+"F11.wireOp",EDGE,"E124.bottom"),sQuery(id+"F11.wireOp",EDGE,"E124.top"),sQuery(id+"F11.wireOp",EDGE,"E124.left"),sQuery(id+"F11.wireOp",EDGE,"E124.right"),sQuery(id+"F11.wireOp",EDGE,"ba716494-44b9-4cd0-93b5-e918898fd8a4"),sQuery(id+"F11.wireOp",EDGE,"0bb8082c-beeb-4848-8283-a7a35a5983e0"),sQuery(id+"F11.wireOp",EDGE,"a32f22d6-360f-4899-9a59-135d499b7efe"),sQuery(id+"F11.wireOp",EDGE,"9d940e78-ed18-4705-82a7-9ae9ba0bf3ac"),sQuery(id+"F11.wireOp",EDGE,"6b5288ed-c813-4619-8c3c-f6de361b3ea8"),sQuery(id+"F11.wireOp",EDGE,"17ce50a9-48ba-4d20-9152-f5a371502f30"),sQuery(id+"F11.wireOp",EDGE,"7a78a1e9-44cb-4d4c-9e10-05a7271733df"),sQuery(id+"F11.wireOp",EDGE,"cSyBJ7Tw-dHcS-k6DO-Mjo4-P66Yp3aKPEtm"),sQuery(id+"F11.wireOp",EDGE,"LTdhcXTM-Af2l-Zre3-5kdN-xHZ03IlXqEph"),sQuery(id+"F11.wireOp",EDGE,"zYLczOxZ-XPHS-3xzC-ZppE-IoJYERNcb0xU"),sQuery(id+"F11.wireOp",EDGE,"jQ8TzUSm-gk7X-tLK9-nHDY-RWuozRJztMb2"),sQuery(id+"F11.wireOp",EDGE,"7ce1Zazf-VxHz-Zkl5-HolT-DawPfXkeq4Qr"),sQuery(id+"F11.wireOp",EDGE,"O8mihj6e-81Au-ADRF-oPVT-2XxfMLKtOn3M"),sQuery(id+"F11.wireOp",EDGE,"a6I2aCfc-HqTM-qYxX-rxuA-zrBG2WbCpEOk"),sQuery(id+"F11.wireOp",EDGE,"73365783-fdde-42db-ab3d-7901bd2d6966"),sQuery(id+"F11.wireOp",EDGE,"ee203d4c-b8c1-4c57-8fa7-69690fdc4036"),sQuery(id+"F11.wireOp",EDGE,"a6b9fffd-5c9d-4f88-a79f-33371510ba99"),sQuery(id+"F11.wireOp",EDGE,"5fadcabe-0f0f-4ca3-aeec-64bc1c070811"),sQuery(id+"F11.wireOp",EDGE,"E128"),sQuery(id+"F11.wireOp",EDGE,"OnND54Wu-9h4t-angj-H6Y5-r0Tf3rFCQcNW"),sQuery(id+"F11.wireOp",EDGE,"E129"),sQuery(id+"F11.wireOp",EDGE,"knFrkC8b-DIjB-8Qwp-BKgm-06lmYrInIpoj"),sQuery(id+"F11.wireOp",EDGE,"E130"),sQuery(id+"F11.wireOp",EDGE,"E131"),sQuery(id+"F11.wireOp",EDGE,"ca50a5d0-5ebd-41c2-8ac8-51f1fea0cd80"),sQuery(id+"F11.wireOp",EDGE,"842f79ea-3c3c-4c22-95c7-3e0c68b36a1d"),sQuery(id+"F11.wireOp",EDGE,"e6b76868-323a-4ce5-b48f-cac23c9dd792"),sQuery(id+"F11.wireOp",EDGE,"7947f4c7-ca59-4ee2-8d29-9dba9fdf1c3b"),sQuery(id+"F11.wireOp",EDGE,"1a9165fc-cbfd-4294-99f8-a92c6cbcd42a"),sQuery(id+"F11.wireOp",EDGE,"a442be1d-81d8-467e-8587-f2279989b3c7"),sQuery(id+"F11.wireOp",EDGE,"96567833-f821-4463-9748-d09fb2a1845e"),sQuery(id+"F11.wireOp",EDGE,"67409c75-5550-459b-abbe-ccc0aa6f181c"),sQuery(id+"F11.wireOp",EDGE,"q5PL6oAu-YdFy-FzFk-IoUQ-C1iUWSJAdoto"),sQuery(id+"F11.wireOp",EDGE,"TBmsXXiJ-TwmY-DG5B-8AFb-k3b1aQVJbrUs"),sQuery(id+"F11.wireOp",EDGE,"6p14eqTZ-gODh-1tLH-2JqC-KoW4ZTOgZVsY"),sQuery(id+"F11.wireOp",EDGE,"yYRojuLF-cyOD-1KcU-2AWJ-6gHus4ns4fZq"),sQuery(id+"F11.wireOp",EDGE,"ZCGWrlSr-dCWK-klhF-Xxu0-X7b1utZTvmWi"),sQuery(id+"F11.wireOp",EDGE,"G01M3x1V-PGIN-Se9G-nOri-cp2YVTskCEdf"),sQuery(id+"F11.wireOp",EDGE,"a8hhojAE-V7pc-RjNK-lZXR-0HOtIUqE8E3F"),sQuery(id+"F11.wireOp",EDGE,"E135"),sQuery(id+"F11.wireOp",EDGE,"E136"),sQuery(id+"F11.wireOp",EDGE,"uSPanDuh-w4wP-WNQf-NOHj-YhQXvOaKv0cj"),sQuery(id+"F11.wireOp",EDGE,"ph9Oblpb-tM9M-7BtX-gQu0-IXiQmVqFyO7F"),sQuery(id+"F11.wireOp",EDGE,"vyw7Ctnh-ASTt-dYbi-Z1VD-YA4w9f1g5E3N"),sQuery(id+"F11.wireOp",EDGE,"ZWQM5W10-NqvF-hvc7-iT1w-ERNawCmISb96"),sQuery(id+"F11.wireOp",EDGE,"no8OaWae-sWzO-x5Og-x3UX-IRrFmuwGOxKL"),sQuery(id+"F11.wireOp",EDGE,"E137"),sQuery(id+"F11.wireOp",EDGE,"y5HGxHOP-if7b-kNJB-BaAP-VETklVDXl6Sc"),sQuery(id+"F11.wireOp",EDGE,"2ooJa8KW-eFe2-zS8r-kmer-qqNbkaA5Njh4"),sQuery(id+"F11.wireOp",EDGE,"TMsGtlXF-2nYX-omMv-zXXy-Ynzc1sPjrEcX"),sQuery(id+"F11.wireOp",EDGE,"5qQIFZ9P-Gju6-0W3V-r8HJ-dueB0blg3ToN"),sQuery(id+"F11.wireOp",EDGE,"E138.bottom"),sQuery(id+"F11.wireOp",EDGE,"E138.top"),sQuery(id+"F11.wireOp",EDGE,"E138.left"),sQuery(id+"F11.wireOp",EDGE,"E138.right"),sQuery(id+"F11.wireOp",EDGE,"E139"),sQuery(id+"F11.wireOp",EDGE,"E143"),sQuery(id+"F11.wireOp",EDGE,"E147")])]});
            var Q4;
            Q4=makeQuery(id+"F15.opExtrude","SWEPT_BODY",BODY,{"disambiguationData":[OSD([sQuery(id+"F14.wireOp",EDGE,"E404"),sQuery(id+"F14.wireOp",EDGE,"E405"),sQuery(id+"F14.wireOp",EDGE,"E406"),sQuery(id+"F14.wireOp",EDGE,"E407"),sQuery(id+"F14.wireOp",EDGE,"E408"),sQuery(id+"F14.wireOp",EDGE,"E409"),sQuery(id+"F14.wireOp",EDGE,"FXE418A8-cqte-ilxS-k1h9-3DrXZjwwGSNL"),sQuery(id+"F14.wireOp",EDGE,"y1MZkFG2-leT5-1A3v-CJhO-uytfxgDZ9mdG"),sQuery(id+"F14.wireOp",EDGE,"05e3b848-1be8-4af3-8a49-c68e9e9613c2"),sQuery(id+"F14.wireOp",EDGE,"27bb5f62-1be2-4d33-bba8-376d6956f919"),sQuery(id+"F14.wireOp",EDGE,"739677fa-8a64-46dd-bc65-96a784fd16b4"),sQuery(id+"F14.wireOp",EDGE,"b016ea66-e491-42d9-bdd1-975789c7df8b"),sQuery(id+"F14.wireOp",EDGE,"E412"),sQuery(id+"F14.wireOp",EDGE,"E413"),sQuery(id+"F14.wireOp",EDGE,"E414"),sQuery(id+"F14.wireOp",EDGE,"E415"),sQuery(id+"F14.wireOp",EDGE,"E417"),sQuery(id+"F14.wireOp",EDGE,"E418.bottom"),sQuery(id+"F14.wireOp",EDGE,"E418.top"),sQuery(id+"F14.wireOp",EDGE,"E418.left"),sQuery(id+"F14.wireOp",EDGE,"E418.right"),sQuery(id+"F14.wireOp",EDGE,"E419.bottom"),sQuery(id+"F14.wireOp",EDGE,"E419.top"),sQuery(id+"F14.wireOp",EDGE,"E419.left"),sQuery(id+"F14.wireOp",EDGE,"E419.right"),sQuery(id+"F14.wireOp",EDGE,"E420"),sQuery(id+"F14.wireOp",EDGE,"E421"),sQuery(id+"F14.wireOp",EDGE,"E422"),sQuery(id+"F14.wireOp",EDGE,"E423"),sQuery(id+"F14.wireOp",EDGE,"E424"),sQuery(id+"F14.wireOp",EDGE,"E425"),sQuery(id+"F14.wireOp",EDGE,"E426")])]});
            var Q5;
            Q5=makeQuery(id+"F15.opExtrude","SWEPT_BODY",BODY,{"disambiguationData":[OSD([sQuery(id+"F14.wireOp",EDGE,"E399"),sQuery(id+"F14.wireOp",EDGE,"E400"),sQuery(id+"F14.wireOp",EDGE,"E401"),sQuery(id+"F14.wireOp",EDGE,"E402"),sQuery(id+"F14.wireOp",EDGE,"E403"),sQuery(id+"F14.wireOp",EDGE,"M6EC3zYn-Tsr6-8L6j-psJ4-BRUrJLJKtSP3"),sQuery(id+"F14.wireOp",EDGE,"ZVO5TtfE-jQ49-X1Qi-q7mN-Ux8LytcP7Cxg"),sQuery(id+"F14.wireOp",EDGE,"E411.bottom"),sQuery(id+"F14.wireOp",EDGE,"E411.top"),sQuery(id+"F14.wireOp",EDGE,"E411.left"),sQuery(id+"F14.wireOp",EDGE,"E416"),sQuery(id+"F14.wireOp",EDGE,"93b73fb0-2ae8-4f6a-b8b3-b3cce48ac09b")])]});
            transform(context, id + "F18", {"entities" : qUnion([Q0, Q1, Q2, Q3, Q4, Q5]), "transformType" : TransformType.TRANSLATION_3D, "dx" : 285 * mm, "dy" : 0 * mm, "dz" : 0 * mm, "makeCopy" : true});
        }
        {
            var Q0;
            Q0=makeQuery(id+"F18.opPattern","COPY",BODY,{"derivedFrom":makeQuery(id+"F15.opExtrude","SWEPT_BODY",BODY,{"disambiguationData":[OSD([sQuery(id+"F14.wireOp",EDGE,"E399"),sQuery(id+"F14.wireOp",EDGE,"E400"),sQuery(id+"F14.wireOp",EDGE,"E401"),sQuery(id+"F14.wireOp",EDGE,"E402"),sQuery(id+"F14.wireOp",EDGE,"E403"),sQuery(id+"F14.wireOp",EDGE,"M6EC3zYn-Tsr6-8L6j-psJ4-BRUrJLJKtSP3"),sQuery(id+"F14.wireOp",EDGE,"ZVO5TtfE-jQ49-X1Qi-q7mN-Ux8LytcP7Cxg"),sQuery(id+"F14.wireOp",EDGE,"E411.bottom"),sQuery(id+"F14.wireOp",EDGE,"E411.top"),sQuery(id+"F14.wireOp",EDGE,"E411.left"),sQuery(id+"F14.wireOp",EDGE,"E416"),sQuery(id+"F14.wireOp",EDGE,"93b73fb0-2ae8-4f6a-b8b3-b3cce48ac09b")])]}),"instanceName":"1"});
            var Q1;
            Q1=makeQuery(id+"F18.opPattern","COPY",BODY,{"derivedFrom":makeQuery(id+"F15.opExtrude","SWEPT_BODY",BODY,{"disambiguationData":[OSD([sQuery(id+"F14.wireOp",EDGE,"E404"),sQuery(id+"F14.wireOp",EDGE,"E405"),sQuery(id+"F14.wireOp",EDGE,"E406"),sQuery(id+"F14.wireOp",EDGE,"E407"),sQuery(id+"F14.wireOp",EDGE,"E408"),sQuery(id+"F14.wireOp",EDGE,"E409"),sQuery(id+"F14.wireOp",EDGE,"FXE418A8-cqte-ilxS-k1h9-3DrXZjwwGSNL"),sQuery(id+"F14.wireOp",EDGE,"y1MZkFG2-leT5-1A3v-CJhO-uytfxgDZ9mdG"),sQuery(id+"F14.wireOp",EDGE,"05e3b848-1be8-4af3-8a49-c68e9e9613c2"),sQuery(id+"F14.wireOp",EDGE,"27bb5f62-1be2-4d33-bba8-376d6956f919"),sQuery(id+"F14.wireOp",EDGE,"739677fa-8a64-46dd-bc65-96a784fd16b4"),sQuery(id+"F14.wireOp",EDGE,"b016ea66-e491-42d9-bdd1-975789c7df8b"),sQuery(id+"F14.wireOp",EDGE,"E412"),sQuery(id+"F14.wireOp",EDGE,"E413"),sQuery(id+"F14.wireOp",EDGE,"E414"),sQuery(id+"F14.wireOp",EDGE,"E415"),sQuery(id+"F14.wireOp",EDGE,"E417"),sQuery(id+"F14.wireOp",EDGE,"E418.bottom"),sQuery(id+"F14.wireOp",EDGE,"E418.top"),sQuery(id+"F14.wireOp",EDGE,"E418.left"),sQuery(id+"F14.wireOp",EDGE,"E418.right"),sQuery(id+"F14.wireOp",EDGE,"E419.bottom"),sQuery(id+"F14.wireOp",EDGE,"E419.top"),sQuery(id+"F14.wireOp",EDGE,"E419.left"),sQuery(id+"F14.wireOp",EDGE,"E419.right"),sQuery(id+"F14.wireOp",EDGE,"E420"),sQuery(id+"F14.wireOp",EDGE,"E421"),sQuery(id+"F14.wireOp",EDGE,"E422"),sQuery(id+"F14.wireOp",EDGE,"E423"),sQuery(id+"F14.wireOp",EDGE,"E424"),sQuery(id+"F14.wireOp",EDGE,"E425"),sQuery(id+"F14.wireOp",EDGE,"E426")])]}),"instanceName":"1"});
            transform(context, id + "F19", {"entities" : qUnion([Q0, Q1]), "transformType" : TransformType.TRANSLATION_3D, "dx" : 0 * mm, "dy" : -41 * mm, "dz" : 0 * mm, "makeCopy" : false});
        }
        {
            var Q0;
            Q0=qCreatedBy(makeId("Top.planeOp"),FACE);
            var sketch = newSketch(context, id + "F20", { "sketchPlane" : qUnion([Q0])});
            skArc(sketch, "E506", {"start": v(9.27, 201.35) * mm, "mid": v(8.52, 201.13) * mm, "end": v(8, 200.56) * mm});
            skArc(sketch, "E507", {"start": v(9.27, 201.35) * mm, "mid": v(9.34, 201.02) * mm, "end": v(9.49, 200.7) * mm});
            skLineSegment(sketch, "E508", {"start": v(8, 200.56) * mm, "end": v(9.49, 200.7) * mm, "construction": true});
            skArc(sketch, "E509.MirrorCS", {"start": v(9.4, 200.03) * mm, "mid": v(8.62, 200.11) * mm, "end": v(8, 200.56) * mm});
            skArc(sketch, "E510.MirrorCS", {"start": v(9.4, 200.03) * mm, "mid": v(9.4, 200.38) * mm, "end": v(9.49, 200.7) * mm});
            skLineSegment(sketch, "E511", {"start": v(9.27, 201.35) * mm, "end": v(9.33, 200.7) * mm, "construction": true});
            skArc(sketch, "E512", {"start": v(76.61, 265.59) * mm, "mid": v(84.9, 251.42) * mm, "end": v(85.17, 235.01) * mm});
            skArc(sketch, "E513", {"start": v(-9.83, 255.12) * mm, "mid": v(-8.9, 247.25) * mm, "end": v(-6.14, 239.83) * mm});
            skArc(sketch, "E514", {"start": v(76.61, 265.59) * mm, "mid": v(73.37, 268.64) * mm, "end": v(69.95, 271.5) * mm});
            skArc(sketch, "E515", {"start": v(-8.2, 326.18) * mm, "mid": v(-13.12, 291.64) * mm, "end": v(-10.01, 256.9) * mm});
            skArc(sketch, "E516", {"start": v(-10.01, 256.9) * mm, "mid": v(-9.87, 256.02) * mm, "end": v(-9.83, 255.12) * mm});
            skArc(sketch, "E517", {"start": v(4.4, 203.98) * mm, "mid": v(0.81, 222.4) * mm, "end": v(-6.14, 239.83) * mm});
            skArc(sketch, "E518", {"start": v(85.17, 235.01) * mm, "mid": v(81.08, 215.6) * mm, "end": v(78.2, 195.97) * mm});
            skArc(sketch, "E519", {"start": v(13.63, 189.02) * mm, "mid": v(17.25, 190.31) * mm, "end": v(19.76, 193.22) * mm});
            skArc(sketch, "E520", {"start": v(19.76, 193.22) * mm, "mid": v(20.62, 194.2) * mm, "end": v(21.86, 194.62) * mm});
            skArc(sketch, "E521", {"start": v(78.2, 195.97) * mm, "mid": v(77.2, 194.14) * mm, "end": v(75.2, 193.54) * mm});
            skArc(sketch, "E522", {"start": v(75.2, 193.54) * mm, "mid": v(48.55, 195.12) * mm, "end": v(21.86, 194.62) * mm});
            skArc(sketch, "E523", {"start": v(-8.2, 326.18) * mm, "mid": v(-0.66, 335.12) * mm, "end": v(11.05, 334.9) * mm});
            skArc(sketch, "E524", {"start": v(11.05, 334.9) * mm, "mid": v(32.2, 319.76) * mm, "end": v(47.56, 298.74) * mm});
            skArc(sketch, "E525", {"start": v(47.56, 298.74) * mm, "mid": v(57.27, 283.9) * mm, "end": v(69.95, 271.5) * mm});
            skArc(sketch, "E526", {"start": v(5.67, 191.04) * mm, "mid": v(6.66, 189.18) * mm, "end": v(8.67, 188.57) * mm});
            skArc(sketch, "E527", {"start": v(9.86, 195.38) * mm, "mid": v(9.11, 195.16) * mm, "end": v(8.58, 194.6) * mm});
            skArc(sketch, "E528", {"start": v(9.86, 195.38) * mm, "mid": v(9.93, 195.05) * mm, "end": v(10.07, 194.74) * mm});
            skLineSegment(sketch, "E529", {"start": v(8.58, 194.6) * mm, "end": v(10.07, 194.74) * mm, "construction": true});
            skArc(sketch, "E530.MirrorCS", {"start": v(9.99, 194.06) * mm, "mid": v(9.21, 194.14) * mm, "end": v(8.58, 194.6) * mm});
            skArc(sketch, "E531.MirrorCS", {"start": v(9.99, 194.06) * mm, "mid": v(10, 194.4) * mm, "end": v(10.07, 194.74) * mm});
            skLineSegment(sketch, "E532", {"start": v(9.86, 195.38) * mm, "end": v(9.92, 194.72) * mm, "construction": true});
            skLineSegment(sketch, "E533", {"start": v(4.4, 203.98) * mm, "end": v(5.67, 191.04) * mm});
            skLineSegment(sketch, "E534", {"start": v(8.67, 188.57) * mm, "end": v(13.63, 189.02) * mm});
            skLineSegment(sketch, "E535", {"start": v(9.33, 194.67) * mm, "end": v(9.25, 195.41) * mm, "construction": true});
            skLineSegment(sketch, "E536", {"start": v(8.01, 195.29) * mm, "end": v(10.5, 195.53) * mm, "construction": true});
            skPoint(sketch, "E537", {"position": v(8.74, 200.64) * mm});
            skLineSegment(sketch, "E538", {"start": v(12.44, 201.17) * mm, "end": v(12.48, 200.67) * mm});
            skLineSegment(sketch, "E539", {"start": v(12.48, 200.67) * mm, "end": v(11.47, 200.84) * mm});
            skLineSegment(sketch, "E540", {"start": v(11.47, 200.84) * mm, "end": v(11.67, 200.32) * mm});
            skLineSegment(sketch, "E541", {"start": v(11.67, 200.32) * mm, "end": v(9.97, 201.09) * mm});
            skLineSegment(sketch, "E542", {"start": v(9.97, 201.09) * mm, "end": v(10.98, 200.92) * mm});
            skLineSegment(sketch, "E543", {"start": v(10.98, 200.92) * mm, "end": v(10.79, 201.44) * mm});
            skLineSegment(sketch, "E544", {"start": v(10.79, 201.44) * mm, "end": v(12.44, 201.17) * mm});
            skLineSegment(sketch, "E545", {"start": v(10.98, 200.92) * mm, "end": v(11.47, 200.84) * mm, "construction": true});
            skLineSegment(sketch, "E546", {"start": v(10.79, 201.44) * mm, "end": v(10.9, 200.24) * mm, "construction": true});
            skLineSegment(sketch, "E547", {"start": v(11.67, 200.32) * mm, "end": v(10.9, 200.24) * mm, "construction": true});
            skPoint(sketch, "E548", {"position": v(10.84, 200.84) * mm});
            skLineSegment(sketch, "E549", {"start": v(10, 200.76) * mm, "end": v(12.45, 201) * mm, "construction": true});
            skLineSegment(sketch, "E550", {"start": v(10, 200.76) * mm, "end": v(9.97, 201.09) * mm, "construction": true});
            skPoint(sketch, "E551", {"position": v(11.23, 200.88) * mm});
            skLineSegment(sketch, "E552", {"start": v(9.91, 201.5) * mm, "end": v(12.4, 201.75) * mm, "construction": true});
            skLineSegment(sketch, "E553", {"start": v(11.23, 200.88) * mm, "end": v(11.15, 201.63) * mm, "construction": true});
            skLineSegment(sketch, "E554", {"start": v(13.02, 195.2) * mm, "end": v(13.07, 194.7) * mm});
            skLineSegment(sketch, "E555", {"start": v(13.07, 194.7) * mm, "end": v(12.06, 194.87) * mm});
            skLineSegment(sketch, "E556", {"start": v(12.06, 194.87) * mm, "end": v(12.26, 194.35) * mm});
            skLineSegment(sketch, "E557", {"start": v(12.26, 194.35) * mm, "end": v(10.56, 195.12) * mm});
            skLineSegment(sketch, "E558", {"start": v(10.56, 195.12) * mm, "end": v(11.57, 194.95) * mm});
            skLineSegment(sketch, "E559", {"start": v(11.57, 194.95) * mm, "end": v(11.37, 195.47) * mm});
            skLineSegment(sketch, "E560", {"start": v(11.37, 195.47) * mm, "end": v(13.02, 195.2) * mm});
            skLineSegment(sketch, "E561", {"start": v(11.57, 194.95) * mm, "end": v(12.06, 194.87) * mm, "construction": true});
            skLineSegment(sketch, "E562", {"start": v(11.37, 195.47) * mm, "end": v(11.5, 194.27) * mm, "construction": true});
            skLineSegment(sketch, "E563", {"start": v(12.26, 194.35) * mm, "end": v(11.5, 194.27) * mm, "construction": true});
            skPoint(sketch, "E564", {"position": v(11.43, 194.87) * mm});
            skLineSegment(sketch, "E565", {"start": v(10.6, 194.79) * mm, "end": v(13.04, 195.03) * mm, "construction": true});
            skLineSegment(sketch, "E566", {"start": v(10.6, 194.79) * mm, "end": v(10.56, 195.12) * mm, "construction": true});
            skPoint(sketch, "E567", {"position": v(11.82, 194.91) * mm});
            skSolve(sketch);
        }
    });
